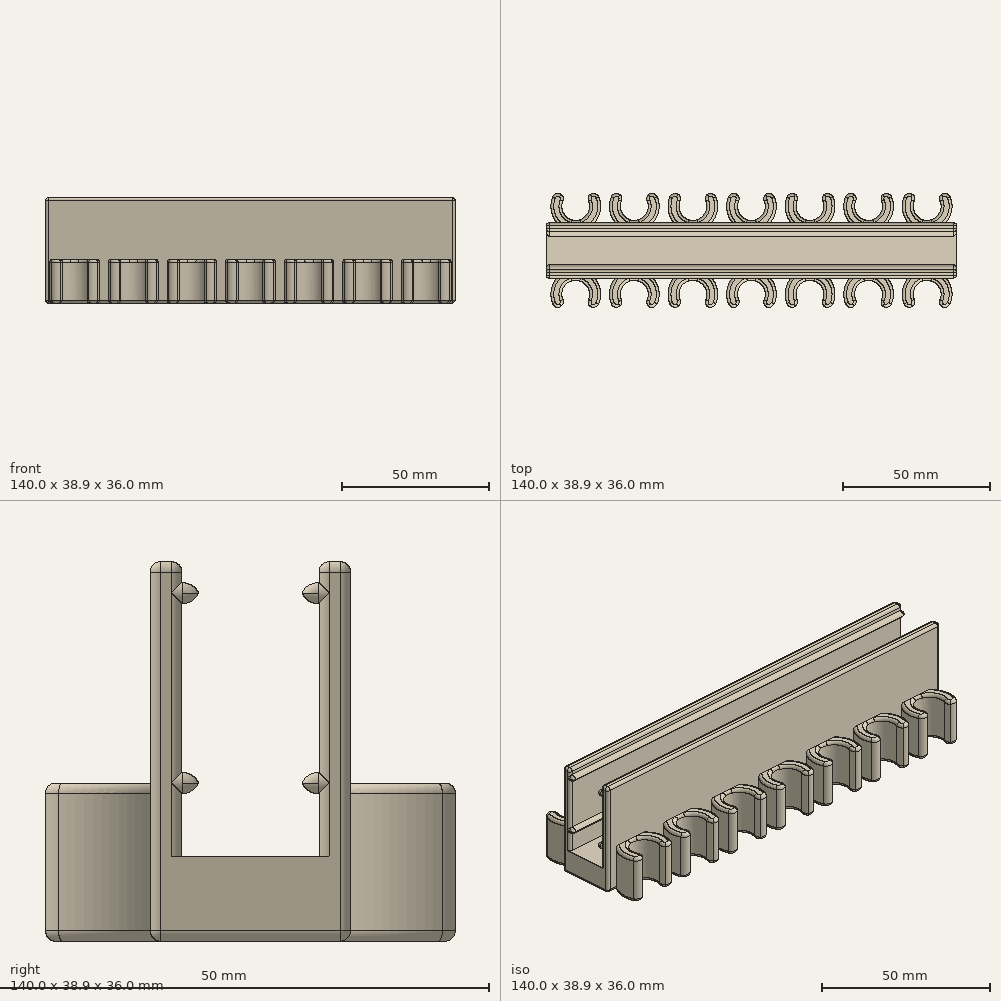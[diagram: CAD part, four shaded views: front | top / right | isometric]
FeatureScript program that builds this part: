
annotation { "Feature Type Name" : "Feature", "Feature Type Description" : "" }
export const myFeature = defineFeature(function(context is Context, id is Id, definition is map)
    precondition{}
    {
        {
            var Q0;
            Q0=qCreatedBy(makeId("Top.planeOp"),FACE);
            var sketch = newSketch(context, id + "F0", { "sketchPlane" : qUnion([Q0])});
            skLineSegment(sketch, "E0.0", {"start": v(-67.34, 9.93) * mm, "end": v(-70.86, 9.93) * mm});
            skLineSegment(sketch, "E1", {"start": v(-54.38, 9.93) * mm, "end": v(-47.34, 9.93) * mm});
            skArc(sketch, "E2", {"start": v(-67.37, 20.9) * mm, "mid": v(-69.36, 15.4) * mm, "end": v(-67.34, 9.93) * mm});
            skArc(sketch, "E3", {"start": v(-64.5, 18.48) * mm, "mid": v(-60.86, 10.68) * mm, "end": v(-57.22, 18.48) * mm});
            skLineSegment(sketch, "E4", {"start": v(-64.5, 18.48) * mm, "end": v(-67.37, 20.9) * mm});
            skLineSegment(sketch, "E5", {"start": v(-57.22, 18.48) * mm, "end": v(-54.35, 20.9) * mm});
            skLineSegment(sketch, "E6.1.0.0", {"start": v(-44.5, 18.48) * mm, "end": v(-47.37, 20.9) * mm});
            skArc(sketch, "E6.1.0.1", {"start": v(-47.37, 20.9) * mm, "mid": v(-49.36, 15.4) * mm, "end": v(-47.34, 9.93) * mm});
            skArc(sketch, "E6.1.0.2", {"start": v(-44.5, 18.48) * mm, "mid": v(-40.86, 10.68) * mm, "end": v(-37.22, 18.48) * mm});
            skLineSegment(sketch, "E6.1.0.3", {"start": v(-37.22, 18.48) * mm, "end": v(-34.35, 20.9) * mm});
            skLineSegment(sketch, "E6.2.0.0", {"start": v(-24.5, 18.48) * mm, "end": v(-27.37, 20.9) * mm});
            skArc(sketch, "E6.2.0.1", {"start": v(-27.37, 20.9) * mm, "mid": v(-29.36, 15.4) * mm, "end": v(-27.34, 9.93) * mm});
            skArc(sketch, "E6.2.0.2", {"start": v(-24.5, 18.48) * mm, "mid": v(-20.86, 10.68) * mm, "end": v(-17.22, 18.48) * mm});
            skLineSegment(sketch, "E6.2.0.3", {"start": v(-17.22, 18.48) * mm, "end": v(-14.35, 20.9) * mm});
            skLineSegment(sketch, "E6.3.0.0", {"start": v(-4.5, 18.48) * mm, "end": v(-7.37, 20.9) * mm});
            skArc(sketch, "E6.3.0.1", {"start": v(-7.37, 20.9) * mm, "mid": v(-9.36, 15.4) * mm, "end": v(-7.34, 9.93) * mm});
            skArc(sketch, "E6.3.0.2", {"start": v(-4.5, 18.48) * mm, "mid": v(-0.86, 10.68) * mm, "end": v(2.78, 18.48) * mm});
            skLineSegment(sketch, "E6.3.0.3", {"start": v(2.78, 18.48) * mm, "end": v(5.65, 20.9) * mm});
            skLineSegment(sketch, "E6.4.0.0", {"start": v(15.5, 18.48) * mm, "end": v(12.63, 20.9) * mm});
            skArc(sketch, "E6.4.0.1", {"start": v(12.63, 20.9) * mm, "mid": v(10.64, 15.4) * mm, "end": v(12.66, 9.93) * mm});
            skArc(sketch, "E6.4.0.2", {"start": v(15.5, 18.48) * mm, "mid": v(19.14, 10.68) * mm, "end": v(22.78, 18.48) * mm});
            skLineSegment(sketch, "E6.4.0.3", {"start": v(22.78, 18.48) * mm, "end": v(25.65, 20.9) * mm});
            skLineSegment(sketch, "E6.5.0.0", {"start": v(35.5, 18.48) * mm, "end": v(32.63, 20.9) * mm});
            skArc(sketch, "E6.5.0.1", {"start": v(32.63, 20.9) * mm, "mid": v(30.64, 15.4) * mm, "end": v(32.66, 9.93) * mm});
            skArc(sketch, "E6.5.0.2", {"start": v(35.5, 18.48) * mm, "mid": v(39.14, 10.68) * mm, "end": v(42.78, 18.48) * mm});
            skLineSegment(sketch, "E6.5.0.3", {"start": v(42.78, 18.48) * mm, "end": v(45.65, 20.9) * mm});
            skLineSegment(sketch, "E6.6.0.0", {"start": v(55.5, 18.48) * mm, "end": v(52.63, 20.9) * mm});
            skArc(sketch, "E6.6.0.1", {"start": v(52.63, 20.9) * mm, "mid": v(50.64, 15.4) * mm, "end": v(52.66, 9.93) * mm});
            skArc(sketch, "E6.6.0.2", {"start": v(55.5, 18.48) * mm, "mid": v(59.14, 10.68) * mm, "end": v(62.78, 18.48) * mm});
            skLineSegment(sketch, "E6.6.0.3", {"start": v(62.78, 18.48) * mm, "end": v(65.65, 20.9) * mm});
            skLineSegment(sketch, "E7.trimOffspring", {"start": v(-34.38, 9.93) * mm, "end": v(-27.34, 9.93) * mm});
            skLineSegment(sketch, "E8.trimOffspring", {"start": v(-14.38, 9.93) * mm, "end": v(-7.34, 9.93) * mm});
            skLineSegment(sketch, "E9.trimOffspring", {"start": v(5.62, 9.93) * mm, "end": v(12.66, 9.93) * mm});
            skLineSegment(sketch, "E10.trimOffspring", {"start": v(25.62, 9.93) * mm, "end": v(32.66, 9.93) * mm});
            skLineSegment(sketch, "E11.trimOffspring", {"start": v(45.62, 9.93) * mm, "end": v(52.66, 9.93) * mm});
            skLineSegment(sketch, "E12.trimOffspring", {"start": v(65.62, 9.93) * mm, "end": v(69.14, 9.93) * mm});
            skLineSegment(sketch, "E13", {"start": v(69.14, 9.93) * mm, "end": v(69.14, 0.43) * mm});
            skLineSegment(sketch, "E14", {"start": v(-70.86, 0.43) * mm, "end": v(-70.86, 9.93) * mm});
            skArc(sketch, "E15.trimOffspring", {"start": v(-54.38, 9.93) * mm, "mid": v(-52.36, 15.4) * mm, "end": v(-54.35, 20.9) * mm});
            skArc(sketch, "E16.trimOffspring", {"start": v(-34.38, 9.93) * mm, "mid": v(-32.36, 15.4) * mm, "end": v(-34.35, 20.9) * mm});
            skArc(sketch, "E17.trimOffspring", {"start": v(-14.38, 9.93) * mm, "mid": v(-12.36, 15.4) * mm, "end": v(-14.35, 20.9) * mm});
            skArc(sketch, "E18.trimOffspring", {"start": v(5.62, 9.93) * mm, "mid": v(7.64, 15.4) * mm, "end": v(5.65, 20.9) * mm});
            skArc(sketch, "E19.trimOffspring", {"start": v(25.62, 9.93) * mm, "mid": v(27.64, 15.4) * mm, "end": v(25.65, 20.9) * mm});
            skArc(sketch, "E20.trimOffspring", {"start": v(45.62, 9.93) * mm, "mid": v(47.64, 15.4) * mm, "end": v(45.65, 20.9) * mm});
            skArc(sketch, "E21.trimOffspring", {"start": v(65.62, 9.93) * mm, "mid": v(67.64, 15.4) * mm, "end": v(65.65, 20.9) * mm});
            skLineSegment(sketch, "E22", {"start": v(-70.86, 0.43) * mm, "end": v(69.14, 0.43) * mm});
            skSolve(sketch);
        }
        {
            var Q0;
            Q0=makeQuery(id+"F0.imprint","IMPRINT",FACE,{"disambiguationData":[TD([[makeQuery(id+"F0.imprint","IMPRINT",EDGE,{"derivedFrom":sQuery(id+"F0.wireOp",EDGE,"E0.0")}),1.0]])]});
            extrude(context, id + "F1", {"entities" : qUnion([Q0]), "depth" : 15 * mm});
        }
        {
            var Q0;
            Q0=makeQuery(id+"F1.opExtrude","CAP_FACE",FACE,{"disambiguationData":[OSD([sQuery(id+"F0.wireOp",EDGE,"E0.0"),sQuery(id+"F0.wireOp",EDGE,"E1"),sQuery(id+"F0.wireOp",EDGE,"E2"),sQuery(id+"F0.wireOp",EDGE,"E3"),sQuery(id+"F0.wireOp",EDGE,"E4"),sQuery(id+"F0.wireOp",EDGE,"E5"),sQuery(id+"F0.wireOp",EDGE,"E6.1.0.0"),sQuery(id+"F0.wireOp",EDGE,"E6.1.0.1"),sQuery(id+"F0.wireOp",EDGE,"E6.1.0.2"),sQuery(id+"F0.wireOp",EDGE,"E6.1.0.3"),sQuery(id+"F0.wireOp",EDGE,"E6.2.0.0"),sQuery(id+"F0.wireOp",EDGE,"E6.2.0.1"),sQuery(id+"F0.wireOp",EDGE,"E6.2.0.2"),sQuery(id+"F0.wireOp",EDGE,"E6.2.0.3"),sQuery(id+"F0.wireOp",EDGE,"E6.3.0.0"),sQuery(id+"F0.wireOp",EDGE,"E6.3.0.1"),sQuery(id+"F0.wireOp",EDGE,"E6.3.0.2"),sQuery(id+"F0.wireOp",EDGE,"E6.3.0.3"),sQuery(id+"F0.wireOp",EDGE,"E6.4.0.0"),sQuery(id+"F0.wireOp",EDGE,"E6.4.0.1"),sQuery(id+"F0.wireOp",EDGE,"E6.4.0.2"),sQuery(id+"F0.wireOp",EDGE,"E6.4.0.3"),sQuery(id+"F0.wireOp",EDGE,"E6.5.0.0"),sQuery(id+"F0.wireOp",EDGE,"E6.5.0.1"),sQuery(id+"F0.wireOp",EDGE,"E6.5.0.2"),sQuery(id+"F0.wireOp",EDGE,"E6.5.0.3"),sQuery(id+"F0.wireOp",EDGE,"E6.6.0.0"),sQuery(id+"F0.wireOp",EDGE,"E6.6.0.1"),sQuery(id+"F0.wireOp",EDGE,"E6.6.0.2"),sQuery(id+"F0.wireOp",EDGE,"E6.6.0.3"),sQuery(id+"F0.wireOp",EDGE,"E7.trimOffspring"),sQuery(id+"F0.wireOp",EDGE,"E8.trimOffspring"),sQuery(id+"F0.wireOp",EDGE,"E9.trimOffspring"),sQuery(id+"F0.wireOp",EDGE,"E10.trimOffspring"),sQuery(id+"F0.wireOp",EDGE,"E11.trimOffspring"),sQuery(id+"F0.wireOp",EDGE,"E12.trimOffspring"),sQuery(id+"F0.wireOp",EDGE,"E13"),sQuery(id+"F0.wireOp",EDGE,"E14"),sQuery(id+"F0.wireOp",EDGE,"532ac394-174c-4b63-97db-7bd679016d38.MirrorCS"),sQuery(id+"F0.wireOp",EDGE,"c05681d9-5c30-460e-90d8-317d1354b1ce.MirrorCS"),sQuery(id+"F0.wireOp",EDGE,"32390daf-9b7e-4632-84e2-2c85bb95c461.MirrorCS"),sQuery(id+"F0.wireOp",EDGE,"01d35694-a45f-4d88-895f-8290f8c5d0fa.MirrorCS"),sQuery(id+"F0.wireOp",EDGE,"542af53a-2461-44a8-a463-2401990404e3.MirrorCS"),sQuery(id+"F0.wireOp",EDGE,"50974922-5e88-405f-beb8-3457a77c02c8.MirrorCS"),sQuery(id+"F0.wireOp",EDGE,"9a1d3fd9-fa9d-4549-b3c9-1b6f4156c3cd.MirrorCS"),sQuery(id+"F0.wireOp",EDGE,"a6e0a99f-08c5-4def-a0f1-34a534e11dcb.MirrorCS"),sQuery(id+"F0.wireOp",EDGE,"85859d06-1dbf-410a-b8d5-c9659a816373.MirrorCS"),sQuery(id+"F0.wireOp",EDGE,"bb1e909d-42a2-430b-9b04-417277d03ddc.MirrorCS"),sQuery(id+"F0.wireOp",EDGE,"dd3b9dcb-f5d1-4367-832f-4155d99a0f53.MirrorCS"),sQuery(id+"F0.wireOp",EDGE,"95d68850-7c9b-44dc-a881-3d0e4710346b.MirrorCS"),sQuery(id+"F0.wireOp",EDGE,"cb06743f-0ef2-4490-bbfb-8208ed74ea54.MirrorCS"),sQuery(id+"F0.wireOp",EDGE,"8bc326fa-f220-4284-8f0f-31372991c1d0.MirrorCS"),sQuery(id+"F0.wireOp",EDGE,"61d51338-7109-43f4-9b26-85c12fe8dddc.MirrorCS"),sQuery(id+"F0.wireOp",EDGE,"ce3784da-6652-4a49-9029-c9d91698aa87.MirrorCS"),sQuery(id+"F0.wireOp",EDGE,"d0945471-aaf3-4442-996e-3f852aa85cf1.MirrorCS"),sQuery(id+"F0.wireOp",EDGE,"8b2dfc5c-2465-4331-950a-6d09cef2b768.MirrorCS"),sQuery(id+"F0.wireOp",EDGE,"7d31813b-8c42-40b0-b29a-5ec110f622fe.MirrorCS"),sQuery(id+"F0.wireOp",EDGE,"895840e0-dc65-487e-9daf-0c2dc7c5ed62.MirrorCS"),sQuery(id+"F0.wireOp",EDGE,"8443182a-963f-49ce-a89f-3df1a04f3471.MirrorCS"),sQuery(id+"F0.wireOp",EDGE,"07ffd3f9-8c22-4c6a-b8bf-5acca4b2ffac.MirrorCS"),sQuery(id+"F0.wireOp",EDGE,"76d25652-5567-47d0-86c3-db02a34db9a5.MirrorCS"),sQuery(id+"F0.wireOp",EDGE,"dc33f74a-ec70-42cc-9042-cb16d190b05e.MirrorCS"),sQuery(id+"F0.wireOp",EDGE,"53c614f0-cb83-4180-b471-f4b910b1941e.MirrorCS"),sQuery(id+"F0.wireOp",EDGE,"8c3fe504-64fb-41a5-82f7-0502142477f2.MirrorCS"),sQuery(id+"F0.wireOp",EDGE,"c5e72435-b01b-49d2-a203-b66ee6d8c885.MirrorCS"),sQuery(id+"F0.wireOp",EDGE,"19d9c78f-6ca9-424a-8982-828d9996df5d.MirrorCS"),sQuery(id+"F0.wireOp",EDGE,"1e641c59-deae-4c4d-ac71-77fc781e1db0.MirrorCS"),sQuery(id+"F0.wireOp",EDGE,"8ad635c3-a3ff-4ec7-b15b-9205133ed604.MirrorCS"),sQuery(id+"F0.wireOp",EDGE,"a49b1a12-b06d-43a0-ab83-94a35d7ba3b6.MirrorCS"),sQuery(id+"F0.wireOp",EDGE,"bcde4f51-7e24-40fe-ab17-a5a08aa31fcd.MirrorCS"),sQuery(id+"F0.wireOp",EDGE,"393ad891-5551-46bd-9f78-a4b207928a0a.MirrorCS"),sQuery(id+"F0.wireOp",EDGE,"b6b4b9c5-b1e0-4867-b064-6f7972b9574b.MirrorCS"),sQuery(id+"F0.wireOp",EDGE,"bb3e8bfc-5aea-4390-acdf-16b4f7f6207e.MirrorCS"),sQuery(id+"F0.wireOp",EDGE,"800d67ee-cbba-4591-aae2-d5247f1543fd.MirrorCS"),sQuery(id+"F0.wireOp",EDGE,"2f3bc7cb-4e2a-4f65-84bb-f5e8203fa07d.MirrorCS"),sQuery(id+"F0.wireOp",EDGE,"118a9efa-6c1d-49a3-b5ec-82cfceddfd38.MirrorCS"),sQuery(id+"F0.wireOp",EDGE,"E15.trimOffspring"),sQuery(id+"F0.wireOp",EDGE,"ff7412fe-da9d-4180-b698-66fe01a22e62.trimOffspring"),sQuery(id+"F0.wireOp",EDGE,"4496308e-0bbc-4981-83e8-c6594c4fa23c.trimOffspring"),sQuery(id+"F0.wireOp",EDGE,"E16.trimOffspring"),sQuery(id+"F0.wireOp",EDGE,"E17.trimOffspring"),sQuery(id+"F0.wireOp",EDGE,"E18.trimOffspring"),sQuery(id+"F0.wireOp",EDGE,"E19.trimOffspring"),sQuery(id+"F0.wireOp",EDGE,"E20.trimOffspring"),sQuery(id+"F0.wireOp",EDGE,"E21.trimOffspring"),sQuery(id+"F0.wireOp",EDGE,"9ee47ddf-eb93-4049-a59d-f92f7ca8a253.trimOffspring"),sQuery(id+"F0.wireOp",EDGE,"7a309b6b-a9af-437c-b1e7-8ac5cff17d63.trimOffspring"),sQuery(id+"F0.wireOp",EDGE,"a429b228-3a7c-4e15-a61f-9e9e64befbed.trimOffspring"),sQuery(id+"F0.wireOp",EDGE,"04ba02ae-33ee-469e-a187-3e9e85af7747.trimOffspring"),sQuery(id+"F0.wireOp",EDGE,"f3fa248c-7e1b-4735-8d48-9965b376265a.trimOffspring")])],"isStart":false});
            var sketch = newSketch(context, id + "F2", { "sketchPlane" : qUnion([Q0])});
            skLineSegment(sketch, "E23", {"start": v(-70.86, 9.93) * mm, "end": v(69.14, 9.93) * mm});
            skLineSegment(sketch, "E24", {"start": v(69.14, 6.93) * mm, "end": v(-70.86, 6.93) * mm});
            skSolve(sketch);
        }
        {
            var Q0;
            {var subQ0=sQuery(id+"F2.wireOp",EDGE,"E24");Q0=makeQuery(id+"F2.imprint","IMPRINT",FACE,{"disambiguationData":[TD([[makeQuery(id+"F2.imprint","IMPRINT",EDGE,{"derivedFrom":subQ0}),1.0]])]});}
            extrude(context, id + "F3", {"entities" : qUnion([Q0]), "operationType" : NewBodyOperationType.REMOVE, "oppositeDirection" : true, "depth" : 7 * mm});
        }
        {
            var Q0;
            {var subQ19=sQuery(id+"F2.wireOp",EDGE,"E24");Q0=makeQuery(id+"F2.imprint","IMPRINT",FACE,{"disambiguationData":[TD([[makeQuery(id+"F2.imprint","IMPRINT",EDGE,{"derivedFrom":subQ19}),-1.0]])]});}
            var Q1;
            {var subQ11=sQuery(id+"F2.wireOp",EDGE,"yWHUweg9-QDUr-fazm-nHLA-YuGdJbdEGouv");Q1=makeQuery(id+"F2.imprint","IMPRINT",FACE,{"disambiguationData":[TD([[makeQuery(id+"F2.imprint","IMPRINT",EDGE,{"derivedFrom":subQ11}),1.0]])]});}
            extrude(context, id + "F4", {"entities" : qUnion([Q0, Q1]), "operationType" : NewBodyOperationType.ADD, "depth" : 21 * mm});
        }
        {
            var Q0;
            Q0=makeQuery(id+"F1.opExtrude","SWEPT_EDGE",EDGE,{"disambiguationData":[OSD([sQuery(id+"F0.wireOp",EDGE,"E3"),sQuery(id+"F0.wireOp",EDGE,"E4")])]});
            var Q1;
            Q1=makeQuery(id+"F1.opExtrude","SWEPT_EDGE",EDGE,{"disambiguationData":[OSD([sQuery(id+"F0.wireOp",EDGE,"E2"),sQuery(id+"F0.wireOp",EDGE,"E4")])]});
            var Q2;
            Q2=makeQuery(id+"F1.opExtrude","SWEPT_EDGE",EDGE,{"disambiguationData":[OSD([sQuery(id+"F0.wireOp",EDGE,"E3"),sQuery(id+"F0.wireOp",EDGE,"E5")])]});
            var Q3;
            Q3=makeQuery(id+"F1.opExtrude","SWEPT_EDGE",EDGE,{"disambiguationData":[OSD([sQuery(id+"F0.wireOp",EDGE,"E5"),sQuery(id+"F0.wireOp",EDGE,"E15.trimOffspring")])]});
            var Q4;
            Q4=makeQuery(id+"F1.opExtrude","SWEPT_EDGE",EDGE,{"disambiguationData":[OSD([sQuery(id+"F0.wireOp",EDGE,"E6.1.0.0"),sQuery(id+"F0.wireOp",EDGE,"E6.1.0.1")])]});
            var Q5;
            Q5=makeQuery(id+"F1.opExtrude","SWEPT_EDGE",EDGE,{"disambiguationData":[OSD([sQuery(id+"F0.wireOp",EDGE,"E6.1.0.0"),sQuery(id+"F0.wireOp",EDGE,"E6.1.0.2")])]});
            var Q6;
            Q6=makeQuery(id+"F1.opExtrude","SWEPT_EDGE",EDGE,{"disambiguationData":[OSD([sQuery(id+"F0.wireOp",EDGE,"E6.1.0.2"),sQuery(id+"F0.wireOp",EDGE,"E6.1.0.3")])]});
            var Q7;
            Q7=makeQuery(id+"F1.opExtrude","SWEPT_EDGE",EDGE,{"disambiguationData":[OSD([sQuery(id+"F0.wireOp",EDGE,"E6.1.0.3"),sQuery(id+"F0.wireOp",EDGE,"E16.trimOffspring")])]});
            var Q8;
            Q8=makeQuery(id+"F1.opExtrude","SWEPT_EDGE",EDGE,{"disambiguationData":[OSD([sQuery(id+"F0.wireOp",EDGE,"E6.2.0.0"),sQuery(id+"F0.wireOp",EDGE,"E6.2.0.1")])]});
            var Q9;
            Q9=makeQuery(id+"F1.opExtrude","SWEPT_EDGE",EDGE,{"disambiguationData":[OSD([sQuery(id+"F0.wireOp",EDGE,"E6.2.0.0"),sQuery(id+"F0.wireOp",EDGE,"E6.2.0.2")])]});
            var Q10;
            Q10=makeQuery(id+"F1.opExtrude","SWEPT_EDGE",EDGE,{"disambiguationData":[OSD([sQuery(id+"F0.wireOp",EDGE,"E6.2.0.2"),sQuery(id+"F0.wireOp",EDGE,"E6.2.0.3")])]});
            var Q11;
            Q11=makeQuery(id+"F1.opExtrude","SWEPT_EDGE",EDGE,{"disambiguationData":[OSD([sQuery(id+"F0.wireOp",EDGE,"E6.2.0.3"),sQuery(id+"F0.wireOp",EDGE,"E17.trimOffspring")])]});
            var Q12;
            Q12=makeQuery(id+"F1.opExtrude","SWEPT_EDGE",EDGE,{"disambiguationData":[OSD([sQuery(id+"F0.wireOp",EDGE,"E6.3.0.0"),sQuery(id+"F0.wireOp",EDGE,"E6.3.0.1")])]});
            var Q13;
            Q13=makeQuery(id+"F1.opExtrude","SWEPT_EDGE",EDGE,{"disambiguationData":[OSD([sQuery(id+"F0.wireOp",EDGE,"E6.3.0.0"),sQuery(id+"F0.wireOp",EDGE,"E6.3.0.2")])]});
            var Q14;
            Q14=makeQuery(id+"F1.opExtrude","SWEPT_EDGE",EDGE,{"disambiguationData":[OSD([sQuery(id+"F0.wireOp",EDGE,"E6.3.0.2"),sQuery(id+"F0.wireOp",EDGE,"E6.3.0.3")])]});
            var Q15;
            Q15=makeQuery(id+"F1.opExtrude","SWEPT_EDGE",EDGE,{"disambiguationData":[OSD([sQuery(id+"F0.wireOp",EDGE,"E6.3.0.3"),sQuery(id+"F0.wireOp",EDGE,"E18.trimOffspring")])]});
            var Q16;
            Q16=makeQuery(id+"F1.opExtrude","SWEPT_EDGE",EDGE,{"disambiguationData":[OSD([sQuery(id+"F0.wireOp",EDGE,"E6.4.0.0"),sQuery(id+"F0.wireOp",EDGE,"E6.4.0.1")])]});
            var Q17;
            Q17=makeQuery(id+"F1.opExtrude","SWEPT_EDGE",EDGE,{"disambiguationData":[OSD([sQuery(id+"F0.wireOp",EDGE,"E6.4.0.0"),sQuery(id+"F0.wireOp",EDGE,"E6.4.0.2")])]});
            var Q18;
            Q18=makeQuery(id+"F1.opExtrude","SWEPT_EDGE",EDGE,{"disambiguationData":[OSD([sQuery(id+"F0.wireOp",EDGE,"E6.4.0.2"),sQuery(id+"F0.wireOp",EDGE,"E6.4.0.3")])]});
            var Q19;
            Q19=makeQuery(id+"F1.opExtrude","SWEPT_EDGE",EDGE,{"disambiguationData":[OSD([sQuery(id+"F0.wireOp",EDGE,"E6.4.0.3"),sQuery(id+"F0.wireOp",EDGE,"E19.trimOffspring")])]});
            var Q20;
            Q20=makeQuery(id+"F1.opExtrude","SWEPT_EDGE",EDGE,{"disambiguationData":[OSD([sQuery(id+"F0.wireOp",EDGE,"E6.5.0.0"),sQuery(id+"F0.wireOp",EDGE,"E6.5.0.1")])]});
            var Q21;
            Q21=makeQuery(id+"F1.opExtrude","SWEPT_EDGE",EDGE,{"disambiguationData":[OSD([sQuery(id+"F0.wireOp",EDGE,"E6.5.0.0"),sQuery(id+"F0.wireOp",EDGE,"E6.5.0.2")])]});
            var Q22;
            Q22=makeQuery(id+"F1.opExtrude","SWEPT_EDGE",EDGE,{"disambiguationData":[OSD([sQuery(id+"F0.wireOp",EDGE,"E6.5.0.3"),sQuery(id+"F0.wireOp",EDGE,"E20.trimOffspring")])]});
            var Q23;
            Q23=makeQuery(id+"F1.opExtrude","SWEPT_EDGE",EDGE,{"disambiguationData":[OSD([sQuery(id+"F0.wireOp",EDGE,"E6.5.0.2"),sQuery(id+"F0.wireOp",EDGE,"E6.5.0.3")])]});
            var Q24;
            Q24=makeQuery(id+"F1.opExtrude","SWEPT_EDGE",EDGE,{"disambiguationData":[OSD([sQuery(id+"F0.wireOp",EDGE,"E6.6.0.0"),sQuery(id+"F0.wireOp",EDGE,"E6.6.0.1")])]});
            var Q25;
            Q25=makeQuery(id+"F1.opExtrude","SWEPT_EDGE",EDGE,{"disambiguationData":[OSD([sQuery(id+"F0.wireOp",EDGE,"E6.6.0.0"),sQuery(id+"F0.wireOp",EDGE,"E6.6.0.2")])]});
            var Q26;
            Q26=makeQuery(id+"F1.opExtrude","SWEPT_EDGE",EDGE,{"disambiguationData":[OSD([sQuery(id+"F0.wireOp",EDGE,"E6.6.0.2"),sQuery(id+"F0.wireOp",EDGE,"E6.6.0.3")])]});
            var Q27;
            Q27=makeQuery(id+"F1.opExtrude","SWEPT_EDGE",EDGE,{"disambiguationData":[OSD([sQuery(id+"F0.wireOp",EDGE,"E6.6.0.3"),sQuery(id+"F0.wireOp",EDGE,"E21.trimOffspring")])]});
            fillet(context, id + "F5", {"entities" : qUnion([Q0, Q1, Q2, Q3, Q4, Q5, Q6, Q7, Q8, Q9, Q10, Q11, Q12, Q13, Q14, Q15, Q16, Q17, Q18, Q19, Q20, Q21, Q22, Q23, Q24, Q25, Q26, Q27]), "radius" : 2 * mm, "tangentPropagation" : true, "allowEdgeOverflow" : false});
        }
        {
            var Q0;
            {var subQ0=sQuery(id+"F0.wireOp",EDGE,"E13");Q0=makeQuery(id+"F4.boolean.opBoolean","MERGE",FACE,{"derivedFrom":[makeQuery(id+"F1.opExtrude","SWEPT_FACE",FACE,{"disambiguationData":[OSD([subQ0])]}),makeQuery(id+"F4.opExtrude","SWEPT_FACE",FACE,{"disambiguationData":[OSD([subQ0])]})]});}
            var sketch = newSketch(context, id + "F6", { "sketchPlane" : qUnion([Q0])});
            skLineSegment(sketch, "E25", {"start": v(6.93, 15) * mm, "end": v(6.93, 33) * mm});
            skLineSegment(sketch, "E26.bottom", {"start": v(5.18, 14) * mm, "end": v(8.68, 14) * mm});
            skLineSegment(sketch, "E26.top", {"start": v(5.18, 16) * mm, "end": v(8.68, 16) * mm});
            skLineSegment(sketch, "E26.left", {"start": v(5.18, 14) * mm, "end": v(5.18, 16) * mm});
            skLineSegment(sketch, "E26.right", {"start": v(8.68, 14) * mm, "end": v(8.68, 16) * mm});
            skPoint(sketch, "E26.middle", {"position": v(6.93, 15) * mm});
            skLineSegment(sketch, "E27.bottom", {"start": v(5.18, 32) * mm, "end": v(8.68, 32) * mm});
            skLineSegment(sketch, "E27.top", {"start": v(5.18, 34) * mm, "end": v(8.68, 34) * mm});
            skLineSegment(sketch, "E27.left", {"start": v(5.18, 32) * mm, "end": v(5.18, 34) * mm});
            skLineSegment(sketch, "E27.right", {"start": v(8.68, 32) * mm, "end": v(8.68, 34) * mm});
            skPoint(sketch, "E27.middle", {"position": v(6.93, 33) * mm});
            skSolve(sketch);
        }
        {
            var Q0;
            {var subQ0=sQuery(id+"F6.wireOp",EDGE,"E26.left");Q0=makeQuery(id+"F6.imprint","IMPRINT",FACE,{"disambiguationData":[TD([[makeQuery(id+"F6.imprint","IMPRINT",EDGE,{"derivedFrom":subQ0}),-1.0]])]});}
            var Q1;
            {var subQ0=sQuery(id+"F6.wireOp",EDGE,"E27.left");Q1=makeQuery(id+"F6.imprint","IMPRINT",FACE,{"disambiguationData":[TD([[makeQuery(id+"F6.imprint","IMPRINT",EDGE,{"derivedFrom":subQ0}),-1.0]])]});}
            var Q2;
            {var subQ0=sQuery(id+"F0.wireOp",EDGE,"E14");Q2=makeQuery(id+"F4.boolean.opBoolean","MERGE",FACE,{"derivedFrom":[makeQuery(id+"F1.opExtrude","SWEPT_FACE",FACE,{"disambiguationData":[OSD([subQ0])]}),makeQuery(id+"F4.opExtrude","SWEPT_FACE",FACE,{"disambiguationData":[OSD([subQ0])]})]});}
            extrude(context, id + "F7", {"entities" : qUnion([Q0, Q1]), "operationType" : NewBodyOperationType.ADD, "endBound" : BoundingType.UP_TO_SURFACE, "oppositeDirection" : true, "endBoundEntityFace" : qUnion([Q2]), "depth" : 25 * mm});
        }
        {
            var Q0;
            Q0=makeQuery(id+"F7.opExtrude","SWEPT_EDGE",EDGE,{"disambiguationData":[OSD([sQuery(id+"F6.wireOp",EDGE,"E27.top"),sQuery(id+"F6.wireOp",EDGE,"E27.left")])]});
            var Q1;
            Q1=makeQuery(id+"F7.opExtrude","SWEPT_EDGE",EDGE,{"disambiguationData":[OSD([sQuery(id+"F6.wireOp",EDGE,"E27.bottom"),sQuery(id+"F6.wireOp",EDGE,"E27.left")])]});
            var Q2;
            Q2=makeQuery(id+"F7.opExtrude","SWEPT_EDGE",EDGE,{"disambiguationData":[OSD([sQuery(id+"F6.wireOp",EDGE,"E26.top"),sQuery(id+"F6.wireOp",EDGE,"E26.left")])]});
            var Q3;
            Q3=makeQuery(id+"F7.opExtrude","SWEPT_EDGE",EDGE,{"disambiguationData":[OSD([sQuery(id+"F6.wireOp",EDGE,"E26.bottom"),sQuery(id+"F6.wireOp",EDGE,"E26.left")])]});
            fillet(context, id + "F8", {"entities" : qUnion([Q0, Q1, Q2, Q3]), "radius" : 1.7 * mm, "tangentPropagation" : true, "allowEdgeOverflow" : false});
        }
        {
            var Q0;
            Q0=makeQuery(id+"F4.opExtrude","CAP_FACE",FACE,{"disambiguationData":[OSD([sQuery(id+"F0.wireOp",EDGE,"E13"),sQuery(id+"F0.wireOp",EDGE,"E14"),sQuery(id+"F2.wireOp",EDGE,"E23"),sQuery(id+"F2.wireOp",EDGE,"E24")])],"isStart":false});
            var Q1;
            {var subQ0=sQuery(id+"F2.wireOp",EDGE,"E24");var subQ1=sQuery(id+"F0.wireOp",EDGE,"E13");var subQ2=sQuery(id+"F6.wireOp",EDGE,"E27.top");Q1=makeQuery(id+"F7.boolean.opBoolean","SPLIT",EDGE,{"disambiguationData":[TD([makeQuery(id+"F7.opExtrude","SWEPT_FACE",FACE,{"disambiguationData":[OSD([subQ2])]})])],"derivedFrom":makeQuery(id+"F4.boolean.opBoolean","MERGE",EDGE,{"derivedFrom":[makeQuery(id+"F3.boolean.opBoolean","COPY",EDGE,{"derivedFrom":makeQuery(id+"F3.opExtrude","SWEPT_EDGE",EDGE,{"disambiguationData":[OSD([subQ1,subQ0])]})}),makeQuery(id+"F4.opExtrude","SWEPT_EDGE",EDGE,{"disambiguationData":[OSD([subQ1,subQ0])]})]})});}
            var Q2;
            {var subQ0=sQuery(id+"F6.wireOp",EDGE,"E27.left");var subQ1=sQuery(id+"F6.wireOp",EDGE,"E27.top");var subQ2=sQuery(id+"F6.wireOp",EDGE,"E25");var subQ3=sQuery(id+"F2.wireOp",EDGE,"E24");var subQ4=sQuery(id+"F0.wireOp",EDGE,"E13");Q2=makeQuery(id+"F8.opFillet","BLEND_EDGE",EDGE,{"blendedFrom":[makeQuery(id+"F7.opExtrude","SWEPT_EDGE",EDGE,{"disambiguationData":[OSD([subQ1,subQ0])]}),makeQuery(id+"F7.boolean.opBoolean","MERGE",FACE,{"derivedFrom":[makeQuery(id+"F4.boolean.opBoolean","MERGE",FACE,{"derivedFrom":[makeQuery(id+"F1.opExtrude","SWEPT_FACE",FACE,{"disambiguationData":[OSD([subQ4])]}),makeQuery(id+"F4.opExtrude","SWEPT_FACE",FACE,{"disambiguationData":[OSD([subQ4])]})]}),makeQuery(id+"F7.opExtrude","CAP_FACE",FACE,{"disambiguationData":[OSD([subQ4,subQ3,subQ2,sQuery(id+"F6.wireOp",EDGE,"E26.bottom"),sQuery(id+"F6.wireOp",EDGE,"E26.top"),sQuery(id+"F6.wireOp",EDGE,"E26.left")])],"isStart":true}),makeQuery(id+"F7.opExtrude","CAP_FACE",FACE,{"disambiguationData":[OSD([subQ4,subQ3,subQ2,sQuery(id+"F6.wireOp",EDGE,"E27.bottom"),subQ1,subQ0])],"isStart":true})]})],"blendedInto":[makeQuery(id+"F7.boolean.opBoolean","MERGE",FACE,{"derivedFrom":[makeQuery(id+"F4.boolean.opBoolean","MERGE",FACE,{"derivedFrom":[makeQuery(id+"F1.opExtrude","SWEPT_FACE",FACE,{"disambiguationData":[OSD([subQ4])]}),makeQuery(id+"F4.opExtrude","SWEPT_FACE",FACE,{"disambiguationData":[OSD([subQ4])]})]}),makeQuery(id+"F7.opExtrude","CAP_FACE",FACE,{"disambiguationData":[OSD([subQ4,subQ3,subQ2,sQuery(id+"F6.wireOp",EDGE,"E26.bottom"),sQuery(id+"F6.wireOp",EDGE,"E26.top"),sQuery(id+"F6.wireOp",EDGE,"E26.left")])],"isStart":true}),makeQuery(id+"F7.opExtrude","CAP_FACE",FACE,{"disambiguationData":[OSD([subQ4,subQ3,subQ2,sQuery(id+"F6.wireOp",EDGE,"E27.bottom"),subQ1,subQ0])],"isStart":true})]})]});}
            var Q3;
            {var subQ0=sQuery(id+"F6.wireOp",EDGE,"E27.left");var subQ1=sQuery(id+"F6.wireOp",EDGE,"E27.bottom");var subQ2=sQuery(id+"F6.wireOp",EDGE,"E25");var subQ3=sQuery(id+"F2.wireOp",EDGE,"E24");var subQ4=sQuery(id+"F0.wireOp",EDGE,"E13");Q3=makeQuery(id+"F8.opFillet","BLEND_EDGE",EDGE,{"blendedFrom":[makeQuery(id+"F7.opExtrude","SWEPT_EDGE",EDGE,{"disambiguationData":[OSD([subQ1,subQ0])]}),makeQuery(id+"F7.boolean.opBoolean","MERGE",FACE,{"derivedFrom":[makeQuery(id+"F4.boolean.opBoolean","MERGE",FACE,{"derivedFrom":[makeQuery(id+"F1.opExtrude","SWEPT_FACE",FACE,{"disambiguationData":[OSD([subQ4])]}),makeQuery(id+"F4.opExtrude","SWEPT_FACE",FACE,{"disambiguationData":[OSD([subQ4])]})]}),makeQuery(id+"F7.opExtrude","CAP_FACE",FACE,{"disambiguationData":[OSD([subQ4,subQ3,subQ2,sQuery(id+"F6.wireOp",EDGE,"E26.bottom"),sQuery(id+"F6.wireOp",EDGE,"E26.top"),sQuery(id+"F6.wireOp",EDGE,"E26.left")])],"isStart":true}),makeQuery(id+"F7.opExtrude","CAP_FACE",FACE,{"disambiguationData":[OSD([subQ4,subQ3,subQ2,subQ1,sQuery(id+"F6.wireOp",EDGE,"E27.top"),subQ0])],"isStart":true})]})],"blendedInto":[makeQuery(id+"F7.boolean.opBoolean","MERGE",FACE,{"derivedFrom":[makeQuery(id+"F4.boolean.opBoolean","MERGE",FACE,{"derivedFrom":[makeQuery(id+"F1.opExtrude","SWEPT_FACE",FACE,{"disambiguationData":[OSD([subQ4])]}),makeQuery(id+"F4.opExtrude","SWEPT_FACE",FACE,{"disambiguationData":[OSD([subQ4])]})]}),makeQuery(id+"F7.opExtrude","CAP_FACE",FACE,{"disambiguationData":[OSD([subQ4,subQ3,subQ2,sQuery(id+"F6.wireOp",EDGE,"E26.bottom"),sQuery(id+"F6.wireOp",EDGE,"E26.top"),sQuery(id+"F6.wireOp",EDGE,"E26.left")])],"isStart":true}),makeQuery(id+"F7.opExtrude","CAP_FACE",FACE,{"disambiguationData":[OSD([subQ4,subQ3,subQ2,subQ1,sQuery(id+"F6.wireOp",EDGE,"E27.top"),subQ0])],"isStart":true})]})]});}
            var Q4;
            {var subQ0=sQuery(id+"F0.wireOp",EDGE,"E13");var subQ1=sQuery(id+"F2.wireOp",EDGE,"E24");var subQ4=sQuery(id+"F6.wireOp",EDGE,"E26.top");Q4=makeQuery(id+"F7.boolean.opBoolean","SPLIT",EDGE,{"disambiguationData":[TD([makeQuery(id+"F7.opExtrude","SWEPT_FACE",FACE,{"disambiguationData":[OSD([subQ4])]})])],"derivedFrom":makeQuery(id+"F4.boolean.opBoolean","MERGE",EDGE,{"derivedFrom":[makeQuery(id+"F3.boolean.opBoolean","COPY",EDGE,{"derivedFrom":makeQuery(id+"F3.opExtrude","SWEPT_EDGE",EDGE,{"disambiguationData":[OSD([subQ0,subQ1])]})}),makeQuery(id+"F4.opExtrude","SWEPT_EDGE",EDGE,{"disambiguationData":[OSD([subQ0,subQ1])]})]})});}
            var Q5;
            {var subQ0=sQuery(id+"F0.wireOp",EDGE,"E13");Q5=makeQuery(id+"F4.boolean.opBoolean","MERGE",EDGE,{"derivedFrom":[makeQuery(id+"F1.opExtrude","SWEPT_EDGE",EDGE,{"disambiguationData":[OSD([sQuery(id+"F0.wireOp",EDGE,"E12.trimOffspring"),subQ0])]}),makeQuery(id+"F4.opExtrude","SWEPT_EDGE",EDGE,{"disambiguationData":[OSD([subQ0,sQuery(id+"F2.wireOp",EDGE,"E23")])]})]});}
            var Q6;
            {var subQ0=sQuery(id+"F6.wireOp",EDGE,"E25");var subQ1=sQuery(id+"F2.wireOp",EDGE,"E24");var subQ2=sQuery(id+"F0.wireOp",EDGE,"E13");var subQ3=sQuery(id+"F6.wireOp",EDGE,"E26.left");var subQ4=sQuery(id+"F6.wireOp",EDGE,"E26.top");Q6=makeQuery(id+"F8.opFillet","BLEND_EDGE",EDGE,{"blendedFrom":[makeQuery(id+"F7.opExtrude","SWEPT_EDGE",EDGE,{"disambiguationData":[OSD([subQ4,subQ3])]}),makeQuery(id+"F7.boolean.opBoolean","MERGE",FACE,{"derivedFrom":[makeQuery(id+"F4.boolean.opBoolean","MERGE",FACE,{"derivedFrom":[makeQuery(id+"F1.opExtrude","SWEPT_FACE",FACE,{"disambiguationData":[OSD([subQ2])]}),makeQuery(id+"F4.opExtrude","SWEPT_FACE",FACE,{"disambiguationData":[OSD([subQ2])]})]}),makeQuery(id+"F7.opExtrude","CAP_FACE",FACE,{"disambiguationData":[OSD([subQ2,subQ1,subQ0,sQuery(id+"F6.wireOp",EDGE,"E26.bottom"),subQ4,subQ3])],"isStart":true}),makeQuery(id+"F7.opExtrude","CAP_FACE",FACE,{"disambiguationData":[OSD([subQ2,subQ1,subQ0,sQuery(id+"F6.wireOp",EDGE,"E27.bottom"),sQuery(id+"F6.wireOp",EDGE,"E27.top"),sQuery(id+"F6.wireOp",EDGE,"E27.left")])],"isStart":true})]})],"blendedInto":[makeQuery(id+"F7.boolean.opBoolean","MERGE",FACE,{"derivedFrom":[makeQuery(id+"F4.boolean.opBoolean","MERGE",FACE,{"derivedFrom":[makeQuery(id+"F1.opExtrude","SWEPT_FACE",FACE,{"disambiguationData":[OSD([subQ2])]}),makeQuery(id+"F4.opExtrude","SWEPT_FACE",FACE,{"disambiguationData":[OSD([subQ2])]})]}),makeQuery(id+"F7.opExtrude","CAP_FACE",FACE,{"disambiguationData":[OSD([subQ2,subQ1,subQ0,sQuery(id+"F6.wireOp",EDGE,"E26.bottom"),subQ4,subQ3])],"isStart":true}),makeQuery(id+"F7.opExtrude","CAP_FACE",FACE,{"disambiguationData":[OSD([subQ2,subQ1,subQ0,sQuery(id+"F6.wireOp",EDGE,"E27.bottom"),sQuery(id+"F6.wireOp",EDGE,"E27.top"),sQuery(id+"F6.wireOp",EDGE,"E27.left")])],"isStart":true})]})]});}
            var Q7;
            {var subQ0=sQuery(id+"F6.wireOp",EDGE,"E25");var subQ1=sQuery(id+"F2.wireOp",EDGE,"E24");var subQ2=sQuery(id+"F0.wireOp",EDGE,"E13");var subQ3=sQuery(id+"F6.wireOp",EDGE,"E26.left");var subQ4=sQuery(id+"F6.wireOp",EDGE,"E26.bottom");Q7=makeQuery(id+"F8.opFillet","BLEND_EDGE",EDGE,{"blendedFrom":[makeQuery(id+"F7.opExtrude","SWEPT_EDGE",EDGE,{"disambiguationData":[OSD([subQ4,subQ3])]}),makeQuery(id+"F7.boolean.opBoolean","MERGE",FACE,{"derivedFrom":[makeQuery(id+"F4.boolean.opBoolean","MERGE",FACE,{"derivedFrom":[makeQuery(id+"F1.opExtrude","SWEPT_FACE",FACE,{"disambiguationData":[OSD([subQ2])]}),makeQuery(id+"F4.opExtrude","SWEPT_FACE",FACE,{"disambiguationData":[OSD([subQ2])]})]}),makeQuery(id+"F7.opExtrude","CAP_FACE",FACE,{"disambiguationData":[OSD([subQ2,subQ1,subQ0,subQ4,sQuery(id+"F6.wireOp",EDGE,"E26.top"),subQ3])],"isStart":true}),makeQuery(id+"F7.opExtrude","CAP_FACE",FACE,{"disambiguationData":[OSD([subQ2,subQ1,subQ0,sQuery(id+"F6.wireOp",EDGE,"E27.bottom"),sQuery(id+"F6.wireOp",EDGE,"E27.top"),sQuery(id+"F6.wireOp",EDGE,"E27.left")])],"isStart":true})]})],"blendedInto":[makeQuery(id+"F7.boolean.opBoolean","MERGE",FACE,{"derivedFrom":[makeQuery(id+"F4.boolean.opBoolean","MERGE",FACE,{"derivedFrom":[makeQuery(id+"F1.opExtrude","SWEPT_FACE",FACE,{"disambiguationData":[OSD([subQ2])]}),makeQuery(id+"F4.opExtrude","SWEPT_FACE",FACE,{"disambiguationData":[OSD([subQ2])]})]}),makeQuery(id+"F7.opExtrude","CAP_FACE",FACE,{"disambiguationData":[OSD([subQ2,subQ1,subQ0,subQ4,sQuery(id+"F6.wireOp",EDGE,"E26.top"),subQ3])],"isStart":true}),makeQuery(id+"F7.opExtrude","CAP_FACE",FACE,{"disambiguationData":[OSD([subQ2,subQ1,subQ0,sQuery(id+"F6.wireOp",EDGE,"E27.bottom"),sQuery(id+"F6.wireOp",EDGE,"E27.top"),sQuery(id+"F6.wireOp",EDGE,"E27.left")])],"isStart":true})]})]});}
            var Q8;
            {var subQ0=sQuery(id+"F2.wireOp",EDGE,"E24");var subQ1=sQuery(id+"F0.wireOp",EDGE,"E13");var subQ3=sQuery(id+"F6.wireOp",EDGE,"E26.bottom");Q8=makeQuery(id+"F7.boolean.opBoolean","SPLIT",EDGE,{"disambiguationData":[TD([makeQuery(id+"F7.opExtrude","SWEPT_FACE",FACE,{"disambiguationData":[OSD([subQ3])]})])],"derivedFrom":makeQuery(id+"F4.boolean.opBoolean","MERGE",EDGE,{"derivedFrom":[makeQuery(id+"F3.boolean.opBoolean","COPY",EDGE,{"derivedFrom":makeQuery(id+"F3.opExtrude","SWEPT_EDGE",EDGE,{"disambiguationData":[OSD([subQ1,subQ0])]})}),makeQuery(id+"F4.opExtrude","SWEPT_EDGE",EDGE,{"disambiguationData":[OSD([subQ1,subQ0])]})]})});}
            var Q9;
            Q9=makeQuery(id+"F3.boolean.opBoolean","COPY",EDGE,{"derivedFrom":makeQuery(id+"F3.opExtrude","CAP_EDGE",EDGE,{"disambiguationData":[OSD([sQuery(id+"F0.wireOp",EDGE,"E13")])],"isStart":false})});
            var Q10;
            {var subQ0=sQuery(id+"F0.wireOp",EDGE,"E14");Q10=makeQuery(id+"F4.boolean.opBoolean","MERGE",EDGE,{"derivedFrom":[makeQuery(id+"F1.opExtrude","SWEPT_EDGE",EDGE,{"disambiguationData":[OSD([sQuery(id+"F0.wireOp",EDGE,"E0.0"),subQ0])]}),makeQuery(id+"F4.opExtrude","SWEPT_EDGE",EDGE,{"disambiguationData":[OSD([subQ0,sQuery(id+"F2.wireOp",EDGE,"E23")])]})]});}
            var Q11;
            {var subQ0=sQuery(id+"F2.wireOp",EDGE,"E24");var subQ1=sQuery(id+"F0.wireOp",EDGE,"E14");var subQ3=sQuery(id+"F6.wireOp",EDGE,"E27.top");Q11=makeQuery(id+"F7.boolean.opBoolean","SPLIT",EDGE,{"disambiguationData":[TD([makeQuery(id+"F7.opExtrude","SWEPT_FACE",FACE,{"disambiguationData":[OSD([subQ3])]})])],"derivedFrom":makeQuery(id+"F4.boolean.opBoolean","MERGE",EDGE,{"derivedFrom":[makeQuery(id+"F3.boolean.opBoolean","COPY",EDGE,{"derivedFrom":makeQuery(id+"F3.opExtrude","SWEPT_EDGE",EDGE,{"disambiguationData":[OSD([subQ1,subQ0])]})}),makeQuery(id+"F4.opExtrude","SWEPT_EDGE",EDGE,{"disambiguationData":[OSD([subQ1,subQ0])]})]})});}
            var Q12;
            {var subQ0=sQuery(id+"F6.wireOp",EDGE,"E27.left");var subQ1=sQuery(id+"F6.wireOp",EDGE,"E27.top");var subQ2=sQuery(id+"F6.wireOp",EDGE,"E25");var subQ3=sQuery(id+"F2.wireOp",EDGE,"E24");var subQ4=sQuery(id+"F0.wireOp",EDGE,"E13");var subQ5=sQuery(id+"F0.wireOp",EDGE,"E14");Q12=makeQuery(id+"F8.opFillet","BLEND_EDGE",EDGE,{"blendedFrom":[makeQuery(id+"F7.opExtrude","SWEPT_EDGE",EDGE,{"disambiguationData":[OSD([subQ1,subQ0])]}),makeQuery(id+"F7.boolean.opBoolean","MERGE",FACE,{"derivedFrom":[makeQuery(id+"F4.boolean.opBoolean","MERGE",FACE,{"derivedFrom":[makeQuery(id+"F1.opExtrude","SWEPT_FACE",FACE,{"disambiguationData":[OSD([subQ5])]}),makeQuery(id+"F4.opExtrude","SWEPT_FACE",FACE,{"disambiguationData":[OSD([subQ5])]})]}),makeQuery(id+"F7.opExtrude","CAP_FACE",FACE,{"disambiguationData":[OSD([subQ5]),ownerDisambiguation([makeQuery(id+"F7.opExtrude","SWEPT_BODY",BODY,{"disambiguationData":[OSD([subQ4,subQ3,subQ2,sQuery(id+"F6.wireOp",EDGE,"E26.bottom"),sQuery(id+"F6.wireOp",EDGE,"E26.top"),sQuery(id+"F6.wireOp",EDGE,"E26.left")])]})])],"isStart":false}),makeQuery(id+"F7.opExtrude","CAP_FACE",FACE,{"disambiguationData":[OSD([subQ5]),ownerDisambiguation([makeQuery(id+"F7.opExtrude","SWEPT_BODY",BODY,{"disambiguationData":[OSD([subQ4,subQ3,subQ2,sQuery(id+"F6.wireOp",EDGE,"E27.bottom"),subQ1,subQ0])]})])],"isStart":false})]})],"blendedInto":[makeQuery(id+"F7.boolean.opBoolean","MERGE",FACE,{"derivedFrom":[makeQuery(id+"F4.boolean.opBoolean","MERGE",FACE,{"derivedFrom":[makeQuery(id+"F1.opExtrude","SWEPT_FACE",FACE,{"disambiguationData":[OSD([subQ5])]}),makeQuery(id+"F4.opExtrude","SWEPT_FACE",FACE,{"disambiguationData":[OSD([subQ5])]})]}),makeQuery(id+"F7.opExtrude","CAP_FACE",FACE,{"disambiguationData":[OSD([subQ5]),ownerDisambiguation([makeQuery(id+"F7.opExtrude","SWEPT_BODY",BODY,{"disambiguationData":[OSD([subQ4,subQ3,subQ2,sQuery(id+"F6.wireOp",EDGE,"E26.bottom"),sQuery(id+"F6.wireOp",EDGE,"E26.top"),sQuery(id+"F6.wireOp",EDGE,"E26.left")])]})])],"isStart":false}),makeQuery(id+"F7.opExtrude","CAP_FACE",FACE,{"disambiguationData":[OSD([subQ5]),ownerDisambiguation([makeQuery(id+"F7.opExtrude","SWEPT_BODY",BODY,{"disambiguationData":[OSD([subQ4,subQ3,subQ2,sQuery(id+"F6.wireOp",EDGE,"E27.bottom"),subQ1,subQ0])]})])],"isStart":false})]})]});}
            var Q13;
            {var subQ0=sQuery(id+"F6.wireOp",EDGE,"E27.left");var subQ1=sQuery(id+"F6.wireOp",EDGE,"E27.bottom");var subQ2=sQuery(id+"F6.wireOp",EDGE,"E25");var subQ3=sQuery(id+"F2.wireOp",EDGE,"E24");var subQ4=sQuery(id+"F0.wireOp",EDGE,"E13");var subQ5=sQuery(id+"F0.wireOp",EDGE,"E14");Q13=makeQuery(id+"F8.opFillet","BLEND_EDGE",EDGE,{"blendedFrom":[makeQuery(id+"F7.opExtrude","SWEPT_EDGE",EDGE,{"disambiguationData":[OSD([subQ1,subQ0])]}),makeQuery(id+"F7.boolean.opBoolean","MERGE",FACE,{"derivedFrom":[makeQuery(id+"F4.boolean.opBoolean","MERGE",FACE,{"derivedFrom":[makeQuery(id+"F1.opExtrude","SWEPT_FACE",FACE,{"disambiguationData":[OSD([subQ5])]}),makeQuery(id+"F4.opExtrude","SWEPT_FACE",FACE,{"disambiguationData":[OSD([subQ5])]})]}),makeQuery(id+"F7.opExtrude","CAP_FACE",FACE,{"disambiguationData":[OSD([subQ5]),ownerDisambiguation([makeQuery(id+"F7.opExtrude","SWEPT_BODY",BODY,{"disambiguationData":[OSD([subQ4,subQ3,subQ2,sQuery(id+"F6.wireOp",EDGE,"E26.bottom"),sQuery(id+"F6.wireOp",EDGE,"E26.top"),sQuery(id+"F6.wireOp",EDGE,"E26.left")])]})])],"isStart":false}),makeQuery(id+"F7.opExtrude","CAP_FACE",FACE,{"disambiguationData":[OSD([subQ5]),ownerDisambiguation([makeQuery(id+"F7.opExtrude","SWEPT_BODY",BODY,{"disambiguationData":[OSD([subQ4,subQ3,subQ2,subQ1,sQuery(id+"F6.wireOp",EDGE,"E27.top"),subQ0])]})])],"isStart":false})]})],"blendedInto":[makeQuery(id+"F7.boolean.opBoolean","MERGE",FACE,{"derivedFrom":[makeQuery(id+"F4.boolean.opBoolean","MERGE",FACE,{"derivedFrom":[makeQuery(id+"F1.opExtrude","SWEPT_FACE",FACE,{"disambiguationData":[OSD([subQ5])]}),makeQuery(id+"F4.opExtrude","SWEPT_FACE",FACE,{"disambiguationData":[OSD([subQ5])]})]}),makeQuery(id+"F7.opExtrude","CAP_FACE",FACE,{"disambiguationData":[OSD([subQ5]),ownerDisambiguation([makeQuery(id+"F7.opExtrude","SWEPT_BODY",BODY,{"disambiguationData":[OSD([subQ4,subQ3,subQ2,sQuery(id+"F6.wireOp",EDGE,"E26.bottom"),sQuery(id+"F6.wireOp",EDGE,"E26.top"),sQuery(id+"F6.wireOp",EDGE,"E26.left")])]})])],"isStart":false}),makeQuery(id+"F7.opExtrude","CAP_FACE",FACE,{"disambiguationData":[OSD([subQ5]),ownerDisambiguation([makeQuery(id+"F7.opExtrude","SWEPT_BODY",BODY,{"disambiguationData":[OSD([subQ4,subQ3,subQ2,subQ1,sQuery(id+"F6.wireOp",EDGE,"E27.top"),subQ0])]})])],"isStart":false})]})]});}
            var Q14;
            {var subQ0=sQuery(id+"F0.wireOp",EDGE,"E14");var subQ3=sQuery(id+"F2.wireOp",EDGE,"E24");var subQ5=sQuery(id+"F6.wireOp",EDGE,"E26.top");Q14=makeQuery(id+"F7.boolean.opBoolean","SPLIT",EDGE,{"disambiguationData":[TD([makeQuery(id+"F7.opExtrude","SWEPT_FACE",FACE,{"disambiguationData":[OSD([subQ5])]})])],"derivedFrom":makeQuery(id+"F4.boolean.opBoolean","MERGE",EDGE,{"derivedFrom":[makeQuery(id+"F3.boolean.opBoolean","COPY",EDGE,{"derivedFrom":makeQuery(id+"F3.opExtrude","SWEPT_EDGE",EDGE,{"disambiguationData":[OSD([subQ0,subQ3])]})}),makeQuery(id+"F4.opExtrude","SWEPT_EDGE",EDGE,{"disambiguationData":[OSD([subQ0,subQ3])]})]})});}
            var Q15;
            {var subQ0=sQuery(id+"F6.wireOp",EDGE,"E25");var subQ1=sQuery(id+"F2.wireOp",EDGE,"E24");var subQ2=sQuery(id+"F0.wireOp",EDGE,"E13");var subQ3=sQuery(id+"F0.wireOp",EDGE,"E14");var subQ4=sQuery(id+"F6.wireOp",EDGE,"E26.left");var subQ5=sQuery(id+"F6.wireOp",EDGE,"E26.top");Q15=makeQuery(id+"F8.opFillet","BLEND_EDGE",EDGE,{"blendedFrom":[makeQuery(id+"F7.opExtrude","SWEPT_EDGE",EDGE,{"disambiguationData":[OSD([subQ5,subQ4])]}),makeQuery(id+"F7.boolean.opBoolean","MERGE",FACE,{"derivedFrom":[makeQuery(id+"F4.boolean.opBoolean","MERGE",FACE,{"derivedFrom":[makeQuery(id+"F1.opExtrude","SWEPT_FACE",FACE,{"disambiguationData":[OSD([subQ3])]}),makeQuery(id+"F4.opExtrude","SWEPT_FACE",FACE,{"disambiguationData":[OSD([subQ3])]})]}),makeQuery(id+"F7.opExtrude","CAP_FACE",FACE,{"disambiguationData":[OSD([subQ3]),ownerDisambiguation([makeQuery(id+"F7.opExtrude","SWEPT_BODY",BODY,{"disambiguationData":[OSD([subQ2,subQ1,subQ0,sQuery(id+"F6.wireOp",EDGE,"E26.bottom"),subQ5,subQ4])]})])],"isStart":false}),makeQuery(id+"F7.opExtrude","CAP_FACE",FACE,{"disambiguationData":[OSD([subQ3]),ownerDisambiguation([makeQuery(id+"F7.opExtrude","SWEPT_BODY",BODY,{"disambiguationData":[OSD([subQ2,subQ1,subQ0,sQuery(id+"F6.wireOp",EDGE,"E27.bottom"),sQuery(id+"F6.wireOp",EDGE,"E27.top"),sQuery(id+"F6.wireOp",EDGE,"E27.left")])]})])],"isStart":false})]})],"blendedInto":[makeQuery(id+"F7.boolean.opBoolean","MERGE",FACE,{"derivedFrom":[makeQuery(id+"F4.boolean.opBoolean","MERGE",FACE,{"derivedFrom":[makeQuery(id+"F1.opExtrude","SWEPT_FACE",FACE,{"disambiguationData":[OSD([subQ3])]}),makeQuery(id+"F4.opExtrude","SWEPT_FACE",FACE,{"disambiguationData":[OSD([subQ3])]})]}),makeQuery(id+"F7.opExtrude","CAP_FACE",FACE,{"disambiguationData":[OSD([subQ3]),ownerDisambiguation([makeQuery(id+"F7.opExtrude","SWEPT_BODY",BODY,{"disambiguationData":[OSD([subQ2,subQ1,subQ0,sQuery(id+"F6.wireOp",EDGE,"E26.bottom"),subQ5,subQ4])]})])],"isStart":false}),makeQuery(id+"F7.opExtrude","CAP_FACE",FACE,{"disambiguationData":[OSD([subQ3]),ownerDisambiguation([makeQuery(id+"F7.opExtrude","SWEPT_BODY",BODY,{"disambiguationData":[OSD([subQ2,subQ1,subQ0,sQuery(id+"F6.wireOp",EDGE,"E27.bottom"),sQuery(id+"F6.wireOp",EDGE,"E27.top"),sQuery(id+"F6.wireOp",EDGE,"E27.left")])]})])],"isStart":false})]})]});}
            var Q16;
            {var subQ0=sQuery(id+"F6.wireOp",EDGE,"E25");var subQ1=sQuery(id+"F2.wireOp",EDGE,"E24");var subQ2=sQuery(id+"F0.wireOp",EDGE,"E13");var subQ3=sQuery(id+"F0.wireOp",EDGE,"E14");var subQ4=sQuery(id+"F6.wireOp",EDGE,"E26.left");var subQ5=sQuery(id+"F6.wireOp",EDGE,"E26.bottom");Q16=makeQuery(id+"F8.opFillet","BLEND_EDGE",EDGE,{"blendedFrom":[makeQuery(id+"F7.opExtrude","SWEPT_EDGE",EDGE,{"disambiguationData":[OSD([subQ5,subQ4])]}),makeQuery(id+"F7.boolean.opBoolean","MERGE",FACE,{"derivedFrom":[makeQuery(id+"F4.boolean.opBoolean","MERGE",FACE,{"derivedFrom":[makeQuery(id+"F1.opExtrude","SWEPT_FACE",FACE,{"disambiguationData":[OSD([subQ3])]}),makeQuery(id+"F4.opExtrude","SWEPT_FACE",FACE,{"disambiguationData":[OSD([subQ3])]})]}),makeQuery(id+"F7.opExtrude","CAP_FACE",FACE,{"disambiguationData":[OSD([subQ3]),ownerDisambiguation([makeQuery(id+"F7.opExtrude","SWEPT_BODY",BODY,{"disambiguationData":[OSD([subQ2,subQ1,subQ0,subQ5,sQuery(id+"F6.wireOp",EDGE,"E26.top"),subQ4])]})])],"isStart":false}),makeQuery(id+"F7.opExtrude","CAP_FACE",FACE,{"disambiguationData":[OSD([subQ3]),ownerDisambiguation([makeQuery(id+"F7.opExtrude","SWEPT_BODY",BODY,{"disambiguationData":[OSD([subQ2,subQ1,subQ0,sQuery(id+"F6.wireOp",EDGE,"E27.bottom"),sQuery(id+"F6.wireOp",EDGE,"E27.top"),sQuery(id+"F6.wireOp",EDGE,"E27.left")])]})])],"isStart":false})]})],"blendedInto":[makeQuery(id+"F7.boolean.opBoolean","MERGE",FACE,{"derivedFrom":[makeQuery(id+"F4.boolean.opBoolean","MERGE",FACE,{"derivedFrom":[makeQuery(id+"F1.opExtrude","SWEPT_FACE",FACE,{"disambiguationData":[OSD([subQ3])]}),makeQuery(id+"F4.opExtrude","SWEPT_FACE",FACE,{"disambiguationData":[OSD([subQ3])]})]}),makeQuery(id+"F7.opExtrude","CAP_FACE",FACE,{"disambiguationData":[OSD([subQ3]),ownerDisambiguation([makeQuery(id+"F7.opExtrude","SWEPT_BODY",BODY,{"disambiguationData":[OSD([subQ2,subQ1,subQ0,subQ5,sQuery(id+"F6.wireOp",EDGE,"E26.top"),subQ4])]})])],"isStart":false}),makeQuery(id+"F7.opExtrude","CAP_FACE",FACE,{"disambiguationData":[OSD([subQ3]),ownerDisambiguation([makeQuery(id+"F7.opExtrude","SWEPT_BODY",BODY,{"disambiguationData":[OSD([subQ2,subQ1,subQ0,sQuery(id+"F6.wireOp",EDGE,"E27.bottom"),sQuery(id+"F6.wireOp",EDGE,"E27.top"),sQuery(id+"F6.wireOp",EDGE,"E27.left")])]})])],"isStart":false})]})]});}
            var Q17;
            {var subQ0=sQuery(id+"F2.wireOp",EDGE,"E24");var subQ1=sQuery(id+"F0.wireOp",EDGE,"E14");var subQ3=sQuery(id+"F6.wireOp",EDGE,"E26.bottom");Q17=makeQuery(id+"F7.boolean.opBoolean","SPLIT",EDGE,{"disambiguationData":[TD([makeQuery(id+"F7.opExtrude","SWEPT_FACE",FACE,{"disambiguationData":[OSD([subQ3])]})])],"derivedFrom":makeQuery(id+"F4.boolean.opBoolean","MERGE",EDGE,{"derivedFrom":[makeQuery(id+"F3.boolean.opBoolean","COPY",EDGE,{"derivedFrom":makeQuery(id+"F3.opExtrude","SWEPT_EDGE",EDGE,{"disambiguationData":[OSD([subQ1,subQ0])]})}),makeQuery(id+"F4.opExtrude","SWEPT_EDGE",EDGE,{"disambiguationData":[OSD([subQ1,subQ0])]})]})});}
            var Q18;
            Q18=makeQuery(id+"F3.boolean.opBoolean","COPY",EDGE,{"derivedFrom":makeQuery(id+"F3.opExtrude","CAP_EDGE",EDGE,{"disambiguationData":[OSD([sQuery(id+"F0.wireOp",EDGE,"E14")])],"isStart":false})});
            fillet(context, id + "F9", {"entities" : qUnion([Q0, Q1, Q2, Q3, Q4, Q5, Q6, Q7, Q8, Q9, Q10, Q11, Q12, Q13, Q14, Q15, Q16, Q17, Q18]), "radius" : 1 * mm, "tangentPropagation" : true, "allowEdgeOverflow" : false});
        }
        {
            var Q0;
            Q0=makeQuery(id+"F1.opExtrude","CAP_EDGE",EDGE,{"disambiguationData":[OSD([sQuery(id+"F0.wireOp",EDGE,"E2")])],"isStart":false});
            var Q1;
            {var subQ0=sQuery(id+"F0.wireOp",EDGE,"E8.trimOffspring");var subQ1=sQuery(id+"F0.wireOp",EDGE,"E0.0");var subQ2=sQuery(id+"F0.wireOp",EDGE,"E10.trimOffspring");var subQ3=sQuery(id+"F0.wireOp",EDGE,"E5");var subQ4=sQuery(id+"F0.wireOp",EDGE,"E9.trimOffspring");var subQ5=sQuery(id+"F0.wireOp",EDGE,"E4");var subQ6=sQuery(id+"F0.wireOp",EDGE,"E1");var subQ7=sQuery(id+"F0.wireOp",EDGE,"E2");var subQ8=sQuery(id+"F0.wireOp",EDGE,"E12.trimOffspring");var subQ9=sQuery(id+"F0.wireOp",EDGE,"E7.trimOffspring");var subQ10=sQuery(id+"F0.wireOp",EDGE,"E3");var subQ11=sQuery(id+"F0.wireOp",EDGE,"E11.trimOffspring");var subQ12=sQuery(id+"F0.wireOp",EDGE,"E15.trimOffspring");Q1=makeQuery(id+"F5.opFillet","BLEND_EDGE",EDGE,{"blendedFrom":[makeQuery(id+"F1.opExtrude","SWEPT_EDGE",EDGE,{"disambiguationData":[OSD([subQ7,subQ5])]}),makeQuery(id+"F4.boolean.opBoolean","SPLIT",FACE,{"disambiguationData":[TD([makeQuery(id+"F1.opExtrude","SWEPT_FACE",FACE,{"disambiguationData":[OSD([subQ7])]})])],"derivedFrom":makeQuery(id+"F1.opExtrude","CAP_FACE",FACE,{"disambiguationData":[OSD([subQ1,subQ6,subQ7,subQ10,subQ5,subQ3,sQuery(id+"F0.wireOp",EDGE,"E6.1.0.0"),sQuery(id+"F0.wireOp",EDGE,"E6.1.0.1"),sQuery(id+"F0.wireOp",EDGE,"E6.1.0.2"),sQuery(id+"F0.wireOp",EDGE,"E6.1.0.3"),sQuery(id+"F0.wireOp",EDGE,"E6.2.0.0"),sQuery(id+"F0.wireOp",EDGE,"E6.2.0.1"),sQuery(id+"F0.wireOp",EDGE,"E6.2.0.2"),sQuery(id+"F0.wireOp",EDGE,"E6.2.0.3"),sQuery(id+"F0.wireOp",EDGE,"E6.3.0.0"),sQuery(id+"F0.wireOp",EDGE,"E6.3.0.1"),sQuery(id+"F0.wireOp",EDGE,"E6.3.0.2"),sQuery(id+"F0.wireOp",EDGE,"E6.3.0.3"),sQuery(id+"F0.wireOp",EDGE,"E6.4.0.0"),sQuery(id+"F0.wireOp",EDGE,"E6.4.0.1"),sQuery(id+"F0.wireOp",EDGE,"E6.4.0.2"),sQuery(id+"F0.wireOp",EDGE,"E6.4.0.3"),sQuery(id+"F0.wireOp",EDGE,"E6.5.0.0"),sQuery(id+"F0.wireOp",EDGE,"E6.5.0.1"),sQuery(id+"F0.wireOp",EDGE,"E6.5.0.2"),sQuery(id+"F0.wireOp",EDGE,"E6.5.0.3"),sQuery(id+"F0.wireOp",EDGE,"E6.6.0.0"),sQuery(id+"F0.wireOp",EDGE,"E6.6.0.1"),sQuery(id+"F0.wireOp",EDGE,"E6.6.0.2"),sQuery(id+"F0.wireOp",EDGE,"E6.6.0.3"),subQ9,subQ0,subQ4,subQ2,subQ11,subQ8,sQuery(id+"F0.wireOp",EDGE,"E13"),sQuery(id+"F0.wireOp",EDGE,"E14"),subQ12,sQuery(id+"F0.wireOp",EDGE,"E16.trimOffspring"),sQuery(id+"F0.wireOp",EDGE,"E17.trimOffspring"),sQuery(id+"F0.wireOp",EDGE,"E18.trimOffspring"),sQuery(id+"F0.wireOp",EDGE,"E19.trimOffspring"),sQuery(id+"F0.wireOp",EDGE,"E20.trimOffspring"),sQuery(id+"F0.wireOp",EDGE,"E21.trimOffspring"),sQuery(id+"F0.wireOp",EDGE,"E22")])],"isStart":false})})],"blendedInto":[makeQuery(id+"F4.boolean.opBoolean","SPLIT",FACE,{"disambiguationData":[TD([makeQuery(id+"F1.opExtrude","SWEPT_FACE",FACE,{"disambiguationData":[OSD([subQ7])]})])],"derivedFrom":makeQuery(id+"F1.opExtrude","CAP_FACE",FACE,{"disambiguationData":[OSD([subQ1,subQ6,subQ7,subQ10,subQ5,subQ3,sQuery(id+"F0.wireOp",EDGE,"E6.1.0.0"),sQuery(id+"F0.wireOp",EDGE,"E6.1.0.1"),sQuery(id+"F0.wireOp",EDGE,"E6.1.0.2"),sQuery(id+"F0.wireOp",EDGE,"E6.1.0.3"),sQuery(id+"F0.wireOp",EDGE,"E6.2.0.0"),sQuery(id+"F0.wireOp",EDGE,"E6.2.0.1"),sQuery(id+"F0.wireOp",EDGE,"E6.2.0.2"),sQuery(id+"F0.wireOp",EDGE,"E6.2.0.3"),sQuery(id+"F0.wireOp",EDGE,"E6.3.0.0"),sQuery(id+"F0.wireOp",EDGE,"E6.3.0.1"),sQuery(id+"F0.wireOp",EDGE,"E6.3.0.2"),sQuery(id+"F0.wireOp",EDGE,"E6.3.0.3"),sQuery(id+"F0.wireOp",EDGE,"E6.4.0.0"),sQuery(id+"F0.wireOp",EDGE,"E6.4.0.1"),sQuery(id+"F0.wireOp",EDGE,"E6.4.0.2"),sQuery(id+"F0.wireOp",EDGE,"E6.4.0.3"),sQuery(id+"F0.wireOp",EDGE,"E6.5.0.0"),sQuery(id+"F0.wireOp",EDGE,"E6.5.0.1"),sQuery(id+"F0.wireOp",EDGE,"E6.5.0.2"),sQuery(id+"F0.wireOp",EDGE,"E6.5.0.3"),sQuery(id+"F0.wireOp",EDGE,"E6.6.0.0"),sQuery(id+"F0.wireOp",EDGE,"E6.6.0.1"),sQuery(id+"F0.wireOp",EDGE,"E6.6.0.2"),sQuery(id+"F0.wireOp",EDGE,"E6.6.0.3"),subQ9,subQ0,subQ4,subQ2,subQ11,subQ8,sQuery(id+"F0.wireOp",EDGE,"E13"),sQuery(id+"F0.wireOp",EDGE,"E14"),subQ12,sQuery(id+"F0.wireOp",EDGE,"E16.trimOffspring"),sQuery(id+"F0.wireOp",EDGE,"E17.trimOffspring"),sQuery(id+"F0.wireOp",EDGE,"E18.trimOffspring"),sQuery(id+"F0.wireOp",EDGE,"E19.trimOffspring"),sQuery(id+"F0.wireOp",EDGE,"E20.trimOffspring"),sQuery(id+"F0.wireOp",EDGE,"E21.trimOffspring"),sQuery(id+"F0.wireOp",EDGE,"E22")])],"isStart":false})})]});}
            var Q2;
            {var subQ0=sQuery(id+"F0.wireOp",EDGE,"E8.trimOffspring");var subQ1=sQuery(id+"F0.wireOp",EDGE,"E0.0");var subQ2=sQuery(id+"F0.wireOp",EDGE,"E10.trimOffspring");var subQ3=sQuery(id+"F0.wireOp",EDGE,"E5");var subQ4=sQuery(id+"F0.wireOp",EDGE,"E9.trimOffspring");var subQ5=sQuery(id+"F0.wireOp",EDGE,"E4");var subQ6=sQuery(id+"F0.wireOp",EDGE,"E1");var subQ7=sQuery(id+"F0.wireOp",EDGE,"E2");var subQ8=sQuery(id+"F0.wireOp",EDGE,"E12.trimOffspring");var subQ9=sQuery(id+"F0.wireOp",EDGE,"E7.trimOffspring");var subQ10=sQuery(id+"F0.wireOp",EDGE,"E3");var subQ11=sQuery(id+"F0.wireOp",EDGE,"E11.trimOffspring");var subQ12=sQuery(id+"F0.wireOp",EDGE,"E15.trimOffspring");Q2=makeQuery(id+"F5.opFillet","BLEND_EDGE",EDGE,{"blendedFrom":[makeQuery(id+"F1.opExtrude","SWEPT_EDGE",EDGE,{"disambiguationData":[OSD([subQ10,subQ5])]}),makeQuery(id+"F4.boolean.opBoolean","SPLIT",FACE,{"disambiguationData":[TD([makeQuery(id+"F1.opExtrude","SWEPT_FACE",FACE,{"disambiguationData":[OSD([subQ7])]})])],"derivedFrom":makeQuery(id+"F1.opExtrude","CAP_FACE",FACE,{"disambiguationData":[OSD([subQ1,subQ6,subQ7,subQ10,subQ5,subQ3,sQuery(id+"F0.wireOp",EDGE,"E6.1.0.0"),sQuery(id+"F0.wireOp",EDGE,"E6.1.0.1"),sQuery(id+"F0.wireOp",EDGE,"E6.1.0.2"),sQuery(id+"F0.wireOp",EDGE,"E6.1.0.3"),sQuery(id+"F0.wireOp",EDGE,"E6.2.0.0"),sQuery(id+"F0.wireOp",EDGE,"E6.2.0.1"),sQuery(id+"F0.wireOp",EDGE,"E6.2.0.2"),sQuery(id+"F0.wireOp",EDGE,"E6.2.0.3"),sQuery(id+"F0.wireOp",EDGE,"E6.3.0.0"),sQuery(id+"F0.wireOp",EDGE,"E6.3.0.1"),sQuery(id+"F0.wireOp",EDGE,"E6.3.0.2"),sQuery(id+"F0.wireOp",EDGE,"E6.3.0.3"),sQuery(id+"F0.wireOp",EDGE,"E6.4.0.0"),sQuery(id+"F0.wireOp",EDGE,"E6.4.0.1"),sQuery(id+"F0.wireOp",EDGE,"E6.4.0.2"),sQuery(id+"F0.wireOp",EDGE,"E6.4.0.3"),sQuery(id+"F0.wireOp",EDGE,"E6.5.0.0"),sQuery(id+"F0.wireOp",EDGE,"E6.5.0.1"),sQuery(id+"F0.wireOp",EDGE,"E6.5.0.2"),sQuery(id+"F0.wireOp",EDGE,"E6.5.0.3"),sQuery(id+"F0.wireOp",EDGE,"E6.6.0.0"),sQuery(id+"F0.wireOp",EDGE,"E6.6.0.1"),sQuery(id+"F0.wireOp",EDGE,"E6.6.0.2"),sQuery(id+"F0.wireOp",EDGE,"E6.6.0.3"),subQ9,subQ0,subQ4,subQ2,subQ11,subQ8,sQuery(id+"F0.wireOp",EDGE,"E13"),sQuery(id+"F0.wireOp",EDGE,"E14"),subQ12,sQuery(id+"F0.wireOp",EDGE,"E16.trimOffspring"),sQuery(id+"F0.wireOp",EDGE,"E17.trimOffspring"),sQuery(id+"F0.wireOp",EDGE,"E18.trimOffspring"),sQuery(id+"F0.wireOp",EDGE,"E19.trimOffspring"),sQuery(id+"F0.wireOp",EDGE,"E20.trimOffspring"),sQuery(id+"F0.wireOp",EDGE,"E21.trimOffspring"),sQuery(id+"F0.wireOp",EDGE,"E22")])],"isStart":false})})],"blendedInto":[makeQuery(id+"F4.boolean.opBoolean","SPLIT",FACE,{"disambiguationData":[TD([makeQuery(id+"F1.opExtrude","SWEPT_FACE",FACE,{"disambiguationData":[OSD([subQ7])]})])],"derivedFrom":makeQuery(id+"F1.opExtrude","CAP_FACE",FACE,{"disambiguationData":[OSD([subQ1,subQ6,subQ7,subQ10,subQ5,subQ3,sQuery(id+"F0.wireOp",EDGE,"E6.1.0.0"),sQuery(id+"F0.wireOp",EDGE,"E6.1.0.1"),sQuery(id+"F0.wireOp",EDGE,"E6.1.0.2"),sQuery(id+"F0.wireOp",EDGE,"E6.1.0.3"),sQuery(id+"F0.wireOp",EDGE,"E6.2.0.0"),sQuery(id+"F0.wireOp",EDGE,"E6.2.0.1"),sQuery(id+"F0.wireOp",EDGE,"E6.2.0.2"),sQuery(id+"F0.wireOp",EDGE,"E6.2.0.3"),sQuery(id+"F0.wireOp",EDGE,"E6.3.0.0"),sQuery(id+"F0.wireOp",EDGE,"E6.3.0.1"),sQuery(id+"F0.wireOp",EDGE,"E6.3.0.2"),sQuery(id+"F0.wireOp",EDGE,"E6.3.0.3"),sQuery(id+"F0.wireOp",EDGE,"E6.4.0.0"),sQuery(id+"F0.wireOp",EDGE,"E6.4.0.1"),sQuery(id+"F0.wireOp",EDGE,"E6.4.0.2"),sQuery(id+"F0.wireOp",EDGE,"E6.4.0.3"),sQuery(id+"F0.wireOp",EDGE,"E6.5.0.0"),sQuery(id+"F0.wireOp",EDGE,"E6.5.0.1"),sQuery(id+"F0.wireOp",EDGE,"E6.5.0.2"),sQuery(id+"F0.wireOp",EDGE,"E6.5.0.3"),sQuery(id+"F0.wireOp",EDGE,"E6.6.0.0"),sQuery(id+"F0.wireOp",EDGE,"E6.6.0.1"),sQuery(id+"F0.wireOp",EDGE,"E6.6.0.2"),sQuery(id+"F0.wireOp",EDGE,"E6.6.0.3"),subQ9,subQ0,subQ4,subQ2,subQ11,subQ8,sQuery(id+"F0.wireOp",EDGE,"E13"),sQuery(id+"F0.wireOp",EDGE,"E14"),subQ12,sQuery(id+"F0.wireOp",EDGE,"E16.trimOffspring"),sQuery(id+"F0.wireOp",EDGE,"E17.trimOffspring"),sQuery(id+"F0.wireOp",EDGE,"E18.trimOffspring"),sQuery(id+"F0.wireOp",EDGE,"E19.trimOffspring"),sQuery(id+"F0.wireOp",EDGE,"E20.trimOffspring"),sQuery(id+"F0.wireOp",EDGE,"E21.trimOffspring"),sQuery(id+"F0.wireOp",EDGE,"E22")])],"isStart":false})})]});}
            var Q3;
            Q3=makeQuery(id+"F1.opExtrude","CAP_EDGE",EDGE,{"disambiguationData":[OSD([sQuery(id+"F0.wireOp",EDGE,"E3")])],"isStart":false});
            var Q4;
            {var subQ0=sQuery(id+"F0.wireOp",EDGE,"E8.trimOffspring");var subQ1=sQuery(id+"F0.wireOp",EDGE,"E0.0");var subQ2=sQuery(id+"F0.wireOp",EDGE,"E10.trimOffspring");var subQ3=sQuery(id+"F0.wireOp",EDGE,"E5");var subQ4=sQuery(id+"F0.wireOp",EDGE,"E9.trimOffspring");var subQ5=sQuery(id+"F0.wireOp",EDGE,"E4");var subQ6=sQuery(id+"F0.wireOp",EDGE,"E1");var subQ7=sQuery(id+"F0.wireOp",EDGE,"E2");var subQ8=sQuery(id+"F0.wireOp",EDGE,"E12.trimOffspring");var subQ9=sQuery(id+"F0.wireOp",EDGE,"E7.trimOffspring");var subQ10=sQuery(id+"F0.wireOp",EDGE,"E3");var subQ11=sQuery(id+"F0.wireOp",EDGE,"E11.trimOffspring");var subQ12=sQuery(id+"F0.wireOp",EDGE,"E15.trimOffspring");Q4=makeQuery(id+"F5.opFillet","BLEND_EDGE",EDGE,{"blendedFrom":[makeQuery(id+"F1.opExtrude","SWEPT_EDGE",EDGE,{"disambiguationData":[OSD([subQ10,subQ3])]}),makeQuery(id+"F4.boolean.opBoolean","SPLIT",FACE,{"disambiguationData":[TD([makeQuery(id+"F1.opExtrude","SWEPT_FACE",FACE,{"disambiguationData":[OSD([subQ7])]})])],"derivedFrom":makeQuery(id+"F1.opExtrude","CAP_FACE",FACE,{"disambiguationData":[OSD([subQ1,subQ6,subQ7,subQ10,subQ5,subQ3,sQuery(id+"F0.wireOp",EDGE,"E6.1.0.0"),sQuery(id+"F0.wireOp",EDGE,"E6.1.0.1"),sQuery(id+"F0.wireOp",EDGE,"E6.1.0.2"),sQuery(id+"F0.wireOp",EDGE,"E6.1.0.3"),sQuery(id+"F0.wireOp",EDGE,"E6.2.0.0"),sQuery(id+"F0.wireOp",EDGE,"E6.2.0.1"),sQuery(id+"F0.wireOp",EDGE,"E6.2.0.2"),sQuery(id+"F0.wireOp",EDGE,"E6.2.0.3"),sQuery(id+"F0.wireOp",EDGE,"E6.3.0.0"),sQuery(id+"F0.wireOp",EDGE,"E6.3.0.1"),sQuery(id+"F0.wireOp",EDGE,"E6.3.0.2"),sQuery(id+"F0.wireOp",EDGE,"E6.3.0.3"),sQuery(id+"F0.wireOp",EDGE,"E6.4.0.0"),sQuery(id+"F0.wireOp",EDGE,"E6.4.0.1"),sQuery(id+"F0.wireOp",EDGE,"E6.4.0.2"),sQuery(id+"F0.wireOp",EDGE,"E6.4.0.3"),sQuery(id+"F0.wireOp",EDGE,"E6.5.0.0"),sQuery(id+"F0.wireOp",EDGE,"E6.5.0.1"),sQuery(id+"F0.wireOp",EDGE,"E6.5.0.2"),sQuery(id+"F0.wireOp",EDGE,"E6.5.0.3"),sQuery(id+"F0.wireOp",EDGE,"E6.6.0.0"),sQuery(id+"F0.wireOp",EDGE,"E6.6.0.1"),sQuery(id+"F0.wireOp",EDGE,"E6.6.0.2"),sQuery(id+"F0.wireOp",EDGE,"E6.6.0.3"),subQ9,subQ0,subQ4,subQ2,subQ11,subQ8,sQuery(id+"F0.wireOp",EDGE,"E13"),sQuery(id+"F0.wireOp",EDGE,"E14"),subQ12,sQuery(id+"F0.wireOp",EDGE,"E16.trimOffspring"),sQuery(id+"F0.wireOp",EDGE,"E17.trimOffspring"),sQuery(id+"F0.wireOp",EDGE,"E18.trimOffspring"),sQuery(id+"F0.wireOp",EDGE,"E19.trimOffspring"),sQuery(id+"F0.wireOp",EDGE,"E20.trimOffspring"),sQuery(id+"F0.wireOp",EDGE,"E21.trimOffspring"),sQuery(id+"F0.wireOp",EDGE,"E22")])],"isStart":false})})],"blendedInto":[makeQuery(id+"F4.boolean.opBoolean","SPLIT",FACE,{"disambiguationData":[TD([makeQuery(id+"F1.opExtrude","SWEPT_FACE",FACE,{"disambiguationData":[OSD([subQ7])]})])],"derivedFrom":makeQuery(id+"F1.opExtrude","CAP_FACE",FACE,{"disambiguationData":[OSD([subQ1,subQ6,subQ7,subQ10,subQ5,subQ3,sQuery(id+"F0.wireOp",EDGE,"E6.1.0.0"),sQuery(id+"F0.wireOp",EDGE,"E6.1.0.1"),sQuery(id+"F0.wireOp",EDGE,"E6.1.0.2"),sQuery(id+"F0.wireOp",EDGE,"E6.1.0.3"),sQuery(id+"F0.wireOp",EDGE,"E6.2.0.0"),sQuery(id+"F0.wireOp",EDGE,"E6.2.0.1"),sQuery(id+"F0.wireOp",EDGE,"E6.2.0.2"),sQuery(id+"F0.wireOp",EDGE,"E6.2.0.3"),sQuery(id+"F0.wireOp",EDGE,"E6.3.0.0"),sQuery(id+"F0.wireOp",EDGE,"E6.3.0.1"),sQuery(id+"F0.wireOp",EDGE,"E6.3.0.2"),sQuery(id+"F0.wireOp",EDGE,"E6.3.0.3"),sQuery(id+"F0.wireOp",EDGE,"E6.4.0.0"),sQuery(id+"F0.wireOp",EDGE,"E6.4.0.1"),sQuery(id+"F0.wireOp",EDGE,"E6.4.0.2"),sQuery(id+"F0.wireOp",EDGE,"E6.4.0.3"),sQuery(id+"F0.wireOp",EDGE,"E6.5.0.0"),sQuery(id+"F0.wireOp",EDGE,"E6.5.0.1"),sQuery(id+"F0.wireOp",EDGE,"E6.5.0.2"),sQuery(id+"F0.wireOp",EDGE,"E6.5.0.3"),sQuery(id+"F0.wireOp",EDGE,"E6.6.0.0"),sQuery(id+"F0.wireOp",EDGE,"E6.6.0.1"),sQuery(id+"F0.wireOp",EDGE,"E6.6.0.2"),sQuery(id+"F0.wireOp",EDGE,"E6.6.0.3"),subQ9,subQ0,subQ4,subQ2,subQ11,subQ8,sQuery(id+"F0.wireOp",EDGE,"E13"),sQuery(id+"F0.wireOp",EDGE,"E14"),subQ12,sQuery(id+"F0.wireOp",EDGE,"E16.trimOffspring"),sQuery(id+"F0.wireOp",EDGE,"E17.trimOffspring"),sQuery(id+"F0.wireOp",EDGE,"E18.trimOffspring"),sQuery(id+"F0.wireOp",EDGE,"E19.trimOffspring"),sQuery(id+"F0.wireOp",EDGE,"E20.trimOffspring"),sQuery(id+"F0.wireOp",EDGE,"E21.trimOffspring"),sQuery(id+"F0.wireOp",EDGE,"E22")])],"isStart":false})})]});}
            var Q5;
            {var subQ0=sQuery(id+"F0.wireOp",EDGE,"E8.trimOffspring");var subQ1=sQuery(id+"F0.wireOp",EDGE,"E0.0");var subQ2=sQuery(id+"F0.wireOp",EDGE,"E10.trimOffspring");var subQ3=sQuery(id+"F0.wireOp",EDGE,"E5");var subQ4=sQuery(id+"F0.wireOp",EDGE,"E9.trimOffspring");var subQ5=sQuery(id+"F0.wireOp",EDGE,"E4");var subQ6=sQuery(id+"F0.wireOp",EDGE,"E1");var subQ7=sQuery(id+"F0.wireOp",EDGE,"E2");var subQ8=sQuery(id+"F0.wireOp",EDGE,"E12.trimOffspring");var subQ9=sQuery(id+"F0.wireOp",EDGE,"E7.trimOffspring");var subQ10=sQuery(id+"F0.wireOp",EDGE,"E3");var subQ11=sQuery(id+"F0.wireOp",EDGE,"E11.trimOffspring");var subQ12=sQuery(id+"F0.wireOp",EDGE,"E15.trimOffspring");Q5=makeQuery(id+"F5.opFillet","BLEND_EDGE",EDGE,{"blendedFrom":[makeQuery(id+"F1.opExtrude","SWEPT_EDGE",EDGE,{"disambiguationData":[OSD([subQ3,subQ12])]}),makeQuery(id+"F4.boolean.opBoolean","SPLIT",FACE,{"disambiguationData":[TD([makeQuery(id+"F1.opExtrude","SWEPT_FACE",FACE,{"disambiguationData":[OSD([subQ7])]})])],"derivedFrom":makeQuery(id+"F1.opExtrude","CAP_FACE",FACE,{"disambiguationData":[OSD([subQ1,subQ6,subQ7,subQ10,subQ5,subQ3,sQuery(id+"F0.wireOp",EDGE,"E6.1.0.0"),sQuery(id+"F0.wireOp",EDGE,"E6.1.0.1"),sQuery(id+"F0.wireOp",EDGE,"E6.1.0.2"),sQuery(id+"F0.wireOp",EDGE,"E6.1.0.3"),sQuery(id+"F0.wireOp",EDGE,"E6.2.0.0"),sQuery(id+"F0.wireOp",EDGE,"E6.2.0.1"),sQuery(id+"F0.wireOp",EDGE,"E6.2.0.2"),sQuery(id+"F0.wireOp",EDGE,"E6.2.0.3"),sQuery(id+"F0.wireOp",EDGE,"E6.3.0.0"),sQuery(id+"F0.wireOp",EDGE,"E6.3.0.1"),sQuery(id+"F0.wireOp",EDGE,"E6.3.0.2"),sQuery(id+"F0.wireOp",EDGE,"E6.3.0.3"),sQuery(id+"F0.wireOp",EDGE,"E6.4.0.0"),sQuery(id+"F0.wireOp",EDGE,"E6.4.0.1"),sQuery(id+"F0.wireOp",EDGE,"E6.4.0.2"),sQuery(id+"F0.wireOp",EDGE,"E6.4.0.3"),sQuery(id+"F0.wireOp",EDGE,"E6.5.0.0"),sQuery(id+"F0.wireOp",EDGE,"E6.5.0.1"),sQuery(id+"F0.wireOp",EDGE,"E6.5.0.2"),sQuery(id+"F0.wireOp",EDGE,"E6.5.0.3"),sQuery(id+"F0.wireOp",EDGE,"E6.6.0.0"),sQuery(id+"F0.wireOp",EDGE,"E6.6.0.1"),sQuery(id+"F0.wireOp",EDGE,"E6.6.0.2"),sQuery(id+"F0.wireOp",EDGE,"E6.6.0.3"),subQ9,subQ0,subQ4,subQ2,subQ11,subQ8,sQuery(id+"F0.wireOp",EDGE,"E13"),sQuery(id+"F0.wireOp",EDGE,"E14"),subQ12,sQuery(id+"F0.wireOp",EDGE,"E16.trimOffspring"),sQuery(id+"F0.wireOp",EDGE,"E17.trimOffspring"),sQuery(id+"F0.wireOp",EDGE,"E18.trimOffspring"),sQuery(id+"F0.wireOp",EDGE,"E19.trimOffspring"),sQuery(id+"F0.wireOp",EDGE,"E20.trimOffspring"),sQuery(id+"F0.wireOp",EDGE,"E21.trimOffspring"),sQuery(id+"F0.wireOp",EDGE,"E22")])],"isStart":false})})],"blendedInto":[makeQuery(id+"F4.boolean.opBoolean","SPLIT",FACE,{"disambiguationData":[TD([makeQuery(id+"F1.opExtrude","SWEPT_FACE",FACE,{"disambiguationData":[OSD([subQ7])]})])],"derivedFrom":makeQuery(id+"F1.opExtrude","CAP_FACE",FACE,{"disambiguationData":[OSD([subQ1,subQ6,subQ7,subQ10,subQ5,subQ3,sQuery(id+"F0.wireOp",EDGE,"E6.1.0.0"),sQuery(id+"F0.wireOp",EDGE,"E6.1.0.1"),sQuery(id+"F0.wireOp",EDGE,"E6.1.0.2"),sQuery(id+"F0.wireOp",EDGE,"E6.1.0.3"),sQuery(id+"F0.wireOp",EDGE,"E6.2.0.0"),sQuery(id+"F0.wireOp",EDGE,"E6.2.0.1"),sQuery(id+"F0.wireOp",EDGE,"E6.2.0.2"),sQuery(id+"F0.wireOp",EDGE,"E6.2.0.3"),sQuery(id+"F0.wireOp",EDGE,"E6.3.0.0"),sQuery(id+"F0.wireOp",EDGE,"E6.3.0.1"),sQuery(id+"F0.wireOp",EDGE,"E6.3.0.2"),sQuery(id+"F0.wireOp",EDGE,"E6.3.0.3"),sQuery(id+"F0.wireOp",EDGE,"E6.4.0.0"),sQuery(id+"F0.wireOp",EDGE,"E6.4.0.1"),sQuery(id+"F0.wireOp",EDGE,"E6.4.0.2"),sQuery(id+"F0.wireOp",EDGE,"E6.4.0.3"),sQuery(id+"F0.wireOp",EDGE,"E6.5.0.0"),sQuery(id+"F0.wireOp",EDGE,"E6.5.0.1"),sQuery(id+"F0.wireOp",EDGE,"E6.5.0.2"),sQuery(id+"F0.wireOp",EDGE,"E6.5.0.3"),sQuery(id+"F0.wireOp",EDGE,"E6.6.0.0"),sQuery(id+"F0.wireOp",EDGE,"E6.6.0.1"),sQuery(id+"F0.wireOp",EDGE,"E6.6.0.2"),sQuery(id+"F0.wireOp",EDGE,"E6.6.0.3"),subQ9,subQ0,subQ4,subQ2,subQ11,subQ8,sQuery(id+"F0.wireOp",EDGE,"E13"),sQuery(id+"F0.wireOp",EDGE,"E14"),subQ12,sQuery(id+"F0.wireOp",EDGE,"E16.trimOffspring"),sQuery(id+"F0.wireOp",EDGE,"E17.trimOffspring"),sQuery(id+"F0.wireOp",EDGE,"E18.trimOffspring"),sQuery(id+"F0.wireOp",EDGE,"E19.trimOffspring"),sQuery(id+"F0.wireOp",EDGE,"E20.trimOffspring"),sQuery(id+"F0.wireOp",EDGE,"E21.trimOffspring"),sQuery(id+"F0.wireOp",EDGE,"E22")])],"isStart":false})})]});}
            var Q6;
            Q6=makeQuery(id+"F1.opExtrude","CAP_EDGE",EDGE,{"disambiguationData":[OSD([sQuery(id+"F0.wireOp",EDGE,"E15.trimOffspring")])],"isStart":false});
            var Q7;
            Q7=makeQuery(id+"F1.opExtrude","CAP_EDGE",EDGE,{"disambiguationData":[OSD([sQuery(id+"F0.wireOp",EDGE,"E6.1.0.1")])],"isStart":false});
            var Q8;
            {var subQ0=sQuery(id+"F0.wireOp",EDGE,"E10.trimOffspring");var subQ1=sQuery(id+"F0.wireOp",EDGE,"E6.1.0.3");var subQ2=sQuery(id+"F0.wireOp",EDGE,"E9.trimOffspring");var subQ3=sQuery(id+"F0.wireOp",EDGE,"E6.1.0.2");var subQ4=sQuery(id+"F0.wireOp",EDGE,"E8.trimOffspring");var subQ5=sQuery(id+"F0.wireOp",EDGE,"E0.0");var subQ6=sQuery(id+"F0.wireOp",EDGE,"E7.trimOffspring");var subQ7=sQuery(id+"F0.wireOp",EDGE,"E1");var subQ8=sQuery(id+"F0.wireOp",EDGE,"E6.1.0.0");var subQ9=sQuery(id+"F0.wireOp",EDGE,"E16.trimOffspring");var subQ10=sQuery(id+"F0.wireOp",EDGE,"E6.1.0.1");var subQ11=sQuery(id+"F0.wireOp",EDGE,"E11.trimOffspring");var subQ12=sQuery(id+"F0.wireOp",EDGE,"E12.trimOffspring");Q8=makeQuery(id+"F5.opFillet","BLEND_EDGE",EDGE,{"blendedFrom":[makeQuery(id+"F1.opExtrude","SWEPT_EDGE",EDGE,{"disambiguationData":[OSD([subQ8,subQ10])]}),makeQuery(id+"F4.boolean.opBoolean","SPLIT",FACE,{"disambiguationData":[TD([makeQuery(id+"F1.opExtrude","SWEPT_FACE",FACE,{"disambiguationData":[OSD([subQ8])]})])],"derivedFrom":makeQuery(id+"F1.opExtrude","CAP_FACE",FACE,{"disambiguationData":[OSD([subQ5,subQ7,sQuery(id+"F0.wireOp",EDGE,"E2"),sQuery(id+"F0.wireOp",EDGE,"E3"),sQuery(id+"F0.wireOp",EDGE,"E4"),sQuery(id+"F0.wireOp",EDGE,"E5"),subQ8,subQ10,subQ3,subQ1,sQuery(id+"F0.wireOp",EDGE,"E6.2.0.0"),sQuery(id+"F0.wireOp",EDGE,"E6.2.0.1"),sQuery(id+"F0.wireOp",EDGE,"E6.2.0.2"),sQuery(id+"F0.wireOp",EDGE,"E6.2.0.3"),sQuery(id+"F0.wireOp",EDGE,"E6.3.0.0"),sQuery(id+"F0.wireOp",EDGE,"E6.3.0.1"),sQuery(id+"F0.wireOp",EDGE,"E6.3.0.2"),sQuery(id+"F0.wireOp",EDGE,"E6.3.0.3"),sQuery(id+"F0.wireOp",EDGE,"E6.4.0.0"),sQuery(id+"F0.wireOp",EDGE,"E6.4.0.1"),sQuery(id+"F0.wireOp",EDGE,"E6.4.0.2"),sQuery(id+"F0.wireOp",EDGE,"E6.4.0.3"),sQuery(id+"F0.wireOp",EDGE,"E6.5.0.0"),sQuery(id+"F0.wireOp",EDGE,"E6.5.0.1"),sQuery(id+"F0.wireOp",EDGE,"E6.5.0.2"),sQuery(id+"F0.wireOp",EDGE,"E6.5.0.3"),sQuery(id+"F0.wireOp",EDGE,"E6.6.0.0"),sQuery(id+"F0.wireOp",EDGE,"E6.6.0.1"),sQuery(id+"F0.wireOp",EDGE,"E6.6.0.2"),sQuery(id+"F0.wireOp",EDGE,"E6.6.0.3"),subQ6,subQ4,subQ2,subQ0,subQ11,subQ12,sQuery(id+"F0.wireOp",EDGE,"E13"),sQuery(id+"F0.wireOp",EDGE,"E14"),sQuery(id+"F0.wireOp",EDGE,"E15.trimOffspring"),subQ9,sQuery(id+"F0.wireOp",EDGE,"E17.trimOffspring"),sQuery(id+"F0.wireOp",EDGE,"E18.trimOffspring"),sQuery(id+"F0.wireOp",EDGE,"E19.trimOffspring"),sQuery(id+"F0.wireOp",EDGE,"E20.trimOffspring"),sQuery(id+"F0.wireOp",EDGE,"E21.trimOffspring"),sQuery(id+"F0.wireOp",EDGE,"E22")])],"isStart":false})})],"blendedInto":[makeQuery(id+"F4.boolean.opBoolean","SPLIT",FACE,{"disambiguationData":[TD([makeQuery(id+"F1.opExtrude","SWEPT_FACE",FACE,{"disambiguationData":[OSD([subQ8])]})])],"derivedFrom":makeQuery(id+"F1.opExtrude","CAP_FACE",FACE,{"disambiguationData":[OSD([subQ5,subQ7,sQuery(id+"F0.wireOp",EDGE,"E2"),sQuery(id+"F0.wireOp",EDGE,"E3"),sQuery(id+"F0.wireOp",EDGE,"E4"),sQuery(id+"F0.wireOp",EDGE,"E5"),subQ8,subQ10,subQ3,subQ1,sQuery(id+"F0.wireOp",EDGE,"E6.2.0.0"),sQuery(id+"F0.wireOp",EDGE,"E6.2.0.1"),sQuery(id+"F0.wireOp",EDGE,"E6.2.0.2"),sQuery(id+"F0.wireOp",EDGE,"E6.2.0.3"),sQuery(id+"F0.wireOp",EDGE,"E6.3.0.0"),sQuery(id+"F0.wireOp",EDGE,"E6.3.0.1"),sQuery(id+"F0.wireOp",EDGE,"E6.3.0.2"),sQuery(id+"F0.wireOp",EDGE,"E6.3.0.3"),sQuery(id+"F0.wireOp",EDGE,"E6.4.0.0"),sQuery(id+"F0.wireOp",EDGE,"E6.4.0.1"),sQuery(id+"F0.wireOp",EDGE,"E6.4.0.2"),sQuery(id+"F0.wireOp",EDGE,"E6.4.0.3"),sQuery(id+"F0.wireOp",EDGE,"E6.5.0.0"),sQuery(id+"F0.wireOp",EDGE,"E6.5.0.1"),sQuery(id+"F0.wireOp",EDGE,"E6.5.0.2"),sQuery(id+"F0.wireOp",EDGE,"E6.5.0.3"),sQuery(id+"F0.wireOp",EDGE,"E6.6.0.0"),sQuery(id+"F0.wireOp",EDGE,"E6.6.0.1"),sQuery(id+"F0.wireOp",EDGE,"E6.6.0.2"),sQuery(id+"F0.wireOp",EDGE,"E6.6.0.3"),subQ6,subQ4,subQ2,subQ0,subQ11,subQ12,sQuery(id+"F0.wireOp",EDGE,"E13"),sQuery(id+"F0.wireOp",EDGE,"E14"),sQuery(id+"F0.wireOp",EDGE,"E15.trimOffspring"),subQ9,sQuery(id+"F0.wireOp",EDGE,"E17.trimOffspring"),sQuery(id+"F0.wireOp",EDGE,"E18.trimOffspring"),sQuery(id+"F0.wireOp",EDGE,"E19.trimOffspring"),sQuery(id+"F0.wireOp",EDGE,"E20.trimOffspring"),sQuery(id+"F0.wireOp",EDGE,"E21.trimOffspring"),sQuery(id+"F0.wireOp",EDGE,"E22")])],"isStart":false})})]});}
            var Q9;
            {var subQ0=sQuery(id+"F0.wireOp",EDGE,"E10.trimOffspring");var subQ1=sQuery(id+"F0.wireOp",EDGE,"E6.1.0.3");var subQ2=sQuery(id+"F0.wireOp",EDGE,"E9.trimOffspring");var subQ3=sQuery(id+"F0.wireOp",EDGE,"E6.1.0.2");var subQ4=sQuery(id+"F0.wireOp",EDGE,"E8.trimOffspring");var subQ5=sQuery(id+"F0.wireOp",EDGE,"E0.0");var subQ6=sQuery(id+"F0.wireOp",EDGE,"E7.trimOffspring");var subQ7=sQuery(id+"F0.wireOp",EDGE,"E1");var subQ8=sQuery(id+"F0.wireOp",EDGE,"E6.1.0.0");var subQ9=sQuery(id+"F0.wireOp",EDGE,"E16.trimOffspring");var subQ10=sQuery(id+"F0.wireOp",EDGE,"E6.1.0.1");var subQ11=sQuery(id+"F0.wireOp",EDGE,"E11.trimOffspring");var subQ12=sQuery(id+"F0.wireOp",EDGE,"E12.trimOffspring");Q9=makeQuery(id+"F5.opFillet","BLEND_EDGE",EDGE,{"blendedFrom":[makeQuery(id+"F1.opExtrude","SWEPT_EDGE",EDGE,{"disambiguationData":[OSD([subQ8,subQ3])]}),makeQuery(id+"F4.boolean.opBoolean","SPLIT",FACE,{"disambiguationData":[TD([makeQuery(id+"F1.opExtrude","SWEPT_FACE",FACE,{"disambiguationData":[OSD([subQ8])]})])],"derivedFrom":makeQuery(id+"F1.opExtrude","CAP_FACE",FACE,{"disambiguationData":[OSD([subQ5,subQ7,sQuery(id+"F0.wireOp",EDGE,"E2"),sQuery(id+"F0.wireOp",EDGE,"E3"),sQuery(id+"F0.wireOp",EDGE,"E4"),sQuery(id+"F0.wireOp",EDGE,"E5"),subQ8,subQ10,subQ3,subQ1,sQuery(id+"F0.wireOp",EDGE,"E6.2.0.0"),sQuery(id+"F0.wireOp",EDGE,"E6.2.0.1"),sQuery(id+"F0.wireOp",EDGE,"E6.2.0.2"),sQuery(id+"F0.wireOp",EDGE,"E6.2.0.3"),sQuery(id+"F0.wireOp",EDGE,"E6.3.0.0"),sQuery(id+"F0.wireOp",EDGE,"E6.3.0.1"),sQuery(id+"F0.wireOp",EDGE,"E6.3.0.2"),sQuery(id+"F0.wireOp",EDGE,"E6.3.0.3"),sQuery(id+"F0.wireOp",EDGE,"E6.4.0.0"),sQuery(id+"F0.wireOp",EDGE,"E6.4.0.1"),sQuery(id+"F0.wireOp",EDGE,"E6.4.0.2"),sQuery(id+"F0.wireOp",EDGE,"E6.4.0.3"),sQuery(id+"F0.wireOp",EDGE,"E6.5.0.0"),sQuery(id+"F0.wireOp",EDGE,"E6.5.0.1"),sQuery(id+"F0.wireOp",EDGE,"E6.5.0.2"),sQuery(id+"F0.wireOp",EDGE,"E6.5.0.3"),sQuery(id+"F0.wireOp",EDGE,"E6.6.0.0"),sQuery(id+"F0.wireOp",EDGE,"E6.6.0.1"),sQuery(id+"F0.wireOp",EDGE,"E6.6.0.2"),sQuery(id+"F0.wireOp",EDGE,"E6.6.0.3"),subQ6,subQ4,subQ2,subQ0,subQ11,subQ12,sQuery(id+"F0.wireOp",EDGE,"E13"),sQuery(id+"F0.wireOp",EDGE,"E14"),sQuery(id+"F0.wireOp",EDGE,"E15.trimOffspring"),subQ9,sQuery(id+"F0.wireOp",EDGE,"E17.trimOffspring"),sQuery(id+"F0.wireOp",EDGE,"E18.trimOffspring"),sQuery(id+"F0.wireOp",EDGE,"E19.trimOffspring"),sQuery(id+"F0.wireOp",EDGE,"E20.trimOffspring"),sQuery(id+"F0.wireOp",EDGE,"E21.trimOffspring"),sQuery(id+"F0.wireOp",EDGE,"E22")])],"isStart":false})})],"blendedInto":[makeQuery(id+"F4.boolean.opBoolean","SPLIT",FACE,{"disambiguationData":[TD([makeQuery(id+"F1.opExtrude","SWEPT_FACE",FACE,{"disambiguationData":[OSD([subQ8])]})])],"derivedFrom":makeQuery(id+"F1.opExtrude","CAP_FACE",FACE,{"disambiguationData":[OSD([subQ5,subQ7,sQuery(id+"F0.wireOp",EDGE,"E2"),sQuery(id+"F0.wireOp",EDGE,"E3"),sQuery(id+"F0.wireOp",EDGE,"E4"),sQuery(id+"F0.wireOp",EDGE,"E5"),subQ8,subQ10,subQ3,subQ1,sQuery(id+"F0.wireOp",EDGE,"E6.2.0.0"),sQuery(id+"F0.wireOp",EDGE,"E6.2.0.1"),sQuery(id+"F0.wireOp",EDGE,"E6.2.0.2"),sQuery(id+"F0.wireOp",EDGE,"E6.2.0.3"),sQuery(id+"F0.wireOp",EDGE,"E6.3.0.0"),sQuery(id+"F0.wireOp",EDGE,"E6.3.0.1"),sQuery(id+"F0.wireOp",EDGE,"E6.3.0.2"),sQuery(id+"F0.wireOp",EDGE,"E6.3.0.3"),sQuery(id+"F0.wireOp",EDGE,"E6.4.0.0"),sQuery(id+"F0.wireOp",EDGE,"E6.4.0.1"),sQuery(id+"F0.wireOp",EDGE,"E6.4.0.2"),sQuery(id+"F0.wireOp",EDGE,"E6.4.0.3"),sQuery(id+"F0.wireOp",EDGE,"E6.5.0.0"),sQuery(id+"F0.wireOp",EDGE,"E6.5.0.1"),sQuery(id+"F0.wireOp",EDGE,"E6.5.0.2"),sQuery(id+"F0.wireOp",EDGE,"E6.5.0.3"),sQuery(id+"F0.wireOp",EDGE,"E6.6.0.0"),sQuery(id+"F0.wireOp",EDGE,"E6.6.0.1"),sQuery(id+"F0.wireOp",EDGE,"E6.6.0.2"),sQuery(id+"F0.wireOp",EDGE,"E6.6.0.3"),subQ6,subQ4,subQ2,subQ0,subQ11,subQ12,sQuery(id+"F0.wireOp",EDGE,"E13"),sQuery(id+"F0.wireOp",EDGE,"E14"),sQuery(id+"F0.wireOp",EDGE,"E15.trimOffspring"),subQ9,sQuery(id+"F0.wireOp",EDGE,"E17.trimOffspring"),sQuery(id+"F0.wireOp",EDGE,"E18.trimOffspring"),sQuery(id+"F0.wireOp",EDGE,"E19.trimOffspring"),sQuery(id+"F0.wireOp",EDGE,"E20.trimOffspring"),sQuery(id+"F0.wireOp",EDGE,"E21.trimOffspring"),sQuery(id+"F0.wireOp",EDGE,"E22")])],"isStart":false})})]});}
            var Q10;
            Q10=makeQuery(id+"F1.opExtrude","CAP_EDGE",EDGE,{"disambiguationData":[OSD([sQuery(id+"F0.wireOp",EDGE,"E6.1.0.2")])],"isStart":false});
            var Q11;
            {var subQ0=sQuery(id+"F0.wireOp",EDGE,"E10.trimOffspring");var subQ1=sQuery(id+"F0.wireOp",EDGE,"E6.1.0.3");var subQ2=sQuery(id+"F0.wireOp",EDGE,"E9.trimOffspring");var subQ3=sQuery(id+"F0.wireOp",EDGE,"E6.1.0.2");var subQ4=sQuery(id+"F0.wireOp",EDGE,"E8.trimOffspring");var subQ5=sQuery(id+"F0.wireOp",EDGE,"E0.0");var subQ6=sQuery(id+"F0.wireOp",EDGE,"E7.trimOffspring");var subQ7=sQuery(id+"F0.wireOp",EDGE,"E1");var subQ8=sQuery(id+"F0.wireOp",EDGE,"E6.1.0.0");var subQ9=sQuery(id+"F0.wireOp",EDGE,"E16.trimOffspring");var subQ10=sQuery(id+"F0.wireOp",EDGE,"E6.1.0.1");var subQ11=sQuery(id+"F0.wireOp",EDGE,"E11.trimOffspring");var subQ12=sQuery(id+"F0.wireOp",EDGE,"E12.trimOffspring");Q11=makeQuery(id+"F5.opFillet","BLEND_EDGE",EDGE,{"blendedFrom":[makeQuery(id+"F1.opExtrude","SWEPT_EDGE",EDGE,{"disambiguationData":[OSD([subQ3,subQ1])]}),makeQuery(id+"F4.boolean.opBoolean","SPLIT",FACE,{"disambiguationData":[TD([makeQuery(id+"F1.opExtrude","SWEPT_FACE",FACE,{"disambiguationData":[OSD([subQ8])]})])],"derivedFrom":makeQuery(id+"F1.opExtrude","CAP_FACE",FACE,{"disambiguationData":[OSD([subQ5,subQ7,sQuery(id+"F0.wireOp",EDGE,"E2"),sQuery(id+"F0.wireOp",EDGE,"E3"),sQuery(id+"F0.wireOp",EDGE,"E4"),sQuery(id+"F0.wireOp",EDGE,"E5"),subQ8,subQ10,subQ3,subQ1,sQuery(id+"F0.wireOp",EDGE,"E6.2.0.0"),sQuery(id+"F0.wireOp",EDGE,"E6.2.0.1"),sQuery(id+"F0.wireOp",EDGE,"E6.2.0.2"),sQuery(id+"F0.wireOp",EDGE,"E6.2.0.3"),sQuery(id+"F0.wireOp",EDGE,"E6.3.0.0"),sQuery(id+"F0.wireOp",EDGE,"E6.3.0.1"),sQuery(id+"F0.wireOp",EDGE,"E6.3.0.2"),sQuery(id+"F0.wireOp",EDGE,"E6.3.0.3"),sQuery(id+"F0.wireOp",EDGE,"E6.4.0.0"),sQuery(id+"F0.wireOp",EDGE,"E6.4.0.1"),sQuery(id+"F0.wireOp",EDGE,"E6.4.0.2"),sQuery(id+"F0.wireOp",EDGE,"E6.4.0.3"),sQuery(id+"F0.wireOp",EDGE,"E6.5.0.0"),sQuery(id+"F0.wireOp",EDGE,"E6.5.0.1"),sQuery(id+"F0.wireOp",EDGE,"E6.5.0.2"),sQuery(id+"F0.wireOp",EDGE,"E6.5.0.3"),sQuery(id+"F0.wireOp",EDGE,"E6.6.0.0"),sQuery(id+"F0.wireOp",EDGE,"E6.6.0.1"),sQuery(id+"F0.wireOp",EDGE,"E6.6.0.2"),sQuery(id+"F0.wireOp",EDGE,"E6.6.0.3"),subQ6,subQ4,subQ2,subQ0,subQ11,subQ12,sQuery(id+"F0.wireOp",EDGE,"E13"),sQuery(id+"F0.wireOp",EDGE,"E14"),sQuery(id+"F0.wireOp",EDGE,"E15.trimOffspring"),subQ9,sQuery(id+"F0.wireOp",EDGE,"E17.trimOffspring"),sQuery(id+"F0.wireOp",EDGE,"E18.trimOffspring"),sQuery(id+"F0.wireOp",EDGE,"E19.trimOffspring"),sQuery(id+"F0.wireOp",EDGE,"E20.trimOffspring"),sQuery(id+"F0.wireOp",EDGE,"E21.trimOffspring"),sQuery(id+"F0.wireOp",EDGE,"E22")])],"isStart":false})})],"blendedInto":[makeQuery(id+"F4.boolean.opBoolean","SPLIT",FACE,{"disambiguationData":[TD([makeQuery(id+"F1.opExtrude","SWEPT_FACE",FACE,{"disambiguationData":[OSD([subQ8])]})])],"derivedFrom":makeQuery(id+"F1.opExtrude","CAP_FACE",FACE,{"disambiguationData":[OSD([subQ5,subQ7,sQuery(id+"F0.wireOp",EDGE,"E2"),sQuery(id+"F0.wireOp",EDGE,"E3"),sQuery(id+"F0.wireOp",EDGE,"E4"),sQuery(id+"F0.wireOp",EDGE,"E5"),subQ8,subQ10,subQ3,subQ1,sQuery(id+"F0.wireOp",EDGE,"E6.2.0.0"),sQuery(id+"F0.wireOp",EDGE,"E6.2.0.1"),sQuery(id+"F0.wireOp",EDGE,"E6.2.0.2"),sQuery(id+"F0.wireOp",EDGE,"E6.2.0.3"),sQuery(id+"F0.wireOp",EDGE,"E6.3.0.0"),sQuery(id+"F0.wireOp",EDGE,"E6.3.0.1"),sQuery(id+"F0.wireOp",EDGE,"E6.3.0.2"),sQuery(id+"F0.wireOp",EDGE,"E6.3.0.3"),sQuery(id+"F0.wireOp",EDGE,"E6.4.0.0"),sQuery(id+"F0.wireOp",EDGE,"E6.4.0.1"),sQuery(id+"F0.wireOp",EDGE,"E6.4.0.2"),sQuery(id+"F0.wireOp",EDGE,"E6.4.0.3"),sQuery(id+"F0.wireOp",EDGE,"E6.5.0.0"),sQuery(id+"F0.wireOp",EDGE,"E6.5.0.1"),sQuery(id+"F0.wireOp",EDGE,"E6.5.0.2"),sQuery(id+"F0.wireOp",EDGE,"E6.5.0.3"),sQuery(id+"F0.wireOp",EDGE,"E6.6.0.0"),sQuery(id+"F0.wireOp",EDGE,"E6.6.0.1"),sQuery(id+"F0.wireOp",EDGE,"E6.6.0.2"),sQuery(id+"F0.wireOp",EDGE,"E6.6.0.3"),subQ6,subQ4,subQ2,subQ0,subQ11,subQ12,sQuery(id+"F0.wireOp",EDGE,"E13"),sQuery(id+"F0.wireOp",EDGE,"E14"),sQuery(id+"F0.wireOp",EDGE,"E15.trimOffspring"),subQ9,sQuery(id+"F0.wireOp",EDGE,"E17.trimOffspring"),sQuery(id+"F0.wireOp",EDGE,"E18.trimOffspring"),sQuery(id+"F0.wireOp",EDGE,"E19.trimOffspring"),sQuery(id+"F0.wireOp",EDGE,"E20.trimOffspring"),sQuery(id+"F0.wireOp",EDGE,"E21.trimOffspring"),sQuery(id+"F0.wireOp",EDGE,"E22")])],"isStart":false})})]});}
            var Q12;
            {var subQ0=sQuery(id+"F0.wireOp",EDGE,"E10.trimOffspring");var subQ1=sQuery(id+"F0.wireOp",EDGE,"E6.1.0.3");var subQ2=sQuery(id+"F0.wireOp",EDGE,"E9.trimOffspring");var subQ3=sQuery(id+"F0.wireOp",EDGE,"E6.1.0.2");var subQ4=sQuery(id+"F0.wireOp",EDGE,"E8.trimOffspring");var subQ5=sQuery(id+"F0.wireOp",EDGE,"E0.0");var subQ6=sQuery(id+"F0.wireOp",EDGE,"E7.trimOffspring");var subQ7=sQuery(id+"F0.wireOp",EDGE,"E1");var subQ8=sQuery(id+"F0.wireOp",EDGE,"E6.1.0.0");var subQ9=sQuery(id+"F0.wireOp",EDGE,"E16.trimOffspring");var subQ10=sQuery(id+"F0.wireOp",EDGE,"E6.1.0.1");var subQ11=sQuery(id+"F0.wireOp",EDGE,"E11.trimOffspring");var subQ12=sQuery(id+"F0.wireOp",EDGE,"E12.trimOffspring");Q12=makeQuery(id+"F5.opFillet","BLEND_EDGE",EDGE,{"blendedFrom":[makeQuery(id+"F1.opExtrude","SWEPT_EDGE",EDGE,{"disambiguationData":[OSD([subQ1,subQ9])]}),makeQuery(id+"F4.boolean.opBoolean","SPLIT",FACE,{"disambiguationData":[TD([makeQuery(id+"F1.opExtrude","SWEPT_FACE",FACE,{"disambiguationData":[OSD([subQ8])]})])],"derivedFrom":makeQuery(id+"F1.opExtrude","CAP_FACE",FACE,{"disambiguationData":[OSD([subQ5,subQ7,sQuery(id+"F0.wireOp",EDGE,"E2"),sQuery(id+"F0.wireOp",EDGE,"E3"),sQuery(id+"F0.wireOp",EDGE,"E4"),sQuery(id+"F0.wireOp",EDGE,"E5"),subQ8,subQ10,subQ3,subQ1,sQuery(id+"F0.wireOp",EDGE,"E6.2.0.0"),sQuery(id+"F0.wireOp",EDGE,"E6.2.0.1"),sQuery(id+"F0.wireOp",EDGE,"E6.2.0.2"),sQuery(id+"F0.wireOp",EDGE,"E6.2.0.3"),sQuery(id+"F0.wireOp",EDGE,"E6.3.0.0"),sQuery(id+"F0.wireOp",EDGE,"E6.3.0.1"),sQuery(id+"F0.wireOp",EDGE,"E6.3.0.2"),sQuery(id+"F0.wireOp",EDGE,"E6.3.0.3"),sQuery(id+"F0.wireOp",EDGE,"E6.4.0.0"),sQuery(id+"F0.wireOp",EDGE,"E6.4.0.1"),sQuery(id+"F0.wireOp",EDGE,"E6.4.0.2"),sQuery(id+"F0.wireOp",EDGE,"E6.4.0.3"),sQuery(id+"F0.wireOp",EDGE,"E6.5.0.0"),sQuery(id+"F0.wireOp",EDGE,"E6.5.0.1"),sQuery(id+"F0.wireOp",EDGE,"E6.5.0.2"),sQuery(id+"F0.wireOp",EDGE,"E6.5.0.3"),sQuery(id+"F0.wireOp",EDGE,"E6.6.0.0"),sQuery(id+"F0.wireOp",EDGE,"E6.6.0.1"),sQuery(id+"F0.wireOp",EDGE,"E6.6.0.2"),sQuery(id+"F0.wireOp",EDGE,"E6.6.0.3"),subQ6,subQ4,subQ2,subQ0,subQ11,subQ12,sQuery(id+"F0.wireOp",EDGE,"E13"),sQuery(id+"F0.wireOp",EDGE,"E14"),sQuery(id+"F0.wireOp",EDGE,"E15.trimOffspring"),subQ9,sQuery(id+"F0.wireOp",EDGE,"E17.trimOffspring"),sQuery(id+"F0.wireOp",EDGE,"E18.trimOffspring"),sQuery(id+"F0.wireOp",EDGE,"E19.trimOffspring"),sQuery(id+"F0.wireOp",EDGE,"E20.trimOffspring"),sQuery(id+"F0.wireOp",EDGE,"E21.trimOffspring"),sQuery(id+"F0.wireOp",EDGE,"E22")])],"isStart":false})})],"blendedInto":[makeQuery(id+"F4.boolean.opBoolean","SPLIT",FACE,{"disambiguationData":[TD([makeQuery(id+"F1.opExtrude","SWEPT_FACE",FACE,{"disambiguationData":[OSD([subQ8])]})])],"derivedFrom":makeQuery(id+"F1.opExtrude","CAP_FACE",FACE,{"disambiguationData":[OSD([subQ5,subQ7,sQuery(id+"F0.wireOp",EDGE,"E2"),sQuery(id+"F0.wireOp",EDGE,"E3"),sQuery(id+"F0.wireOp",EDGE,"E4"),sQuery(id+"F0.wireOp",EDGE,"E5"),subQ8,subQ10,subQ3,subQ1,sQuery(id+"F0.wireOp",EDGE,"E6.2.0.0"),sQuery(id+"F0.wireOp",EDGE,"E6.2.0.1"),sQuery(id+"F0.wireOp",EDGE,"E6.2.0.2"),sQuery(id+"F0.wireOp",EDGE,"E6.2.0.3"),sQuery(id+"F0.wireOp",EDGE,"E6.3.0.0"),sQuery(id+"F0.wireOp",EDGE,"E6.3.0.1"),sQuery(id+"F0.wireOp",EDGE,"E6.3.0.2"),sQuery(id+"F0.wireOp",EDGE,"E6.3.0.3"),sQuery(id+"F0.wireOp",EDGE,"E6.4.0.0"),sQuery(id+"F0.wireOp",EDGE,"E6.4.0.1"),sQuery(id+"F0.wireOp",EDGE,"E6.4.0.2"),sQuery(id+"F0.wireOp",EDGE,"E6.4.0.3"),sQuery(id+"F0.wireOp",EDGE,"E6.5.0.0"),sQuery(id+"F0.wireOp",EDGE,"E6.5.0.1"),sQuery(id+"F0.wireOp",EDGE,"E6.5.0.2"),sQuery(id+"F0.wireOp",EDGE,"E6.5.0.3"),sQuery(id+"F0.wireOp",EDGE,"E6.6.0.0"),sQuery(id+"F0.wireOp",EDGE,"E6.6.0.1"),sQuery(id+"F0.wireOp",EDGE,"E6.6.0.2"),sQuery(id+"F0.wireOp",EDGE,"E6.6.0.3"),subQ6,subQ4,subQ2,subQ0,subQ11,subQ12,sQuery(id+"F0.wireOp",EDGE,"E13"),sQuery(id+"F0.wireOp",EDGE,"E14"),sQuery(id+"F0.wireOp",EDGE,"E15.trimOffspring"),subQ9,sQuery(id+"F0.wireOp",EDGE,"E17.trimOffspring"),sQuery(id+"F0.wireOp",EDGE,"E18.trimOffspring"),sQuery(id+"F0.wireOp",EDGE,"E19.trimOffspring"),sQuery(id+"F0.wireOp",EDGE,"E20.trimOffspring"),sQuery(id+"F0.wireOp",EDGE,"E21.trimOffspring"),sQuery(id+"F0.wireOp",EDGE,"E22")])],"isStart":false})})]});}
            var Q13;
            Q13=makeQuery(id+"F1.opExtrude","CAP_EDGE",EDGE,{"disambiguationData":[OSD([sQuery(id+"F0.wireOp",EDGE,"E16.trimOffspring")])],"isStart":false});
            var Q14;
            Q14=makeQuery(id+"F1.opExtrude","CAP_EDGE",EDGE,{"disambiguationData":[OSD([sQuery(id+"F0.wireOp",EDGE,"E6.2.0.1")])],"isStart":false});
            var Q15;
            {var subQ0=sQuery(id+"F0.wireOp",EDGE,"E9.trimOffspring");var subQ1=sQuery(id+"F0.wireOp",EDGE,"E6.2.0.3");var subQ2=sQuery(id+"F0.wireOp",EDGE,"E10.trimOffspring");var subQ3=sQuery(id+"F0.wireOp",EDGE,"E6.2.0.2");var subQ4=sQuery(id+"F0.wireOp",EDGE,"E0.0");var subQ5=sQuery(id+"F0.wireOp",EDGE,"E8.trimOffspring");var subQ6=sQuery(id+"F0.wireOp",EDGE,"E1");var subQ7=sQuery(id+"F0.wireOp",EDGE,"E7.trimOffspring");var subQ8=sQuery(id+"F0.wireOp",EDGE,"E17.trimOffspring");var subQ9=sQuery(id+"F0.wireOp",EDGE,"E6.2.0.0");var subQ10=sQuery(id+"F0.wireOp",EDGE,"E6.2.0.1");var subQ11=sQuery(id+"F0.wireOp",EDGE,"E11.trimOffspring");var subQ12=sQuery(id+"F0.wireOp",EDGE,"E12.trimOffspring");Q15=makeQuery(id+"F5.opFillet","BLEND_EDGE",EDGE,{"blendedFrom":[makeQuery(id+"F1.opExtrude","SWEPT_EDGE",EDGE,{"disambiguationData":[OSD([subQ9,subQ10])]}),makeQuery(id+"F4.boolean.opBoolean","SPLIT",FACE,{"disambiguationData":[TD([makeQuery(id+"F1.opExtrude","SWEPT_FACE",FACE,{"disambiguationData":[OSD([subQ9])]})])],"derivedFrom":makeQuery(id+"F1.opExtrude","CAP_FACE",FACE,{"disambiguationData":[OSD([subQ4,subQ6,sQuery(id+"F0.wireOp",EDGE,"E2"),sQuery(id+"F0.wireOp",EDGE,"E3"),sQuery(id+"F0.wireOp",EDGE,"E4"),sQuery(id+"F0.wireOp",EDGE,"E5"),sQuery(id+"F0.wireOp",EDGE,"E6.1.0.0"),sQuery(id+"F0.wireOp",EDGE,"E6.1.0.1"),sQuery(id+"F0.wireOp",EDGE,"E6.1.0.2"),sQuery(id+"F0.wireOp",EDGE,"E6.1.0.3"),subQ9,subQ10,subQ3,subQ1,sQuery(id+"F0.wireOp",EDGE,"E6.3.0.0"),sQuery(id+"F0.wireOp",EDGE,"E6.3.0.1"),sQuery(id+"F0.wireOp",EDGE,"E6.3.0.2"),sQuery(id+"F0.wireOp",EDGE,"E6.3.0.3"),sQuery(id+"F0.wireOp",EDGE,"E6.4.0.0"),sQuery(id+"F0.wireOp",EDGE,"E6.4.0.1"),sQuery(id+"F0.wireOp",EDGE,"E6.4.0.2"),sQuery(id+"F0.wireOp",EDGE,"E6.4.0.3"),sQuery(id+"F0.wireOp",EDGE,"E6.5.0.0"),sQuery(id+"F0.wireOp",EDGE,"E6.5.0.1"),sQuery(id+"F0.wireOp",EDGE,"E6.5.0.2"),sQuery(id+"F0.wireOp",EDGE,"E6.5.0.3"),sQuery(id+"F0.wireOp",EDGE,"E6.6.0.0"),sQuery(id+"F0.wireOp",EDGE,"E6.6.0.1"),sQuery(id+"F0.wireOp",EDGE,"E6.6.0.2"),sQuery(id+"F0.wireOp",EDGE,"E6.6.0.3"),subQ7,subQ5,subQ0,subQ2,subQ11,subQ12,sQuery(id+"F0.wireOp",EDGE,"E13"),sQuery(id+"F0.wireOp",EDGE,"E14"),sQuery(id+"F0.wireOp",EDGE,"E15.trimOffspring"),sQuery(id+"F0.wireOp",EDGE,"E16.trimOffspring"),subQ8,sQuery(id+"F0.wireOp",EDGE,"E18.trimOffspring"),sQuery(id+"F0.wireOp",EDGE,"E19.trimOffspring"),sQuery(id+"F0.wireOp",EDGE,"E20.trimOffspring"),sQuery(id+"F0.wireOp",EDGE,"E21.trimOffspring"),sQuery(id+"F0.wireOp",EDGE,"E22")])],"isStart":false})})],"blendedInto":[makeQuery(id+"F4.boolean.opBoolean","SPLIT",FACE,{"disambiguationData":[TD([makeQuery(id+"F1.opExtrude","SWEPT_FACE",FACE,{"disambiguationData":[OSD([subQ9])]})])],"derivedFrom":makeQuery(id+"F1.opExtrude","CAP_FACE",FACE,{"disambiguationData":[OSD([subQ4,subQ6,sQuery(id+"F0.wireOp",EDGE,"E2"),sQuery(id+"F0.wireOp",EDGE,"E3"),sQuery(id+"F0.wireOp",EDGE,"E4"),sQuery(id+"F0.wireOp",EDGE,"E5"),sQuery(id+"F0.wireOp",EDGE,"E6.1.0.0"),sQuery(id+"F0.wireOp",EDGE,"E6.1.0.1"),sQuery(id+"F0.wireOp",EDGE,"E6.1.0.2"),sQuery(id+"F0.wireOp",EDGE,"E6.1.0.3"),subQ9,subQ10,subQ3,subQ1,sQuery(id+"F0.wireOp",EDGE,"E6.3.0.0"),sQuery(id+"F0.wireOp",EDGE,"E6.3.0.1"),sQuery(id+"F0.wireOp",EDGE,"E6.3.0.2"),sQuery(id+"F0.wireOp",EDGE,"E6.3.0.3"),sQuery(id+"F0.wireOp",EDGE,"E6.4.0.0"),sQuery(id+"F0.wireOp",EDGE,"E6.4.0.1"),sQuery(id+"F0.wireOp",EDGE,"E6.4.0.2"),sQuery(id+"F0.wireOp",EDGE,"E6.4.0.3"),sQuery(id+"F0.wireOp",EDGE,"E6.5.0.0"),sQuery(id+"F0.wireOp",EDGE,"E6.5.0.1"),sQuery(id+"F0.wireOp",EDGE,"E6.5.0.2"),sQuery(id+"F0.wireOp",EDGE,"E6.5.0.3"),sQuery(id+"F0.wireOp",EDGE,"E6.6.0.0"),sQuery(id+"F0.wireOp",EDGE,"E6.6.0.1"),sQuery(id+"F0.wireOp",EDGE,"E6.6.0.2"),sQuery(id+"F0.wireOp",EDGE,"E6.6.0.3"),subQ7,subQ5,subQ0,subQ2,subQ11,subQ12,sQuery(id+"F0.wireOp",EDGE,"E13"),sQuery(id+"F0.wireOp",EDGE,"E14"),sQuery(id+"F0.wireOp",EDGE,"E15.trimOffspring"),sQuery(id+"F0.wireOp",EDGE,"E16.trimOffspring"),subQ8,sQuery(id+"F0.wireOp",EDGE,"E18.trimOffspring"),sQuery(id+"F0.wireOp",EDGE,"E19.trimOffspring"),sQuery(id+"F0.wireOp",EDGE,"E20.trimOffspring"),sQuery(id+"F0.wireOp",EDGE,"E21.trimOffspring"),sQuery(id+"F0.wireOp",EDGE,"E22")])],"isStart":false})})]});}
            var Q16;
            Q16=makeQuery(id+"F1.opExtrude","CAP_EDGE",EDGE,{"disambiguationData":[OSD([sQuery(id+"F0.wireOp",EDGE,"E6.2.0.2")])],"isStart":false});
            var Q17;
            {var subQ0=sQuery(id+"F0.wireOp",EDGE,"E9.trimOffspring");var subQ1=sQuery(id+"F0.wireOp",EDGE,"E6.2.0.3");var subQ2=sQuery(id+"F0.wireOp",EDGE,"E10.trimOffspring");var subQ3=sQuery(id+"F0.wireOp",EDGE,"E6.2.0.2");var subQ4=sQuery(id+"F0.wireOp",EDGE,"E0.0");var subQ5=sQuery(id+"F0.wireOp",EDGE,"E8.trimOffspring");var subQ6=sQuery(id+"F0.wireOp",EDGE,"E1");var subQ7=sQuery(id+"F0.wireOp",EDGE,"E7.trimOffspring");var subQ8=sQuery(id+"F0.wireOp",EDGE,"E17.trimOffspring");var subQ9=sQuery(id+"F0.wireOp",EDGE,"E6.2.0.0");var subQ10=sQuery(id+"F0.wireOp",EDGE,"E6.2.0.1");var subQ11=sQuery(id+"F0.wireOp",EDGE,"E11.trimOffspring");var subQ12=sQuery(id+"F0.wireOp",EDGE,"E12.trimOffspring");Q17=makeQuery(id+"F5.opFillet","BLEND_EDGE",EDGE,{"blendedFrom":[makeQuery(id+"F1.opExtrude","SWEPT_EDGE",EDGE,{"disambiguationData":[OSD([subQ9,subQ3])]}),makeQuery(id+"F4.boolean.opBoolean","SPLIT",FACE,{"disambiguationData":[TD([makeQuery(id+"F1.opExtrude","SWEPT_FACE",FACE,{"disambiguationData":[OSD([subQ9])]})])],"derivedFrom":makeQuery(id+"F1.opExtrude","CAP_FACE",FACE,{"disambiguationData":[OSD([subQ4,subQ6,sQuery(id+"F0.wireOp",EDGE,"E2"),sQuery(id+"F0.wireOp",EDGE,"E3"),sQuery(id+"F0.wireOp",EDGE,"E4"),sQuery(id+"F0.wireOp",EDGE,"E5"),sQuery(id+"F0.wireOp",EDGE,"E6.1.0.0"),sQuery(id+"F0.wireOp",EDGE,"E6.1.0.1"),sQuery(id+"F0.wireOp",EDGE,"E6.1.0.2"),sQuery(id+"F0.wireOp",EDGE,"E6.1.0.3"),subQ9,subQ10,subQ3,subQ1,sQuery(id+"F0.wireOp",EDGE,"E6.3.0.0"),sQuery(id+"F0.wireOp",EDGE,"E6.3.0.1"),sQuery(id+"F0.wireOp",EDGE,"E6.3.0.2"),sQuery(id+"F0.wireOp",EDGE,"E6.3.0.3"),sQuery(id+"F0.wireOp",EDGE,"E6.4.0.0"),sQuery(id+"F0.wireOp",EDGE,"E6.4.0.1"),sQuery(id+"F0.wireOp",EDGE,"E6.4.0.2"),sQuery(id+"F0.wireOp",EDGE,"E6.4.0.3"),sQuery(id+"F0.wireOp",EDGE,"E6.5.0.0"),sQuery(id+"F0.wireOp",EDGE,"E6.5.0.1"),sQuery(id+"F0.wireOp",EDGE,"E6.5.0.2"),sQuery(id+"F0.wireOp",EDGE,"E6.5.0.3"),sQuery(id+"F0.wireOp",EDGE,"E6.6.0.0"),sQuery(id+"F0.wireOp",EDGE,"E6.6.0.1"),sQuery(id+"F0.wireOp",EDGE,"E6.6.0.2"),sQuery(id+"F0.wireOp",EDGE,"E6.6.0.3"),subQ7,subQ5,subQ0,subQ2,subQ11,subQ12,sQuery(id+"F0.wireOp",EDGE,"E13"),sQuery(id+"F0.wireOp",EDGE,"E14"),sQuery(id+"F0.wireOp",EDGE,"E15.trimOffspring"),sQuery(id+"F0.wireOp",EDGE,"E16.trimOffspring"),subQ8,sQuery(id+"F0.wireOp",EDGE,"E18.trimOffspring"),sQuery(id+"F0.wireOp",EDGE,"E19.trimOffspring"),sQuery(id+"F0.wireOp",EDGE,"E20.trimOffspring"),sQuery(id+"F0.wireOp",EDGE,"E21.trimOffspring"),sQuery(id+"F0.wireOp",EDGE,"E22")])],"isStart":false})})],"blendedInto":[makeQuery(id+"F4.boolean.opBoolean","SPLIT",FACE,{"disambiguationData":[TD([makeQuery(id+"F1.opExtrude","SWEPT_FACE",FACE,{"disambiguationData":[OSD([subQ9])]})])],"derivedFrom":makeQuery(id+"F1.opExtrude","CAP_FACE",FACE,{"disambiguationData":[OSD([subQ4,subQ6,sQuery(id+"F0.wireOp",EDGE,"E2"),sQuery(id+"F0.wireOp",EDGE,"E3"),sQuery(id+"F0.wireOp",EDGE,"E4"),sQuery(id+"F0.wireOp",EDGE,"E5"),sQuery(id+"F0.wireOp",EDGE,"E6.1.0.0"),sQuery(id+"F0.wireOp",EDGE,"E6.1.0.1"),sQuery(id+"F0.wireOp",EDGE,"E6.1.0.2"),sQuery(id+"F0.wireOp",EDGE,"E6.1.0.3"),subQ9,subQ10,subQ3,subQ1,sQuery(id+"F0.wireOp",EDGE,"E6.3.0.0"),sQuery(id+"F0.wireOp",EDGE,"E6.3.0.1"),sQuery(id+"F0.wireOp",EDGE,"E6.3.0.2"),sQuery(id+"F0.wireOp",EDGE,"E6.3.0.3"),sQuery(id+"F0.wireOp",EDGE,"E6.4.0.0"),sQuery(id+"F0.wireOp",EDGE,"E6.4.0.1"),sQuery(id+"F0.wireOp",EDGE,"E6.4.0.2"),sQuery(id+"F0.wireOp",EDGE,"E6.4.0.3"),sQuery(id+"F0.wireOp",EDGE,"E6.5.0.0"),sQuery(id+"F0.wireOp",EDGE,"E6.5.0.1"),sQuery(id+"F0.wireOp",EDGE,"E6.5.0.2"),sQuery(id+"F0.wireOp",EDGE,"E6.5.0.3"),sQuery(id+"F0.wireOp",EDGE,"E6.6.0.0"),sQuery(id+"F0.wireOp",EDGE,"E6.6.0.1"),sQuery(id+"F0.wireOp",EDGE,"E6.6.0.2"),sQuery(id+"F0.wireOp",EDGE,"E6.6.0.3"),subQ7,subQ5,subQ0,subQ2,subQ11,subQ12,sQuery(id+"F0.wireOp",EDGE,"E13"),sQuery(id+"F0.wireOp",EDGE,"E14"),sQuery(id+"F0.wireOp",EDGE,"E15.trimOffspring"),sQuery(id+"F0.wireOp",EDGE,"E16.trimOffspring"),subQ8,sQuery(id+"F0.wireOp",EDGE,"E18.trimOffspring"),sQuery(id+"F0.wireOp",EDGE,"E19.trimOffspring"),sQuery(id+"F0.wireOp",EDGE,"E20.trimOffspring"),sQuery(id+"F0.wireOp",EDGE,"E21.trimOffspring"),sQuery(id+"F0.wireOp",EDGE,"E22")])],"isStart":false})})]});}
            var Q18;
            {var subQ0=sQuery(id+"F0.wireOp",EDGE,"E9.trimOffspring");var subQ1=sQuery(id+"F0.wireOp",EDGE,"E6.2.0.3");var subQ2=sQuery(id+"F0.wireOp",EDGE,"E10.trimOffspring");var subQ3=sQuery(id+"F0.wireOp",EDGE,"E6.2.0.2");var subQ4=sQuery(id+"F0.wireOp",EDGE,"E0.0");var subQ5=sQuery(id+"F0.wireOp",EDGE,"E8.trimOffspring");var subQ6=sQuery(id+"F0.wireOp",EDGE,"E1");var subQ7=sQuery(id+"F0.wireOp",EDGE,"E7.trimOffspring");var subQ8=sQuery(id+"F0.wireOp",EDGE,"E17.trimOffspring");var subQ9=sQuery(id+"F0.wireOp",EDGE,"E6.2.0.0");var subQ10=sQuery(id+"F0.wireOp",EDGE,"E6.2.0.1");var subQ11=sQuery(id+"F0.wireOp",EDGE,"E11.trimOffspring");var subQ12=sQuery(id+"F0.wireOp",EDGE,"E12.trimOffspring");Q18=makeQuery(id+"F5.opFillet","BLEND_EDGE",EDGE,{"blendedFrom":[makeQuery(id+"F1.opExtrude","SWEPT_EDGE",EDGE,{"disambiguationData":[OSD([subQ3,subQ1])]}),makeQuery(id+"F4.boolean.opBoolean","SPLIT",FACE,{"disambiguationData":[TD([makeQuery(id+"F1.opExtrude","SWEPT_FACE",FACE,{"disambiguationData":[OSD([subQ9])]})])],"derivedFrom":makeQuery(id+"F1.opExtrude","CAP_FACE",FACE,{"disambiguationData":[OSD([subQ4,subQ6,sQuery(id+"F0.wireOp",EDGE,"E2"),sQuery(id+"F0.wireOp",EDGE,"E3"),sQuery(id+"F0.wireOp",EDGE,"E4"),sQuery(id+"F0.wireOp",EDGE,"E5"),sQuery(id+"F0.wireOp",EDGE,"E6.1.0.0"),sQuery(id+"F0.wireOp",EDGE,"E6.1.0.1"),sQuery(id+"F0.wireOp",EDGE,"E6.1.0.2"),sQuery(id+"F0.wireOp",EDGE,"E6.1.0.3"),subQ9,subQ10,subQ3,subQ1,sQuery(id+"F0.wireOp",EDGE,"E6.3.0.0"),sQuery(id+"F0.wireOp",EDGE,"E6.3.0.1"),sQuery(id+"F0.wireOp",EDGE,"E6.3.0.2"),sQuery(id+"F0.wireOp",EDGE,"E6.3.0.3"),sQuery(id+"F0.wireOp",EDGE,"E6.4.0.0"),sQuery(id+"F0.wireOp",EDGE,"E6.4.0.1"),sQuery(id+"F0.wireOp",EDGE,"E6.4.0.2"),sQuery(id+"F0.wireOp",EDGE,"E6.4.0.3"),sQuery(id+"F0.wireOp",EDGE,"E6.5.0.0"),sQuery(id+"F0.wireOp",EDGE,"E6.5.0.1"),sQuery(id+"F0.wireOp",EDGE,"E6.5.0.2"),sQuery(id+"F0.wireOp",EDGE,"E6.5.0.3"),sQuery(id+"F0.wireOp",EDGE,"E6.6.0.0"),sQuery(id+"F0.wireOp",EDGE,"E6.6.0.1"),sQuery(id+"F0.wireOp",EDGE,"E6.6.0.2"),sQuery(id+"F0.wireOp",EDGE,"E6.6.0.3"),subQ7,subQ5,subQ0,subQ2,subQ11,subQ12,sQuery(id+"F0.wireOp",EDGE,"E13"),sQuery(id+"F0.wireOp",EDGE,"E14"),sQuery(id+"F0.wireOp",EDGE,"E15.trimOffspring"),sQuery(id+"F0.wireOp",EDGE,"E16.trimOffspring"),subQ8,sQuery(id+"F0.wireOp",EDGE,"E18.trimOffspring"),sQuery(id+"F0.wireOp",EDGE,"E19.trimOffspring"),sQuery(id+"F0.wireOp",EDGE,"E20.trimOffspring"),sQuery(id+"F0.wireOp",EDGE,"E21.trimOffspring"),sQuery(id+"F0.wireOp",EDGE,"E22")])],"isStart":false})})],"blendedInto":[makeQuery(id+"F4.boolean.opBoolean","SPLIT",FACE,{"disambiguationData":[TD([makeQuery(id+"F1.opExtrude","SWEPT_FACE",FACE,{"disambiguationData":[OSD([subQ9])]})])],"derivedFrom":makeQuery(id+"F1.opExtrude","CAP_FACE",FACE,{"disambiguationData":[OSD([subQ4,subQ6,sQuery(id+"F0.wireOp",EDGE,"E2"),sQuery(id+"F0.wireOp",EDGE,"E3"),sQuery(id+"F0.wireOp",EDGE,"E4"),sQuery(id+"F0.wireOp",EDGE,"E5"),sQuery(id+"F0.wireOp",EDGE,"E6.1.0.0"),sQuery(id+"F0.wireOp",EDGE,"E6.1.0.1"),sQuery(id+"F0.wireOp",EDGE,"E6.1.0.2"),sQuery(id+"F0.wireOp",EDGE,"E6.1.0.3"),subQ9,subQ10,subQ3,subQ1,sQuery(id+"F0.wireOp",EDGE,"E6.3.0.0"),sQuery(id+"F0.wireOp",EDGE,"E6.3.0.1"),sQuery(id+"F0.wireOp",EDGE,"E6.3.0.2"),sQuery(id+"F0.wireOp",EDGE,"E6.3.0.3"),sQuery(id+"F0.wireOp",EDGE,"E6.4.0.0"),sQuery(id+"F0.wireOp",EDGE,"E6.4.0.1"),sQuery(id+"F0.wireOp",EDGE,"E6.4.0.2"),sQuery(id+"F0.wireOp",EDGE,"E6.4.0.3"),sQuery(id+"F0.wireOp",EDGE,"E6.5.0.0"),sQuery(id+"F0.wireOp",EDGE,"E6.5.0.1"),sQuery(id+"F0.wireOp",EDGE,"E6.5.0.2"),sQuery(id+"F0.wireOp",EDGE,"E6.5.0.3"),sQuery(id+"F0.wireOp",EDGE,"E6.6.0.0"),sQuery(id+"F0.wireOp",EDGE,"E6.6.0.1"),sQuery(id+"F0.wireOp",EDGE,"E6.6.0.2"),sQuery(id+"F0.wireOp",EDGE,"E6.6.0.3"),subQ7,subQ5,subQ0,subQ2,subQ11,subQ12,sQuery(id+"F0.wireOp",EDGE,"E13"),sQuery(id+"F0.wireOp",EDGE,"E14"),sQuery(id+"F0.wireOp",EDGE,"E15.trimOffspring"),sQuery(id+"F0.wireOp",EDGE,"E16.trimOffspring"),subQ8,sQuery(id+"F0.wireOp",EDGE,"E18.trimOffspring"),sQuery(id+"F0.wireOp",EDGE,"E19.trimOffspring"),sQuery(id+"F0.wireOp",EDGE,"E20.trimOffspring"),sQuery(id+"F0.wireOp",EDGE,"E21.trimOffspring"),sQuery(id+"F0.wireOp",EDGE,"E22")])],"isStart":false})})]});}
            var Q19;
            {var subQ0=sQuery(id+"F0.wireOp",EDGE,"E9.trimOffspring");var subQ1=sQuery(id+"F0.wireOp",EDGE,"E6.2.0.3");var subQ2=sQuery(id+"F0.wireOp",EDGE,"E10.trimOffspring");var subQ3=sQuery(id+"F0.wireOp",EDGE,"E6.2.0.2");var subQ4=sQuery(id+"F0.wireOp",EDGE,"E0.0");var subQ5=sQuery(id+"F0.wireOp",EDGE,"E8.trimOffspring");var subQ6=sQuery(id+"F0.wireOp",EDGE,"E1");var subQ7=sQuery(id+"F0.wireOp",EDGE,"E7.trimOffspring");var subQ8=sQuery(id+"F0.wireOp",EDGE,"E17.trimOffspring");var subQ9=sQuery(id+"F0.wireOp",EDGE,"E6.2.0.0");var subQ10=sQuery(id+"F0.wireOp",EDGE,"E6.2.0.1");var subQ11=sQuery(id+"F0.wireOp",EDGE,"E11.trimOffspring");var subQ12=sQuery(id+"F0.wireOp",EDGE,"E12.trimOffspring");Q19=makeQuery(id+"F5.opFillet","BLEND_EDGE",EDGE,{"blendedFrom":[makeQuery(id+"F1.opExtrude","SWEPT_EDGE",EDGE,{"disambiguationData":[OSD([subQ1,subQ8])]}),makeQuery(id+"F4.boolean.opBoolean","SPLIT",FACE,{"disambiguationData":[TD([makeQuery(id+"F1.opExtrude","SWEPT_FACE",FACE,{"disambiguationData":[OSD([subQ9])]})])],"derivedFrom":makeQuery(id+"F1.opExtrude","CAP_FACE",FACE,{"disambiguationData":[OSD([subQ4,subQ6,sQuery(id+"F0.wireOp",EDGE,"E2"),sQuery(id+"F0.wireOp",EDGE,"E3"),sQuery(id+"F0.wireOp",EDGE,"E4"),sQuery(id+"F0.wireOp",EDGE,"E5"),sQuery(id+"F0.wireOp",EDGE,"E6.1.0.0"),sQuery(id+"F0.wireOp",EDGE,"E6.1.0.1"),sQuery(id+"F0.wireOp",EDGE,"E6.1.0.2"),sQuery(id+"F0.wireOp",EDGE,"E6.1.0.3"),subQ9,subQ10,subQ3,subQ1,sQuery(id+"F0.wireOp",EDGE,"E6.3.0.0"),sQuery(id+"F0.wireOp",EDGE,"E6.3.0.1"),sQuery(id+"F0.wireOp",EDGE,"E6.3.0.2"),sQuery(id+"F0.wireOp",EDGE,"E6.3.0.3"),sQuery(id+"F0.wireOp",EDGE,"E6.4.0.0"),sQuery(id+"F0.wireOp",EDGE,"E6.4.0.1"),sQuery(id+"F0.wireOp",EDGE,"E6.4.0.2"),sQuery(id+"F0.wireOp",EDGE,"E6.4.0.3"),sQuery(id+"F0.wireOp",EDGE,"E6.5.0.0"),sQuery(id+"F0.wireOp",EDGE,"E6.5.0.1"),sQuery(id+"F0.wireOp",EDGE,"E6.5.0.2"),sQuery(id+"F0.wireOp",EDGE,"E6.5.0.3"),sQuery(id+"F0.wireOp",EDGE,"E6.6.0.0"),sQuery(id+"F0.wireOp",EDGE,"E6.6.0.1"),sQuery(id+"F0.wireOp",EDGE,"E6.6.0.2"),sQuery(id+"F0.wireOp",EDGE,"E6.6.0.3"),subQ7,subQ5,subQ0,subQ2,subQ11,subQ12,sQuery(id+"F0.wireOp",EDGE,"E13"),sQuery(id+"F0.wireOp",EDGE,"E14"),sQuery(id+"F0.wireOp",EDGE,"E15.trimOffspring"),sQuery(id+"F0.wireOp",EDGE,"E16.trimOffspring"),subQ8,sQuery(id+"F0.wireOp",EDGE,"E18.trimOffspring"),sQuery(id+"F0.wireOp",EDGE,"E19.trimOffspring"),sQuery(id+"F0.wireOp",EDGE,"E20.trimOffspring"),sQuery(id+"F0.wireOp",EDGE,"E21.trimOffspring"),sQuery(id+"F0.wireOp",EDGE,"E22")])],"isStart":false})})],"blendedInto":[makeQuery(id+"F4.boolean.opBoolean","SPLIT",FACE,{"disambiguationData":[TD([makeQuery(id+"F1.opExtrude","SWEPT_FACE",FACE,{"disambiguationData":[OSD([subQ9])]})])],"derivedFrom":makeQuery(id+"F1.opExtrude","CAP_FACE",FACE,{"disambiguationData":[OSD([subQ4,subQ6,sQuery(id+"F0.wireOp",EDGE,"E2"),sQuery(id+"F0.wireOp",EDGE,"E3"),sQuery(id+"F0.wireOp",EDGE,"E4"),sQuery(id+"F0.wireOp",EDGE,"E5"),sQuery(id+"F0.wireOp",EDGE,"E6.1.0.0"),sQuery(id+"F0.wireOp",EDGE,"E6.1.0.1"),sQuery(id+"F0.wireOp",EDGE,"E6.1.0.2"),sQuery(id+"F0.wireOp",EDGE,"E6.1.0.3"),subQ9,subQ10,subQ3,subQ1,sQuery(id+"F0.wireOp",EDGE,"E6.3.0.0"),sQuery(id+"F0.wireOp",EDGE,"E6.3.0.1"),sQuery(id+"F0.wireOp",EDGE,"E6.3.0.2"),sQuery(id+"F0.wireOp",EDGE,"E6.3.0.3"),sQuery(id+"F0.wireOp",EDGE,"E6.4.0.0"),sQuery(id+"F0.wireOp",EDGE,"E6.4.0.1"),sQuery(id+"F0.wireOp",EDGE,"E6.4.0.2"),sQuery(id+"F0.wireOp",EDGE,"E6.4.0.3"),sQuery(id+"F0.wireOp",EDGE,"E6.5.0.0"),sQuery(id+"F0.wireOp",EDGE,"E6.5.0.1"),sQuery(id+"F0.wireOp",EDGE,"E6.5.0.2"),sQuery(id+"F0.wireOp",EDGE,"E6.5.0.3"),sQuery(id+"F0.wireOp",EDGE,"E6.6.0.0"),sQuery(id+"F0.wireOp",EDGE,"E6.6.0.1"),sQuery(id+"F0.wireOp",EDGE,"E6.6.0.2"),sQuery(id+"F0.wireOp",EDGE,"E6.6.0.3"),subQ7,subQ5,subQ0,subQ2,subQ11,subQ12,sQuery(id+"F0.wireOp",EDGE,"E13"),sQuery(id+"F0.wireOp",EDGE,"E14"),sQuery(id+"F0.wireOp",EDGE,"E15.trimOffspring"),sQuery(id+"F0.wireOp",EDGE,"E16.trimOffspring"),subQ8,sQuery(id+"F0.wireOp",EDGE,"E18.trimOffspring"),sQuery(id+"F0.wireOp",EDGE,"E19.trimOffspring"),sQuery(id+"F0.wireOp",EDGE,"E20.trimOffspring"),sQuery(id+"F0.wireOp",EDGE,"E21.trimOffspring"),sQuery(id+"F0.wireOp",EDGE,"E22")])],"isStart":false})})]});}
            var Q20;
            Q20=makeQuery(id+"F1.opExtrude","CAP_EDGE",EDGE,{"disambiguationData":[OSD([sQuery(id+"F0.wireOp",EDGE,"E17.trimOffspring")])],"isStart":false});
            var Q21;
            Q21=makeQuery(id+"F1.opExtrude","CAP_EDGE",EDGE,{"disambiguationData":[OSD([sQuery(id+"F0.wireOp",EDGE,"E6.3.0.1")])],"isStart":false});
            var Q22;
            {var subQ0=sQuery(id+"F0.wireOp",EDGE,"E10.trimOffspring");var subQ1=sQuery(id+"F0.wireOp",EDGE,"E6.3.0.2");var subQ2=sQuery(id+"F0.wireOp",EDGE,"E8.trimOffspring");var subQ3=sQuery(id+"F0.wireOp",EDGE,"E0.0");var subQ4=sQuery(id+"F0.wireOp",EDGE,"E18.trimOffspring");var subQ5=sQuery(id+"F0.wireOp",EDGE,"E7.trimOffspring");var subQ6=sQuery(id+"F0.wireOp",EDGE,"E9.trimOffspring");var subQ7=sQuery(id+"F0.wireOp",EDGE,"E6.3.0.1");var subQ8=sQuery(id+"F0.wireOp",EDGE,"E6.3.0.0");var subQ9=sQuery(id+"F0.wireOp",EDGE,"E6.3.0.3");var subQ10=sQuery(id+"F0.wireOp",EDGE,"E1");var subQ11=sQuery(id+"F0.wireOp",EDGE,"E11.trimOffspring");var subQ12=sQuery(id+"F0.wireOp",EDGE,"E12.trimOffspring");Q22=makeQuery(id+"F5.opFillet","BLEND_EDGE",EDGE,{"blendedFrom":[makeQuery(id+"F1.opExtrude","SWEPT_EDGE",EDGE,{"disambiguationData":[OSD([subQ8,subQ7])]}),makeQuery(id+"F4.boolean.opBoolean","SPLIT",FACE,{"disambiguationData":[TD([makeQuery(id+"F1.opExtrude","SWEPT_FACE",FACE,{"disambiguationData":[OSD([subQ8])]})])],"derivedFrom":makeQuery(id+"F1.opExtrude","CAP_FACE",FACE,{"disambiguationData":[OSD([subQ3,subQ10,sQuery(id+"F0.wireOp",EDGE,"E2"),sQuery(id+"F0.wireOp",EDGE,"E3"),sQuery(id+"F0.wireOp",EDGE,"E4"),sQuery(id+"F0.wireOp",EDGE,"E5"),sQuery(id+"F0.wireOp",EDGE,"E6.1.0.0"),sQuery(id+"F0.wireOp",EDGE,"E6.1.0.1"),sQuery(id+"F0.wireOp",EDGE,"E6.1.0.2"),sQuery(id+"F0.wireOp",EDGE,"E6.1.0.3"),sQuery(id+"F0.wireOp",EDGE,"E6.2.0.0"),sQuery(id+"F0.wireOp",EDGE,"E6.2.0.1"),sQuery(id+"F0.wireOp",EDGE,"E6.2.0.2"),sQuery(id+"F0.wireOp",EDGE,"E6.2.0.3"),subQ8,subQ7,subQ1,subQ9,sQuery(id+"F0.wireOp",EDGE,"E6.4.0.0"),sQuery(id+"F0.wireOp",EDGE,"E6.4.0.1"),sQuery(id+"F0.wireOp",EDGE,"E6.4.0.2"),sQuery(id+"F0.wireOp",EDGE,"E6.4.0.3"),sQuery(id+"F0.wireOp",EDGE,"E6.5.0.0"),sQuery(id+"F0.wireOp",EDGE,"E6.5.0.1"),sQuery(id+"F0.wireOp",EDGE,"E6.5.0.2"),sQuery(id+"F0.wireOp",EDGE,"E6.5.0.3"),sQuery(id+"F0.wireOp",EDGE,"E6.6.0.0"),sQuery(id+"F0.wireOp",EDGE,"E6.6.0.1"),sQuery(id+"F0.wireOp",EDGE,"E6.6.0.2"),sQuery(id+"F0.wireOp",EDGE,"E6.6.0.3"),subQ5,subQ2,subQ6,subQ0,subQ11,subQ12,sQuery(id+"F0.wireOp",EDGE,"E13"),sQuery(id+"F0.wireOp",EDGE,"E14"),sQuery(id+"F0.wireOp",EDGE,"E15.trimOffspring"),sQuery(id+"F0.wireOp",EDGE,"E16.trimOffspring"),sQuery(id+"F0.wireOp",EDGE,"E17.trimOffspring"),subQ4,sQuery(id+"F0.wireOp",EDGE,"E19.trimOffspring"),sQuery(id+"F0.wireOp",EDGE,"E20.trimOffspring"),sQuery(id+"F0.wireOp",EDGE,"E21.trimOffspring"),sQuery(id+"F0.wireOp",EDGE,"E22")])],"isStart":false})})],"blendedInto":[makeQuery(id+"F4.boolean.opBoolean","SPLIT",FACE,{"disambiguationData":[TD([makeQuery(id+"F1.opExtrude","SWEPT_FACE",FACE,{"disambiguationData":[OSD([subQ8])]})])],"derivedFrom":makeQuery(id+"F1.opExtrude","CAP_FACE",FACE,{"disambiguationData":[OSD([subQ3,subQ10,sQuery(id+"F0.wireOp",EDGE,"E2"),sQuery(id+"F0.wireOp",EDGE,"E3"),sQuery(id+"F0.wireOp",EDGE,"E4"),sQuery(id+"F0.wireOp",EDGE,"E5"),sQuery(id+"F0.wireOp",EDGE,"E6.1.0.0"),sQuery(id+"F0.wireOp",EDGE,"E6.1.0.1"),sQuery(id+"F0.wireOp",EDGE,"E6.1.0.2"),sQuery(id+"F0.wireOp",EDGE,"E6.1.0.3"),sQuery(id+"F0.wireOp",EDGE,"E6.2.0.0"),sQuery(id+"F0.wireOp",EDGE,"E6.2.0.1"),sQuery(id+"F0.wireOp",EDGE,"E6.2.0.2"),sQuery(id+"F0.wireOp",EDGE,"E6.2.0.3"),subQ8,subQ7,subQ1,subQ9,sQuery(id+"F0.wireOp",EDGE,"E6.4.0.0"),sQuery(id+"F0.wireOp",EDGE,"E6.4.0.1"),sQuery(id+"F0.wireOp",EDGE,"E6.4.0.2"),sQuery(id+"F0.wireOp",EDGE,"E6.4.0.3"),sQuery(id+"F0.wireOp",EDGE,"E6.5.0.0"),sQuery(id+"F0.wireOp",EDGE,"E6.5.0.1"),sQuery(id+"F0.wireOp",EDGE,"E6.5.0.2"),sQuery(id+"F0.wireOp",EDGE,"E6.5.0.3"),sQuery(id+"F0.wireOp",EDGE,"E6.6.0.0"),sQuery(id+"F0.wireOp",EDGE,"E6.6.0.1"),sQuery(id+"F0.wireOp",EDGE,"E6.6.0.2"),sQuery(id+"F0.wireOp",EDGE,"E6.6.0.3"),subQ5,subQ2,subQ6,subQ0,subQ11,subQ12,sQuery(id+"F0.wireOp",EDGE,"E13"),sQuery(id+"F0.wireOp",EDGE,"E14"),sQuery(id+"F0.wireOp",EDGE,"E15.trimOffspring"),sQuery(id+"F0.wireOp",EDGE,"E16.trimOffspring"),sQuery(id+"F0.wireOp",EDGE,"E17.trimOffspring"),subQ4,sQuery(id+"F0.wireOp",EDGE,"E19.trimOffspring"),sQuery(id+"F0.wireOp",EDGE,"E20.trimOffspring"),sQuery(id+"F0.wireOp",EDGE,"E21.trimOffspring"),sQuery(id+"F0.wireOp",EDGE,"E22")])],"isStart":false})})]});}
            var Q23;
            {var subQ0=sQuery(id+"F0.wireOp",EDGE,"E10.trimOffspring");var subQ1=sQuery(id+"F0.wireOp",EDGE,"E6.3.0.2");var subQ2=sQuery(id+"F0.wireOp",EDGE,"E8.trimOffspring");var subQ3=sQuery(id+"F0.wireOp",EDGE,"E0.0");var subQ4=sQuery(id+"F0.wireOp",EDGE,"E18.trimOffspring");var subQ5=sQuery(id+"F0.wireOp",EDGE,"E7.trimOffspring");var subQ6=sQuery(id+"F0.wireOp",EDGE,"E9.trimOffspring");var subQ7=sQuery(id+"F0.wireOp",EDGE,"E6.3.0.1");var subQ8=sQuery(id+"F0.wireOp",EDGE,"E6.3.0.0");var subQ9=sQuery(id+"F0.wireOp",EDGE,"E6.3.0.3");var subQ10=sQuery(id+"F0.wireOp",EDGE,"E1");var subQ11=sQuery(id+"F0.wireOp",EDGE,"E11.trimOffspring");var subQ12=sQuery(id+"F0.wireOp",EDGE,"E12.trimOffspring");Q23=makeQuery(id+"F5.opFillet","BLEND_EDGE",EDGE,{"blendedFrom":[makeQuery(id+"F1.opExtrude","SWEPT_EDGE",EDGE,{"disambiguationData":[OSD([subQ8,subQ1])]}),makeQuery(id+"F4.boolean.opBoolean","SPLIT",FACE,{"disambiguationData":[TD([makeQuery(id+"F1.opExtrude","SWEPT_FACE",FACE,{"disambiguationData":[OSD([subQ8])]})])],"derivedFrom":makeQuery(id+"F1.opExtrude","CAP_FACE",FACE,{"disambiguationData":[OSD([subQ3,subQ10,sQuery(id+"F0.wireOp",EDGE,"E2"),sQuery(id+"F0.wireOp",EDGE,"E3"),sQuery(id+"F0.wireOp",EDGE,"E4"),sQuery(id+"F0.wireOp",EDGE,"E5"),sQuery(id+"F0.wireOp",EDGE,"E6.1.0.0"),sQuery(id+"F0.wireOp",EDGE,"E6.1.0.1"),sQuery(id+"F0.wireOp",EDGE,"E6.1.0.2"),sQuery(id+"F0.wireOp",EDGE,"E6.1.0.3"),sQuery(id+"F0.wireOp",EDGE,"E6.2.0.0"),sQuery(id+"F0.wireOp",EDGE,"E6.2.0.1"),sQuery(id+"F0.wireOp",EDGE,"E6.2.0.2"),sQuery(id+"F0.wireOp",EDGE,"E6.2.0.3"),subQ8,subQ7,subQ1,subQ9,sQuery(id+"F0.wireOp",EDGE,"E6.4.0.0"),sQuery(id+"F0.wireOp",EDGE,"E6.4.0.1"),sQuery(id+"F0.wireOp",EDGE,"E6.4.0.2"),sQuery(id+"F0.wireOp",EDGE,"E6.4.0.3"),sQuery(id+"F0.wireOp",EDGE,"E6.5.0.0"),sQuery(id+"F0.wireOp",EDGE,"E6.5.0.1"),sQuery(id+"F0.wireOp",EDGE,"E6.5.0.2"),sQuery(id+"F0.wireOp",EDGE,"E6.5.0.3"),sQuery(id+"F0.wireOp",EDGE,"E6.6.0.0"),sQuery(id+"F0.wireOp",EDGE,"E6.6.0.1"),sQuery(id+"F0.wireOp",EDGE,"E6.6.0.2"),sQuery(id+"F0.wireOp",EDGE,"E6.6.0.3"),subQ5,subQ2,subQ6,subQ0,subQ11,subQ12,sQuery(id+"F0.wireOp",EDGE,"E13"),sQuery(id+"F0.wireOp",EDGE,"E14"),sQuery(id+"F0.wireOp",EDGE,"E15.trimOffspring"),sQuery(id+"F0.wireOp",EDGE,"E16.trimOffspring"),sQuery(id+"F0.wireOp",EDGE,"E17.trimOffspring"),subQ4,sQuery(id+"F0.wireOp",EDGE,"E19.trimOffspring"),sQuery(id+"F0.wireOp",EDGE,"E20.trimOffspring"),sQuery(id+"F0.wireOp",EDGE,"E21.trimOffspring"),sQuery(id+"F0.wireOp",EDGE,"E22")])],"isStart":false})})],"blendedInto":[makeQuery(id+"F4.boolean.opBoolean","SPLIT",FACE,{"disambiguationData":[TD([makeQuery(id+"F1.opExtrude","SWEPT_FACE",FACE,{"disambiguationData":[OSD([subQ8])]})])],"derivedFrom":makeQuery(id+"F1.opExtrude","CAP_FACE",FACE,{"disambiguationData":[OSD([subQ3,subQ10,sQuery(id+"F0.wireOp",EDGE,"E2"),sQuery(id+"F0.wireOp",EDGE,"E3"),sQuery(id+"F0.wireOp",EDGE,"E4"),sQuery(id+"F0.wireOp",EDGE,"E5"),sQuery(id+"F0.wireOp",EDGE,"E6.1.0.0"),sQuery(id+"F0.wireOp",EDGE,"E6.1.0.1"),sQuery(id+"F0.wireOp",EDGE,"E6.1.0.2"),sQuery(id+"F0.wireOp",EDGE,"E6.1.0.3"),sQuery(id+"F0.wireOp",EDGE,"E6.2.0.0"),sQuery(id+"F0.wireOp",EDGE,"E6.2.0.1"),sQuery(id+"F0.wireOp",EDGE,"E6.2.0.2"),sQuery(id+"F0.wireOp",EDGE,"E6.2.0.3"),subQ8,subQ7,subQ1,subQ9,sQuery(id+"F0.wireOp",EDGE,"E6.4.0.0"),sQuery(id+"F0.wireOp",EDGE,"E6.4.0.1"),sQuery(id+"F0.wireOp",EDGE,"E6.4.0.2"),sQuery(id+"F0.wireOp",EDGE,"E6.4.0.3"),sQuery(id+"F0.wireOp",EDGE,"E6.5.0.0"),sQuery(id+"F0.wireOp",EDGE,"E6.5.0.1"),sQuery(id+"F0.wireOp",EDGE,"E6.5.0.2"),sQuery(id+"F0.wireOp",EDGE,"E6.5.0.3"),sQuery(id+"F0.wireOp",EDGE,"E6.6.0.0"),sQuery(id+"F0.wireOp",EDGE,"E6.6.0.1"),sQuery(id+"F0.wireOp",EDGE,"E6.6.0.2"),sQuery(id+"F0.wireOp",EDGE,"E6.6.0.3"),subQ5,subQ2,subQ6,subQ0,subQ11,subQ12,sQuery(id+"F0.wireOp",EDGE,"E13"),sQuery(id+"F0.wireOp",EDGE,"E14"),sQuery(id+"F0.wireOp",EDGE,"E15.trimOffspring"),sQuery(id+"F0.wireOp",EDGE,"E16.trimOffspring"),sQuery(id+"F0.wireOp",EDGE,"E17.trimOffspring"),subQ4,sQuery(id+"F0.wireOp",EDGE,"E19.trimOffspring"),sQuery(id+"F0.wireOp",EDGE,"E20.trimOffspring"),sQuery(id+"F0.wireOp",EDGE,"E21.trimOffspring"),sQuery(id+"F0.wireOp",EDGE,"E22")])],"isStart":false})})]});}
            var Q24;
            Q24=makeQuery(id+"F1.opExtrude","CAP_EDGE",EDGE,{"disambiguationData":[OSD([sQuery(id+"F0.wireOp",EDGE,"E6.3.0.2")])],"isStart":false});
            var Q25;
            {var subQ0=sQuery(id+"F0.wireOp",EDGE,"E10.trimOffspring");var subQ1=sQuery(id+"F0.wireOp",EDGE,"E6.3.0.2");var subQ2=sQuery(id+"F0.wireOp",EDGE,"E8.trimOffspring");var subQ3=sQuery(id+"F0.wireOp",EDGE,"E0.0");var subQ4=sQuery(id+"F0.wireOp",EDGE,"E18.trimOffspring");var subQ5=sQuery(id+"F0.wireOp",EDGE,"E7.trimOffspring");var subQ6=sQuery(id+"F0.wireOp",EDGE,"E9.trimOffspring");var subQ7=sQuery(id+"F0.wireOp",EDGE,"E6.3.0.1");var subQ8=sQuery(id+"F0.wireOp",EDGE,"E6.3.0.0");var subQ9=sQuery(id+"F0.wireOp",EDGE,"E6.3.0.3");var subQ10=sQuery(id+"F0.wireOp",EDGE,"E1");var subQ11=sQuery(id+"F0.wireOp",EDGE,"E11.trimOffspring");var subQ12=sQuery(id+"F0.wireOp",EDGE,"E12.trimOffspring");Q25=makeQuery(id+"F5.opFillet","BLEND_EDGE",EDGE,{"blendedFrom":[makeQuery(id+"F1.opExtrude","SWEPT_EDGE",EDGE,{"disambiguationData":[OSD([subQ1,subQ9])]}),makeQuery(id+"F4.boolean.opBoolean","SPLIT",FACE,{"disambiguationData":[TD([makeQuery(id+"F1.opExtrude","SWEPT_FACE",FACE,{"disambiguationData":[OSD([subQ8])]})])],"derivedFrom":makeQuery(id+"F1.opExtrude","CAP_FACE",FACE,{"disambiguationData":[OSD([subQ3,subQ10,sQuery(id+"F0.wireOp",EDGE,"E2"),sQuery(id+"F0.wireOp",EDGE,"E3"),sQuery(id+"F0.wireOp",EDGE,"E4"),sQuery(id+"F0.wireOp",EDGE,"E5"),sQuery(id+"F0.wireOp",EDGE,"E6.1.0.0"),sQuery(id+"F0.wireOp",EDGE,"E6.1.0.1"),sQuery(id+"F0.wireOp",EDGE,"E6.1.0.2"),sQuery(id+"F0.wireOp",EDGE,"E6.1.0.3"),sQuery(id+"F0.wireOp",EDGE,"E6.2.0.0"),sQuery(id+"F0.wireOp",EDGE,"E6.2.0.1"),sQuery(id+"F0.wireOp",EDGE,"E6.2.0.2"),sQuery(id+"F0.wireOp",EDGE,"E6.2.0.3"),subQ8,subQ7,subQ1,subQ9,sQuery(id+"F0.wireOp",EDGE,"E6.4.0.0"),sQuery(id+"F0.wireOp",EDGE,"E6.4.0.1"),sQuery(id+"F0.wireOp",EDGE,"E6.4.0.2"),sQuery(id+"F0.wireOp",EDGE,"E6.4.0.3"),sQuery(id+"F0.wireOp",EDGE,"E6.5.0.0"),sQuery(id+"F0.wireOp",EDGE,"E6.5.0.1"),sQuery(id+"F0.wireOp",EDGE,"E6.5.0.2"),sQuery(id+"F0.wireOp",EDGE,"E6.5.0.3"),sQuery(id+"F0.wireOp",EDGE,"E6.6.0.0"),sQuery(id+"F0.wireOp",EDGE,"E6.6.0.1"),sQuery(id+"F0.wireOp",EDGE,"E6.6.0.2"),sQuery(id+"F0.wireOp",EDGE,"E6.6.0.3"),subQ5,subQ2,subQ6,subQ0,subQ11,subQ12,sQuery(id+"F0.wireOp",EDGE,"E13"),sQuery(id+"F0.wireOp",EDGE,"E14"),sQuery(id+"F0.wireOp",EDGE,"E15.trimOffspring"),sQuery(id+"F0.wireOp",EDGE,"E16.trimOffspring"),sQuery(id+"F0.wireOp",EDGE,"E17.trimOffspring"),subQ4,sQuery(id+"F0.wireOp",EDGE,"E19.trimOffspring"),sQuery(id+"F0.wireOp",EDGE,"E20.trimOffspring"),sQuery(id+"F0.wireOp",EDGE,"E21.trimOffspring"),sQuery(id+"F0.wireOp",EDGE,"E22")])],"isStart":false})})],"blendedInto":[makeQuery(id+"F4.boolean.opBoolean","SPLIT",FACE,{"disambiguationData":[TD([makeQuery(id+"F1.opExtrude","SWEPT_FACE",FACE,{"disambiguationData":[OSD([subQ8])]})])],"derivedFrom":makeQuery(id+"F1.opExtrude","CAP_FACE",FACE,{"disambiguationData":[OSD([subQ3,subQ10,sQuery(id+"F0.wireOp",EDGE,"E2"),sQuery(id+"F0.wireOp",EDGE,"E3"),sQuery(id+"F0.wireOp",EDGE,"E4"),sQuery(id+"F0.wireOp",EDGE,"E5"),sQuery(id+"F0.wireOp",EDGE,"E6.1.0.0"),sQuery(id+"F0.wireOp",EDGE,"E6.1.0.1"),sQuery(id+"F0.wireOp",EDGE,"E6.1.0.2"),sQuery(id+"F0.wireOp",EDGE,"E6.1.0.3"),sQuery(id+"F0.wireOp",EDGE,"E6.2.0.0"),sQuery(id+"F0.wireOp",EDGE,"E6.2.0.1"),sQuery(id+"F0.wireOp",EDGE,"E6.2.0.2"),sQuery(id+"F0.wireOp",EDGE,"E6.2.0.3"),subQ8,subQ7,subQ1,subQ9,sQuery(id+"F0.wireOp",EDGE,"E6.4.0.0"),sQuery(id+"F0.wireOp",EDGE,"E6.4.0.1"),sQuery(id+"F0.wireOp",EDGE,"E6.4.0.2"),sQuery(id+"F0.wireOp",EDGE,"E6.4.0.3"),sQuery(id+"F0.wireOp",EDGE,"E6.5.0.0"),sQuery(id+"F0.wireOp",EDGE,"E6.5.0.1"),sQuery(id+"F0.wireOp",EDGE,"E6.5.0.2"),sQuery(id+"F0.wireOp",EDGE,"E6.5.0.3"),sQuery(id+"F0.wireOp",EDGE,"E6.6.0.0"),sQuery(id+"F0.wireOp",EDGE,"E6.6.0.1"),sQuery(id+"F0.wireOp",EDGE,"E6.6.0.2"),sQuery(id+"F0.wireOp",EDGE,"E6.6.0.3"),subQ5,subQ2,subQ6,subQ0,subQ11,subQ12,sQuery(id+"F0.wireOp",EDGE,"E13"),sQuery(id+"F0.wireOp",EDGE,"E14"),sQuery(id+"F0.wireOp",EDGE,"E15.trimOffspring"),sQuery(id+"F0.wireOp",EDGE,"E16.trimOffspring"),sQuery(id+"F0.wireOp",EDGE,"E17.trimOffspring"),subQ4,sQuery(id+"F0.wireOp",EDGE,"E19.trimOffspring"),sQuery(id+"F0.wireOp",EDGE,"E20.trimOffspring"),sQuery(id+"F0.wireOp",EDGE,"E21.trimOffspring"),sQuery(id+"F0.wireOp",EDGE,"E22")])],"isStart":false})})]});}
            var Q26;
            Q26=makeQuery(id+"F1.opExtrude","CAP_EDGE",EDGE,{"disambiguationData":[OSD([sQuery(id+"F0.wireOp",EDGE,"E18.trimOffspring")])],"isStart":false});
            var Q27;
            {var subQ0=sQuery(id+"F0.wireOp",EDGE,"E10.trimOffspring");var subQ1=sQuery(id+"F0.wireOp",EDGE,"E6.3.0.2");var subQ2=sQuery(id+"F0.wireOp",EDGE,"E8.trimOffspring");var subQ3=sQuery(id+"F0.wireOp",EDGE,"E0.0");var subQ4=sQuery(id+"F0.wireOp",EDGE,"E18.trimOffspring");var subQ5=sQuery(id+"F0.wireOp",EDGE,"E7.trimOffspring");var subQ6=sQuery(id+"F0.wireOp",EDGE,"E9.trimOffspring");var subQ7=sQuery(id+"F0.wireOp",EDGE,"E6.3.0.1");var subQ8=sQuery(id+"F0.wireOp",EDGE,"E6.3.0.0");var subQ9=sQuery(id+"F0.wireOp",EDGE,"E6.3.0.3");var subQ10=sQuery(id+"F0.wireOp",EDGE,"E1");var subQ11=sQuery(id+"F0.wireOp",EDGE,"E11.trimOffspring");var subQ12=sQuery(id+"F0.wireOp",EDGE,"E12.trimOffspring");Q27=makeQuery(id+"F5.opFillet","BLEND_EDGE",EDGE,{"blendedFrom":[makeQuery(id+"F1.opExtrude","SWEPT_EDGE",EDGE,{"disambiguationData":[OSD([subQ9,subQ4])]}),makeQuery(id+"F4.boolean.opBoolean","SPLIT",FACE,{"disambiguationData":[TD([makeQuery(id+"F1.opExtrude","SWEPT_FACE",FACE,{"disambiguationData":[OSD([subQ8])]})])],"derivedFrom":makeQuery(id+"F1.opExtrude","CAP_FACE",FACE,{"disambiguationData":[OSD([subQ3,subQ10,sQuery(id+"F0.wireOp",EDGE,"E2"),sQuery(id+"F0.wireOp",EDGE,"E3"),sQuery(id+"F0.wireOp",EDGE,"E4"),sQuery(id+"F0.wireOp",EDGE,"E5"),sQuery(id+"F0.wireOp",EDGE,"E6.1.0.0"),sQuery(id+"F0.wireOp",EDGE,"E6.1.0.1"),sQuery(id+"F0.wireOp",EDGE,"E6.1.0.2"),sQuery(id+"F0.wireOp",EDGE,"E6.1.0.3"),sQuery(id+"F0.wireOp",EDGE,"E6.2.0.0"),sQuery(id+"F0.wireOp",EDGE,"E6.2.0.1"),sQuery(id+"F0.wireOp",EDGE,"E6.2.0.2"),sQuery(id+"F0.wireOp",EDGE,"E6.2.0.3"),subQ8,subQ7,subQ1,subQ9,sQuery(id+"F0.wireOp",EDGE,"E6.4.0.0"),sQuery(id+"F0.wireOp",EDGE,"E6.4.0.1"),sQuery(id+"F0.wireOp",EDGE,"E6.4.0.2"),sQuery(id+"F0.wireOp",EDGE,"E6.4.0.3"),sQuery(id+"F0.wireOp",EDGE,"E6.5.0.0"),sQuery(id+"F0.wireOp",EDGE,"E6.5.0.1"),sQuery(id+"F0.wireOp",EDGE,"E6.5.0.2"),sQuery(id+"F0.wireOp",EDGE,"E6.5.0.3"),sQuery(id+"F0.wireOp",EDGE,"E6.6.0.0"),sQuery(id+"F0.wireOp",EDGE,"E6.6.0.1"),sQuery(id+"F0.wireOp",EDGE,"E6.6.0.2"),sQuery(id+"F0.wireOp",EDGE,"E6.6.0.3"),subQ5,subQ2,subQ6,subQ0,subQ11,subQ12,sQuery(id+"F0.wireOp",EDGE,"E13"),sQuery(id+"F0.wireOp",EDGE,"E14"),sQuery(id+"F0.wireOp",EDGE,"E15.trimOffspring"),sQuery(id+"F0.wireOp",EDGE,"E16.trimOffspring"),sQuery(id+"F0.wireOp",EDGE,"E17.trimOffspring"),subQ4,sQuery(id+"F0.wireOp",EDGE,"E19.trimOffspring"),sQuery(id+"F0.wireOp",EDGE,"E20.trimOffspring"),sQuery(id+"F0.wireOp",EDGE,"E21.trimOffspring"),sQuery(id+"F0.wireOp",EDGE,"E22")])],"isStart":false})})],"blendedInto":[makeQuery(id+"F4.boolean.opBoolean","SPLIT",FACE,{"disambiguationData":[TD([makeQuery(id+"F1.opExtrude","SWEPT_FACE",FACE,{"disambiguationData":[OSD([subQ8])]})])],"derivedFrom":makeQuery(id+"F1.opExtrude","CAP_FACE",FACE,{"disambiguationData":[OSD([subQ3,subQ10,sQuery(id+"F0.wireOp",EDGE,"E2"),sQuery(id+"F0.wireOp",EDGE,"E3"),sQuery(id+"F0.wireOp",EDGE,"E4"),sQuery(id+"F0.wireOp",EDGE,"E5"),sQuery(id+"F0.wireOp",EDGE,"E6.1.0.0"),sQuery(id+"F0.wireOp",EDGE,"E6.1.0.1"),sQuery(id+"F0.wireOp",EDGE,"E6.1.0.2"),sQuery(id+"F0.wireOp",EDGE,"E6.1.0.3"),sQuery(id+"F0.wireOp",EDGE,"E6.2.0.0"),sQuery(id+"F0.wireOp",EDGE,"E6.2.0.1"),sQuery(id+"F0.wireOp",EDGE,"E6.2.0.2"),sQuery(id+"F0.wireOp",EDGE,"E6.2.0.3"),subQ8,subQ7,subQ1,subQ9,sQuery(id+"F0.wireOp",EDGE,"E6.4.0.0"),sQuery(id+"F0.wireOp",EDGE,"E6.4.0.1"),sQuery(id+"F0.wireOp",EDGE,"E6.4.0.2"),sQuery(id+"F0.wireOp",EDGE,"E6.4.0.3"),sQuery(id+"F0.wireOp",EDGE,"E6.5.0.0"),sQuery(id+"F0.wireOp",EDGE,"E6.5.0.1"),sQuery(id+"F0.wireOp",EDGE,"E6.5.0.2"),sQuery(id+"F0.wireOp",EDGE,"E6.5.0.3"),sQuery(id+"F0.wireOp",EDGE,"E6.6.0.0"),sQuery(id+"F0.wireOp",EDGE,"E6.6.0.1"),sQuery(id+"F0.wireOp",EDGE,"E6.6.0.2"),sQuery(id+"F0.wireOp",EDGE,"E6.6.0.3"),subQ5,subQ2,subQ6,subQ0,subQ11,subQ12,sQuery(id+"F0.wireOp",EDGE,"E13"),sQuery(id+"F0.wireOp",EDGE,"E14"),sQuery(id+"F0.wireOp",EDGE,"E15.trimOffspring"),sQuery(id+"F0.wireOp",EDGE,"E16.trimOffspring"),sQuery(id+"F0.wireOp",EDGE,"E17.trimOffspring"),subQ4,sQuery(id+"F0.wireOp",EDGE,"E19.trimOffspring"),sQuery(id+"F0.wireOp",EDGE,"E20.trimOffspring"),sQuery(id+"F0.wireOp",EDGE,"E21.trimOffspring"),sQuery(id+"F0.wireOp",EDGE,"E22")])],"isStart":false})})]});}
            var Q28;
            Q28=makeQuery(id+"F1.opExtrude","CAP_EDGE",EDGE,{"disambiguationData":[OSD([sQuery(id+"F0.wireOp",EDGE,"E6.4.0.1")])],"isStart":false});
            var Q29;
            {var subQ0=sQuery(id+"F0.wireOp",EDGE,"E9.trimOffspring");var subQ1=sQuery(id+"F0.wireOp",EDGE,"E7.trimOffspring");var subQ2=sQuery(id+"F0.wireOp",EDGE,"E10.trimOffspring");var subQ3=sQuery(id+"F0.wireOp",EDGE,"E6.4.0.3");var subQ4=sQuery(id+"F0.wireOp",EDGE,"E0.0");var subQ5=sQuery(id+"F0.wireOp",EDGE,"E8.trimOffspring");var subQ6=sQuery(id+"F0.wireOp",EDGE,"E6.4.0.2");var subQ7=sQuery(id+"F0.wireOp",EDGE,"E1");var subQ8=sQuery(id+"F0.wireOp",EDGE,"E6.4.0.0");var subQ9=sQuery(id+"F0.wireOp",EDGE,"E6.4.0.1");var subQ10=sQuery(id+"F0.wireOp",EDGE,"E11.trimOffspring");var subQ11=sQuery(id+"F0.wireOp",EDGE,"E12.trimOffspring");var subQ12=sQuery(id+"F0.wireOp",EDGE,"E19.trimOffspring");Q29=makeQuery(id+"F5.opFillet","BLEND_EDGE",EDGE,{"blendedFrom":[makeQuery(id+"F1.opExtrude","SWEPT_EDGE",EDGE,{"disambiguationData":[OSD([subQ8,subQ9])]}),makeQuery(id+"F4.boolean.opBoolean","SPLIT",FACE,{"disambiguationData":[TD([makeQuery(id+"F1.opExtrude","SWEPT_FACE",FACE,{"disambiguationData":[OSD([subQ8])]})])],"derivedFrom":makeQuery(id+"F1.opExtrude","CAP_FACE",FACE,{"disambiguationData":[OSD([subQ4,subQ7,sQuery(id+"F0.wireOp",EDGE,"E2"),sQuery(id+"F0.wireOp",EDGE,"E3"),sQuery(id+"F0.wireOp",EDGE,"E4"),sQuery(id+"F0.wireOp",EDGE,"E5"),sQuery(id+"F0.wireOp",EDGE,"E6.1.0.0"),sQuery(id+"F0.wireOp",EDGE,"E6.1.0.1"),sQuery(id+"F0.wireOp",EDGE,"E6.1.0.2"),sQuery(id+"F0.wireOp",EDGE,"E6.1.0.3"),sQuery(id+"F0.wireOp",EDGE,"E6.2.0.0"),sQuery(id+"F0.wireOp",EDGE,"E6.2.0.1"),sQuery(id+"F0.wireOp",EDGE,"E6.2.0.2"),sQuery(id+"F0.wireOp",EDGE,"E6.2.0.3"),sQuery(id+"F0.wireOp",EDGE,"E6.3.0.0"),sQuery(id+"F0.wireOp",EDGE,"E6.3.0.1"),sQuery(id+"F0.wireOp",EDGE,"E6.3.0.2"),sQuery(id+"F0.wireOp",EDGE,"E6.3.0.3"),subQ8,subQ9,subQ6,subQ3,sQuery(id+"F0.wireOp",EDGE,"E6.5.0.0"),sQuery(id+"F0.wireOp",EDGE,"E6.5.0.1"),sQuery(id+"F0.wireOp",EDGE,"E6.5.0.2"),sQuery(id+"F0.wireOp",EDGE,"E6.5.0.3"),sQuery(id+"F0.wireOp",EDGE,"E6.6.0.0"),sQuery(id+"F0.wireOp",EDGE,"E6.6.0.1"),sQuery(id+"F0.wireOp",EDGE,"E6.6.0.2"),sQuery(id+"F0.wireOp",EDGE,"E6.6.0.3"),subQ1,subQ5,subQ0,subQ2,subQ10,subQ11,sQuery(id+"F0.wireOp",EDGE,"E13"),sQuery(id+"F0.wireOp",EDGE,"E14"),sQuery(id+"F0.wireOp",EDGE,"E15.trimOffspring"),sQuery(id+"F0.wireOp",EDGE,"E16.trimOffspring"),sQuery(id+"F0.wireOp",EDGE,"E17.trimOffspring"),sQuery(id+"F0.wireOp",EDGE,"E18.trimOffspring"),subQ12,sQuery(id+"F0.wireOp",EDGE,"E20.trimOffspring"),sQuery(id+"F0.wireOp",EDGE,"E21.trimOffspring"),sQuery(id+"F0.wireOp",EDGE,"E22")])],"isStart":false})})],"blendedInto":[makeQuery(id+"F4.boolean.opBoolean","SPLIT",FACE,{"disambiguationData":[TD([makeQuery(id+"F1.opExtrude","SWEPT_FACE",FACE,{"disambiguationData":[OSD([subQ8])]})])],"derivedFrom":makeQuery(id+"F1.opExtrude","CAP_FACE",FACE,{"disambiguationData":[OSD([subQ4,subQ7,sQuery(id+"F0.wireOp",EDGE,"E2"),sQuery(id+"F0.wireOp",EDGE,"E3"),sQuery(id+"F0.wireOp",EDGE,"E4"),sQuery(id+"F0.wireOp",EDGE,"E5"),sQuery(id+"F0.wireOp",EDGE,"E6.1.0.0"),sQuery(id+"F0.wireOp",EDGE,"E6.1.0.1"),sQuery(id+"F0.wireOp",EDGE,"E6.1.0.2"),sQuery(id+"F0.wireOp",EDGE,"E6.1.0.3"),sQuery(id+"F0.wireOp",EDGE,"E6.2.0.0"),sQuery(id+"F0.wireOp",EDGE,"E6.2.0.1"),sQuery(id+"F0.wireOp",EDGE,"E6.2.0.2"),sQuery(id+"F0.wireOp",EDGE,"E6.2.0.3"),sQuery(id+"F0.wireOp",EDGE,"E6.3.0.0"),sQuery(id+"F0.wireOp",EDGE,"E6.3.0.1"),sQuery(id+"F0.wireOp",EDGE,"E6.3.0.2"),sQuery(id+"F0.wireOp",EDGE,"E6.3.0.3"),subQ8,subQ9,subQ6,subQ3,sQuery(id+"F0.wireOp",EDGE,"E6.5.0.0"),sQuery(id+"F0.wireOp",EDGE,"E6.5.0.1"),sQuery(id+"F0.wireOp",EDGE,"E6.5.0.2"),sQuery(id+"F0.wireOp",EDGE,"E6.5.0.3"),sQuery(id+"F0.wireOp",EDGE,"E6.6.0.0"),sQuery(id+"F0.wireOp",EDGE,"E6.6.0.1"),sQuery(id+"F0.wireOp",EDGE,"E6.6.0.2"),sQuery(id+"F0.wireOp",EDGE,"E6.6.0.3"),subQ1,subQ5,subQ0,subQ2,subQ10,subQ11,sQuery(id+"F0.wireOp",EDGE,"E13"),sQuery(id+"F0.wireOp",EDGE,"E14"),sQuery(id+"F0.wireOp",EDGE,"E15.trimOffspring"),sQuery(id+"F0.wireOp",EDGE,"E16.trimOffspring"),sQuery(id+"F0.wireOp",EDGE,"E17.trimOffspring"),sQuery(id+"F0.wireOp",EDGE,"E18.trimOffspring"),subQ12,sQuery(id+"F0.wireOp",EDGE,"E20.trimOffspring"),sQuery(id+"F0.wireOp",EDGE,"E21.trimOffspring"),sQuery(id+"F0.wireOp",EDGE,"E22")])],"isStart":false})})]});}
            var Q30;
            {var subQ0=sQuery(id+"F0.wireOp",EDGE,"E9.trimOffspring");var subQ1=sQuery(id+"F0.wireOp",EDGE,"E7.trimOffspring");var subQ2=sQuery(id+"F0.wireOp",EDGE,"E10.trimOffspring");var subQ3=sQuery(id+"F0.wireOp",EDGE,"E6.4.0.3");var subQ4=sQuery(id+"F0.wireOp",EDGE,"E0.0");var subQ5=sQuery(id+"F0.wireOp",EDGE,"E8.trimOffspring");var subQ6=sQuery(id+"F0.wireOp",EDGE,"E6.4.0.2");var subQ7=sQuery(id+"F0.wireOp",EDGE,"E1");var subQ8=sQuery(id+"F0.wireOp",EDGE,"E6.4.0.0");var subQ9=sQuery(id+"F0.wireOp",EDGE,"E6.4.0.1");var subQ10=sQuery(id+"F0.wireOp",EDGE,"E11.trimOffspring");var subQ11=sQuery(id+"F0.wireOp",EDGE,"E12.trimOffspring");var subQ12=sQuery(id+"F0.wireOp",EDGE,"E19.trimOffspring");Q30=makeQuery(id+"F5.opFillet","BLEND_EDGE",EDGE,{"blendedFrom":[makeQuery(id+"F1.opExtrude","SWEPT_EDGE",EDGE,{"disambiguationData":[OSD([subQ8,subQ6])]}),makeQuery(id+"F4.boolean.opBoolean","SPLIT",FACE,{"disambiguationData":[TD([makeQuery(id+"F1.opExtrude","SWEPT_FACE",FACE,{"disambiguationData":[OSD([subQ8])]})])],"derivedFrom":makeQuery(id+"F1.opExtrude","CAP_FACE",FACE,{"disambiguationData":[OSD([subQ4,subQ7,sQuery(id+"F0.wireOp",EDGE,"E2"),sQuery(id+"F0.wireOp",EDGE,"E3"),sQuery(id+"F0.wireOp",EDGE,"E4"),sQuery(id+"F0.wireOp",EDGE,"E5"),sQuery(id+"F0.wireOp",EDGE,"E6.1.0.0"),sQuery(id+"F0.wireOp",EDGE,"E6.1.0.1"),sQuery(id+"F0.wireOp",EDGE,"E6.1.0.2"),sQuery(id+"F0.wireOp",EDGE,"E6.1.0.3"),sQuery(id+"F0.wireOp",EDGE,"E6.2.0.0"),sQuery(id+"F0.wireOp",EDGE,"E6.2.0.1"),sQuery(id+"F0.wireOp",EDGE,"E6.2.0.2"),sQuery(id+"F0.wireOp",EDGE,"E6.2.0.3"),sQuery(id+"F0.wireOp",EDGE,"E6.3.0.0"),sQuery(id+"F0.wireOp",EDGE,"E6.3.0.1"),sQuery(id+"F0.wireOp",EDGE,"E6.3.0.2"),sQuery(id+"F0.wireOp",EDGE,"E6.3.0.3"),subQ8,subQ9,subQ6,subQ3,sQuery(id+"F0.wireOp",EDGE,"E6.5.0.0"),sQuery(id+"F0.wireOp",EDGE,"E6.5.0.1"),sQuery(id+"F0.wireOp",EDGE,"E6.5.0.2"),sQuery(id+"F0.wireOp",EDGE,"E6.5.0.3"),sQuery(id+"F0.wireOp",EDGE,"E6.6.0.0"),sQuery(id+"F0.wireOp",EDGE,"E6.6.0.1"),sQuery(id+"F0.wireOp",EDGE,"E6.6.0.2"),sQuery(id+"F0.wireOp",EDGE,"E6.6.0.3"),subQ1,subQ5,subQ0,subQ2,subQ10,subQ11,sQuery(id+"F0.wireOp",EDGE,"E13"),sQuery(id+"F0.wireOp",EDGE,"E14"),sQuery(id+"F0.wireOp",EDGE,"E15.trimOffspring"),sQuery(id+"F0.wireOp",EDGE,"E16.trimOffspring"),sQuery(id+"F0.wireOp",EDGE,"E17.trimOffspring"),sQuery(id+"F0.wireOp",EDGE,"E18.trimOffspring"),subQ12,sQuery(id+"F0.wireOp",EDGE,"E20.trimOffspring"),sQuery(id+"F0.wireOp",EDGE,"E21.trimOffspring"),sQuery(id+"F0.wireOp",EDGE,"E22")])],"isStart":false})})],"blendedInto":[makeQuery(id+"F4.boolean.opBoolean","SPLIT",FACE,{"disambiguationData":[TD([makeQuery(id+"F1.opExtrude","SWEPT_FACE",FACE,{"disambiguationData":[OSD([subQ8])]})])],"derivedFrom":makeQuery(id+"F1.opExtrude","CAP_FACE",FACE,{"disambiguationData":[OSD([subQ4,subQ7,sQuery(id+"F0.wireOp",EDGE,"E2"),sQuery(id+"F0.wireOp",EDGE,"E3"),sQuery(id+"F0.wireOp",EDGE,"E4"),sQuery(id+"F0.wireOp",EDGE,"E5"),sQuery(id+"F0.wireOp",EDGE,"E6.1.0.0"),sQuery(id+"F0.wireOp",EDGE,"E6.1.0.1"),sQuery(id+"F0.wireOp",EDGE,"E6.1.0.2"),sQuery(id+"F0.wireOp",EDGE,"E6.1.0.3"),sQuery(id+"F0.wireOp",EDGE,"E6.2.0.0"),sQuery(id+"F0.wireOp",EDGE,"E6.2.0.1"),sQuery(id+"F0.wireOp",EDGE,"E6.2.0.2"),sQuery(id+"F0.wireOp",EDGE,"E6.2.0.3"),sQuery(id+"F0.wireOp",EDGE,"E6.3.0.0"),sQuery(id+"F0.wireOp",EDGE,"E6.3.0.1"),sQuery(id+"F0.wireOp",EDGE,"E6.3.0.2"),sQuery(id+"F0.wireOp",EDGE,"E6.3.0.3"),subQ8,subQ9,subQ6,subQ3,sQuery(id+"F0.wireOp",EDGE,"E6.5.0.0"),sQuery(id+"F0.wireOp",EDGE,"E6.5.0.1"),sQuery(id+"F0.wireOp",EDGE,"E6.5.0.2"),sQuery(id+"F0.wireOp",EDGE,"E6.5.0.3"),sQuery(id+"F0.wireOp",EDGE,"E6.6.0.0"),sQuery(id+"F0.wireOp",EDGE,"E6.6.0.1"),sQuery(id+"F0.wireOp",EDGE,"E6.6.0.2"),sQuery(id+"F0.wireOp",EDGE,"E6.6.0.3"),subQ1,subQ5,subQ0,subQ2,subQ10,subQ11,sQuery(id+"F0.wireOp",EDGE,"E13"),sQuery(id+"F0.wireOp",EDGE,"E14"),sQuery(id+"F0.wireOp",EDGE,"E15.trimOffspring"),sQuery(id+"F0.wireOp",EDGE,"E16.trimOffspring"),sQuery(id+"F0.wireOp",EDGE,"E17.trimOffspring"),sQuery(id+"F0.wireOp",EDGE,"E18.trimOffspring"),subQ12,sQuery(id+"F0.wireOp",EDGE,"E20.trimOffspring"),sQuery(id+"F0.wireOp",EDGE,"E21.trimOffspring"),sQuery(id+"F0.wireOp",EDGE,"E22")])],"isStart":false})})]});}
            var Q31;
            Q31=makeQuery(id+"F1.opExtrude","CAP_EDGE",EDGE,{"disambiguationData":[OSD([sQuery(id+"F0.wireOp",EDGE,"E6.4.0.2")])],"isStart":false});
            var Q32;
            {var subQ0=sQuery(id+"F0.wireOp",EDGE,"E9.trimOffspring");var subQ1=sQuery(id+"F0.wireOp",EDGE,"E7.trimOffspring");var subQ2=sQuery(id+"F0.wireOp",EDGE,"E10.trimOffspring");var subQ3=sQuery(id+"F0.wireOp",EDGE,"E6.4.0.3");var subQ4=sQuery(id+"F0.wireOp",EDGE,"E0.0");var subQ5=sQuery(id+"F0.wireOp",EDGE,"E8.trimOffspring");var subQ6=sQuery(id+"F0.wireOp",EDGE,"E6.4.0.2");var subQ7=sQuery(id+"F0.wireOp",EDGE,"E1");var subQ8=sQuery(id+"F0.wireOp",EDGE,"E6.4.0.0");var subQ9=sQuery(id+"F0.wireOp",EDGE,"E6.4.0.1");var subQ10=sQuery(id+"F0.wireOp",EDGE,"E11.trimOffspring");var subQ11=sQuery(id+"F0.wireOp",EDGE,"E12.trimOffspring");var subQ12=sQuery(id+"F0.wireOp",EDGE,"E19.trimOffspring");Q32=makeQuery(id+"F5.opFillet","BLEND_EDGE",EDGE,{"blendedFrom":[makeQuery(id+"F1.opExtrude","SWEPT_EDGE",EDGE,{"disambiguationData":[OSD([subQ6,subQ3])]}),makeQuery(id+"F4.boolean.opBoolean","SPLIT",FACE,{"disambiguationData":[TD([makeQuery(id+"F1.opExtrude","SWEPT_FACE",FACE,{"disambiguationData":[OSD([subQ8])]})])],"derivedFrom":makeQuery(id+"F1.opExtrude","CAP_FACE",FACE,{"disambiguationData":[OSD([subQ4,subQ7,sQuery(id+"F0.wireOp",EDGE,"E2"),sQuery(id+"F0.wireOp",EDGE,"E3"),sQuery(id+"F0.wireOp",EDGE,"E4"),sQuery(id+"F0.wireOp",EDGE,"E5"),sQuery(id+"F0.wireOp",EDGE,"E6.1.0.0"),sQuery(id+"F0.wireOp",EDGE,"E6.1.0.1"),sQuery(id+"F0.wireOp",EDGE,"E6.1.0.2"),sQuery(id+"F0.wireOp",EDGE,"E6.1.0.3"),sQuery(id+"F0.wireOp",EDGE,"E6.2.0.0"),sQuery(id+"F0.wireOp",EDGE,"E6.2.0.1"),sQuery(id+"F0.wireOp",EDGE,"E6.2.0.2"),sQuery(id+"F0.wireOp",EDGE,"E6.2.0.3"),sQuery(id+"F0.wireOp",EDGE,"E6.3.0.0"),sQuery(id+"F0.wireOp",EDGE,"E6.3.0.1"),sQuery(id+"F0.wireOp",EDGE,"E6.3.0.2"),sQuery(id+"F0.wireOp",EDGE,"E6.3.0.3"),subQ8,subQ9,subQ6,subQ3,sQuery(id+"F0.wireOp",EDGE,"E6.5.0.0"),sQuery(id+"F0.wireOp",EDGE,"E6.5.0.1"),sQuery(id+"F0.wireOp",EDGE,"E6.5.0.2"),sQuery(id+"F0.wireOp",EDGE,"E6.5.0.3"),sQuery(id+"F0.wireOp",EDGE,"E6.6.0.0"),sQuery(id+"F0.wireOp",EDGE,"E6.6.0.1"),sQuery(id+"F0.wireOp",EDGE,"E6.6.0.2"),sQuery(id+"F0.wireOp",EDGE,"E6.6.0.3"),subQ1,subQ5,subQ0,subQ2,subQ10,subQ11,sQuery(id+"F0.wireOp",EDGE,"E13"),sQuery(id+"F0.wireOp",EDGE,"E14"),sQuery(id+"F0.wireOp",EDGE,"E15.trimOffspring"),sQuery(id+"F0.wireOp",EDGE,"E16.trimOffspring"),sQuery(id+"F0.wireOp",EDGE,"E17.trimOffspring"),sQuery(id+"F0.wireOp",EDGE,"E18.trimOffspring"),subQ12,sQuery(id+"F0.wireOp",EDGE,"E20.trimOffspring"),sQuery(id+"F0.wireOp",EDGE,"E21.trimOffspring"),sQuery(id+"F0.wireOp",EDGE,"E22")])],"isStart":false})})],"blendedInto":[makeQuery(id+"F4.boolean.opBoolean","SPLIT",FACE,{"disambiguationData":[TD([makeQuery(id+"F1.opExtrude","SWEPT_FACE",FACE,{"disambiguationData":[OSD([subQ8])]})])],"derivedFrom":makeQuery(id+"F1.opExtrude","CAP_FACE",FACE,{"disambiguationData":[OSD([subQ4,subQ7,sQuery(id+"F0.wireOp",EDGE,"E2"),sQuery(id+"F0.wireOp",EDGE,"E3"),sQuery(id+"F0.wireOp",EDGE,"E4"),sQuery(id+"F0.wireOp",EDGE,"E5"),sQuery(id+"F0.wireOp",EDGE,"E6.1.0.0"),sQuery(id+"F0.wireOp",EDGE,"E6.1.0.1"),sQuery(id+"F0.wireOp",EDGE,"E6.1.0.2"),sQuery(id+"F0.wireOp",EDGE,"E6.1.0.3"),sQuery(id+"F0.wireOp",EDGE,"E6.2.0.0"),sQuery(id+"F0.wireOp",EDGE,"E6.2.0.1"),sQuery(id+"F0.wireOp",EDGE,"E6.2.0.2"),sQuery(id+"F0.wireOp",EDGE,"E6.2.0.3"),sQuery(id+"F0.wireOp",EDGE,"E6.3.0.0"),sQuery(id+"F0.wireOp",EDGE,"E6.3.0.1"),sQuery(id+"F0.wireOp",EDGE,"E6.3.0.2"),sQuery(id+"F0.wireOp",EDGE,"E6.3.0.3"),subQ8,subQ9,subQ6,subQ3,sQuery(id+"F0.wireOp",EDGE,"E6.5.0.0"),sQuery(id+"F0.wireOp",EDGE,"E6.5.0.1"),sQuery(id+"F0.wireOp",EDGE,"E6.5.0.2"),sQuery(id+"F0.wireOp",EDGE,"E6.5.0.3"),sQuery(id+"F0.wireOp",EDGE,"E6.6.0.0"),sQuery(id+"F0.wireOp",EDGE,"E6.6.0.1"),sQuery(id+"F0.wireOp",EDGE,"E6.6.0.2"),sQuery(id+"F0.wireOp",EDGE,"E6.6.0.3"),subQ1,subQ5,subQ0,subQ2,subQ10,subQ11,sQuery(id+"F0.wireOp",EDGE,"E13"),sQuery(id+"F0.wireOp",EDGE,"E14"),sQuery(id+"F0.wireOp",EDGE,"E15.trimOffspring"),sQuery(id+"F0.wireOp",EDGE,"E16.trimOffspring"),sQuery(id+"F0.wireOp",EDGE,"E17.trimOffspring"),sQuery(id+"F0.wireOp",EDGE,"E18.trimOffspring"),subQ12,sQuery(id+"F0.wireOp",EDGE,"E20.trimOffspring"),sQuery(id+"F0.wireOp",EDGE,"E21.trimOffspring"),sQuery(id+"F0.wireOp",EDGE,"E22")])],"isStart":false})})]});}
            var Q33;
            {var subQ0=sQuery(id+"F0.wireOp",EDGE,"E9.trimOffspring");var subQ1=sQuery(id+"F0.wireOp",EDGE,"E7.trimOffspring");var subQ2=sQuery(id+"F0.wireOp",EDGE,"E10.trimOffspring");var subQ3=sQuery(id+"F0.wireOp",EDGE,"E6.4.0.3");var subQ4=sQuery(id+"F0.wireOp",EDGE,"E0.0");var subQ5=sQuery(id+"F0.wireOp",EDGE,"E8.trimOffspring");var subQ6=sQuery(id+"F0.wireOp",EDGE,"E6.4.0.2");var subQ7=sQuery(id+"F0.wireOp",EDGE,"E1");var subQ8=sQuery(id+"F0.wireOp",EDGE,"E6.4.0.0");var subQ9=sQuery(id+"F0.wireOp",EDGE,"E6.4.0.1");var subQ10=sQuery(id+"F0.wireOp",EDGE,"E11.trimOffspring");var subQ11=sQuery(id+"F0.wireOp",EDGE,"E12.trimOffspring");var subQ12=sQuery(id+"F0.wireOp",EDGE,"E19.trimOffspring");Q33=makeQuery(id+"F5.opFillet","BLEND_EDGE",EDGE,{"blendedFrom":[makeQuery(id+"F1.opExtrude","SWEPT_EDGE",EDGE,{"disambiguationData":[OSD([subQ3,subQ12])]}),makeQuery(id+"F4.boolean.opBoolean","SPLIT",FACE,{"disambiguationData":[TD([makeQuery(id+"F1.opExtrude","SWEPT_FACE",FACE,{"disambiguationData":[OSD([subQ8])]})])],"derivedFrom":makeQuery(id+"F1.opExtrude","CAP_FACE",FACE,{"disambiguationData":[OSD([subQ4,subQ7,sQuery(id+"F0.wireOp",EDGE,"E2"),sQuery(id+"F0.wireOp",EDGE,"E3"),sQuery(id+"F0.wireOp",EDGE,"E4"),sQuery(id+"F0.wireOp",EDGE,"E5"),sQuery(id+"F0.wireOp",EDGE,"E6.1.0.0"),sQuery(id+"F0.wireOp",EDGE,"E6.1.0.1"),sQuery(id+"F0.wireOp",EDGE,"E6.1.0.2"),sQuery(id+"F0.wireOp",EDGE,"E6.1.0.3"),sQuery(id+"F0.wireOp",EDGE,"E6.2.0.0"),sQuery(id+"F0.wireOp",EDGE,"E6.2.0.1"),sQuery(id+"F0.wireOp",EDGE,"E6.2.0.2"),sQuery(id+"F0.wireOp",EDGE,"E6.2.0.3"),sQuery(id+"F0.wireOp",EDGE,"E6.3.0.0"),sQuery(id+"F0.wireOp",EDGE,"E6.3.0.1"),sQuery(id+"F0.wireOp",EDGE,"E6.3.0.2"),sQuery(id+"F0.wireOp",EDGE,"E6.3.0.3"),subQ8,subQ9,subQ6,subQ3,sQuery(id+"F0.wireOp",EDGE,"E6.5.0.0"),sQuery(id+"F0.wireOp",EDGE,"E6.5.0.1"),sQuery(id+"F0.wireOp",EDGE,"E6.5.0.2"),sQuery(id+"F0.wireOp",EDGE,"E6.5.0.3"),sQuery(id+"F0.wireOp",EDGE,"E6.6.0.0"),sQuery(id+"F0.wireOp",EDGE,"E6.6.0.1"),sQuery(id+"F0.wireOp",EDGE,"E6.6.0.2"),sQuery(id+"F0.wireOp",EDGE,"E6.6.0.3"),subQ1,subQ5,subQ0,subQ2,subQ10,subQ11,sQuery(id+"F0.wireOp",EDGE,"E13"),sQuery(id+"F0.wireOp",EDGE,"E14"),sQuery(id+"F0.wireOp",EDGE,"E15.trimOffspring"),sQuery(id+"F0.wireOp",EDGE,"E16.trimOffspring"),sQuery(id+"F0.wireOp",EDGE,"E17.trimOffspring"),sQuery(id+"F0.wireOp",EDGE,"E18.trimOffspring"),subQ12,sQuery(id+"F0.wireOp",EDGE,"E20.trimOffspring"),sQuery(id+"F0.wireOp",EDGE,"E21.trimOffspring"),sQuery(id+"F0.wireOp",EDGE,"E22")])],"isStart":false})})],"blendedInto":[makeQuery(id+"F4.boolean.opBoolean","SPLIT",FACE,{"disambiguationData":[TD([makeQuery(id+"F1.opExtrude","SWEPT_FACE",FACE,{"disambiguationData":[OSD([subQ8])]})])],"derivedFrom":makeQuery(id+"F1.opExtrude","CAP_FACE",FACE,{"disambiguationData":[OSD([subQ4,subQ7,sQuery(id+"F0.wireOp",EDGE,"E2"),sQuery(id+"F0.wireOp",EDGE,"E3"),sQuery(id+"F0.wireOp",EDGE,"E4"),sQuery(id+"F0.wireOp",EDGE,"E5"),sQuery(id+"F0.wireOp",EDGE,"E6.1.0.0"),sQuery(id+"F0.wireOp",EDGE,"E6.1.0.1"),sQuery(id+"F0.wireOp",EDGE,"E6.1.0.2"),sQuery(id+"F0.wireOp",EDGE,"E6.1.0.3"),sQuery(id+"F0.wireOp",EDGE,"E6.2.0.0"),sQuery(id+"F0.wireOp",EDGE,"E6.2.0.1"),sQuery(id+"F0.wireOp",EDGE,"E6.2.0.2"),sQuery(id+"F0.wireOp",EDGE,"E6.2.0.3"),sQuery(id+"F0.wireOp",EDGE,"E6.3.0.0"),sQuery(id+"F0.wireOp",EDGE,"E6.3.0.1"),sQuery(id+"F0.wireOp",EDGE,"E6.3.0.2"),sQuery(id+"F0.wireOp",EDGE,"E6.3.0.3"),subQ8,subQ9,subQ6,subQ3,sQuery(id+"F0.wireOp",EDGE,"E6.5.0.0"),sQuery(id+"F0.wireOp",EDGE,"E6.5.0.1"),sQuery(id+"F0.wireOp",EDGE,"E6.5.0.2"),sQuery(id+"F0.wireOp",EDGE,"E6.5.0.3"),sQuery(id+"F0.wireOp",EDGE,"E6.6.0.0"),sQuery(id+"F0.wireOp",EDGE,"E6.6.0.1"),sQuery(id+"F0.wireOp",EDGE,"E6.6.0.2"),sQuery(id+"F0.wireOp",EDGE,"E6.6.0.3"),subQ1,subQ5,subQ0,subQ2,subQ10,subQ11,sQuery(id+"F0.wireOp",EDGE,"E13"),sQuery(id+"F0.wireOp",EDGE,"E14"),sQuery(id+"F0.wireOp",EDGE,"E15.trimOffspring"),sQuery(id+"F0.wireOp",EDGE,"E16.trimOffspring"),sQuery(id+"F0.wireOp",EDGE,"E17.trimOffspring"),sQuery(id+"F0.wireOp",EDGE,"E18.trimOffspring"),subQ12,sQuery(id+"F0.wireOp",EDGE,"E20.trimOffspring"),sQuery(id+"F0.wireOp",EDGE,"E21.trimOffspring"),sQuery(id+"F0.wireOp",EDGE,"E22")])],"isStart":false})})]});}
            var Q34;
            Q34=makeQuery(id+"F1.opExtrude","CAP_EDGE",EDGE,{"disambiguationData":[OSD([sQuery(id+"F0.wireOp",EDGE,"E19.trimOffspring")])],"isStart":false});
            var Q35;
            Q35=makeQuery(id+"F1.opExtrude","CAP_EDGE",EDGE,{"disambiguationData":[OSD([sQuery(id+"F0.wireOp",EDGE,"E6.5.0.1")])],"isStart":false});
            var Q36;
            {var subQ0=sQuery(id+"F0.wireOp",EDGE,"E8.trimOffspring");var subQ1=sQuery(id+"F0.wireOp",EDGE,"E6.5.0.2");var subQ2=sQuery(id+"F0.wireOp",EDGE,"E0.0");var subQ3=sQuery(id+"F0.wireOp",EDGE,"E6.5.0.3");var subQ4=sQuery(id+"F0.wireOp",EDGE,"E9.trimOffspring");var subQ5=sQuery(id+"F0.wireOp",EDGE,"E10.trimOffspring");var subQ6=sQuery(id+"F0.wireOp",EDGE,"E1");var subQ7=sQuery(id+"F0.wireOp",EDGE,"E7.trimOffspring");var subQ8=sQuery(id+"F0.wireOp",EDGE,"E6.5.0.1");var subQ9=sQuery(id+"F0.wireOp",EDGE,"E6.5.0.0");var subQ10=sQuery(id+"F0.wireOp",EDGE,"E11.trimOffspring");var subQ11=sQuery(id+"F0.wireOp",EDGE,"E12.trimOffspring");var subQ12=sQuery(id+"F0.wireOp",EDGE,"E20.trimOffspring");Q36=makeQuery(id+"F5.opFillet","BLEND_EDGE",EDGE,{"blendedFrom":[makeQuery(id+"F1.opExtrude","SWEPT_EDGE",EDGE,{"disambiguationData":[OSD([subQ9,subQ8])]}),makeQuery(id+"F4.boolean.opBoolean","SPLIT",FACE,{"disambiguationData":[TD([makeQuery(id+"F1.opExtrude","SWEPT_FACE",FACE,{"disambiguationData":[OSD([subQ9])]})])],"derivedFrom":makeQuery(id+"F1.opExtrude","CAP_FACE",FACE,{"disambiguationData":[OSD([subQ2,subQ6,sQuery(id+"F0.wireOp",EDGE,"E2"),sQuery(id+"F0.wireOp",EDGE,"E3"),sQuery(id+"F0.wireOp",EDGE,"E4"),sQuery(id+"F0.wireOp",EDGE,"E5"),sQuery(id+"F0.wireOp",EDGE,"E6.1.0.0"),sQuery(id+"F0.wireOp",EDGE,"E6.1.0.1"),sQuery(id+"F0.wireOp",EDGE,"E6.1.0.2"),sQuery(id+"F0.wireOp",EDGE,"E6.1.0.3"),sQuery(id+"F0.wireOp",EDGE,"E6.2.0.0"),sQuery(id+"F0.wireOp",EDGE,"E6.2.0.1"),sQuery(id+"F0.wireOp",EDGE,"E6.2.0.2"),sQuery(id+"F0.wireOp",EDGE,"E6.2.0.3"),sQuery(id+"F0.wireOp",EDGE,"E6.3.0.0"),sQuery(id+"F0.wireOp",EDGE,"E6.3.0.1"),sQuery(id+"F0.wireOp",EDGE,"E6.3.0.2"),sQuery(id+"F0.wireOp",EDGE,"E6.3.0.3"),sQuery(id+"F0.wireOp",EDGE,"E6.4.0.0"),sQuery(id+"F0.wireOp",EDGE,"E6.4.0.1"),sQuery(id+"F0.wireOp",EDGE,"E6.4.0.2"),sQuery(id+"F0.wireOp",EDGE,"E6.4.0.3"),subQ9,subQ8,subQ1,subQ3,sQuery(id+"F0.wireOp",EDGE,"E6.6.0.0"),sQuery(id+"F0.wireOp",EDGE,"E6.6.0.1"),sQuery(id+"F0.wireOp",EDGE,"E6.6.0.2"),sQuery(id+"F0.wireOp",EDGE,"E6.6.0.3"),subQ7,subQ0,subQ4,subQ5,subQ10,subQ11,sQuery(id+"F0.wireOp",EDGE,"E13"),sQuery(id+"F0.wireOp",EDGE,"E14"),sQuery(id+"F0.wireOp",EDGE,"E15.trimOffspring"),sQuery(id+"F0.wireOp",EDGE,"E16.trimOffspring"),sQuery(id+"F0.wireOp",EDGE,"E17.trimOffspring"),sQuery(id+"F0.wireOp",EDGE,"E18.trimOffspring"),sQuery(id+"F0.wireOp",EDGE,"E19.trimOffspring"),subQ12,sQuery(id+"F0.wireOp",EDGE,"E21.trimOffspring"),sQuery(id+"F0.wireOp",EDGE,"E22")])],"isStart":false})})],"blendedInto":[makeQuery(id+"F4.boolean.opBoolean","SPLIT",FACE,{"disambiguationData":[TD([makeQuery(id+"F1.opExtrude","SWEPT_FACE",FACE,{"disambiguationData":[OSD([subQ9])]})])],"derivedFrom":makeQuery(id+"F1.opExtrude","CAP_FACE",FACE,{"disambiguationData":[OSD([subQ2,subQ6,sQuery(id+"F0.wireOp",EDGE,"E2"),sQuery(id+"F0.wireOp",EDGE,"E3"),sQuery(id+"F0.wireOp",EDGE,"E4"),sQuery(id+"F0.wireOp",EDGE,"E5"),sQuery(id+"F0.wireOp",EDGE,"E6.1.0.0"),sQuery(id+"F0.wireOp",EDGE,"E6.1.0.1"),sQuery(id+"F0.wireOp",EDGE,"E6.1.0.2"),sQuery(id+"F0.wireOp",EDGE,"E6.1.0.3"),sQuery(id+"F0.wireOp",EDGE,"E6.2.0.0"),sQuery(id+"F0.wireOp",EDGE,"E6.2.0.1"),sQuery(id+"F0.wireOp",EDGE,"E6.2.0.2"),sQuery(id+"F0.wireOp",EDGE,"E6.2.0.3"),sQuery(id+"F0.wireOp",EDGE,"E6.3.0.0"),sQuery(id+"F0.wireOp",EDGE,"E6.3.0.1"),sQuery(id+"F0.wireOp",EDGE,"E6.3.0.2"),sQuery(id+"F0.wireOp",EDGE,"E6.3.0.3"),sQuery(id+"F0.wireOp",EDGE,"E6.4.0.0"),sQuery(id+"F0.wireOp",EDGE,"E6.4.0.1"),sQuery(id+"F0.wireOp",EDGE,"E6.4.0.2"),sQuery(id+"F0.wireOp",EDGE,"E6.4.0.3"),subQ9,subQ8,subQ1,subQ3,sQuery(id+"F0.wireOp",EDGE,"E6.6.0.0"),sQuery(id+"F0.wireOp",EDGE,"E6.6.0.1"),sQuery(id+"F0.wireOp",EDGE,"E6.6.0.2"),sQuery(id+"F0.wireOp",EDGE,"E6.6.0.3"),subQ7,subQ0,subQ4,subQ5,subQ10,subQ11,sQuery(id+"F0.wireOp",EDGE,"E13"),sQuery(id+"F0.wireOp",EDGE,"E14"),sQuery(id+"F0.wireOp",EDGE,"E15.trimOffspring"),sQuery(id+"F0.wireOp",EDGE,"E16.trimOffspring"),sQuery(id+"F0.wireOp",EDGE,"E17.trimOffspring"),sQuery(id+"F0.wireOp",EDGE,"E18.trimOffspring"),sQuery(id+"F0.wireOp",EDGE,"E19.trimOffspring"),subQ12,sQuery(id+"F0.wireOp",EDGE,"E21.trimOffspring"),sQuery(id+"F0.wireOp",EDGE,"E22")])],"isStart":false})})]});}
            var Q37;
            {var subQ0=sQuery(id+"F0.wireOp",EDGE,"E8.trimOffspring");var subQ1=sQuery(id+"F0.wireOp",EDGE,"E6.5.0.2");var subQ2=sQuery(id+"F0.wireOp",EDGE,"E0.0");var subQ3=sQuery(id+"F0.wireOp",EDGE,"E6.5.0.3");var subQ4=sQuery(id+"F0.wireOp",EDGE,"E9.trimOffspring");var subQ5=sQuery(id+"F0.wireOp",EDGE,"E10.trimOffspring");var subQ6=sQuery(id+"F0.wireOp",EDGE,"E1");var subQ7=sQuery(id+"F0.wireOp",EDGE,"E7.trimOffspring");var subQ8=sQuery(id+"F0.wireOp",EDGE,"E6.5.0.1");var subQ9=sQuery(id+"F0.wireOp",EDGE,"E6.5.0.0");var subQ10=sQuery(id+"F0.wireOp",EDGE,"E11.trimOffspring");var subQ11=sQuery(id+"F0.wireOp",EDGE,"E12.trimOffspring");var subQ12=sQuery(id+"F0.wireOp",EDGE,"E20.trimOffspring");Q37=makeQuery(id+"F5.opFillet","BLEND_EDGE",EDGE,{"blendedFrom":[makeQuery(id+"F1.opExtrude","SWEPT_EDGE",EDGE,{"disambiguationData":[OSD([subQ9,subQ1])]}),makeQuery(id+"F4.boolean.opBoolean","SPLIT",FACE,{"disambiguationData":[TD([makeQuery(id+"F1.opExtrude","SWEPT_FACE",FACE,{"disambiguationData":[OSD([subQ9])]})])],"derivedFrom":makeQuery(id+"F1.opExtrude","CAP_FACE",FACE,{"disambiguationData":[OSD([subQ2,subQ6,sQuery(id+"F0.wireOp",EDGE,"E2"),sQuery(id+"F0.wireOp",EDGE,"E3"),sQuery(id+"F0.wireOp",EDGE,"E4"),sQuery(id+"F0.wireOp",EDGE,"E5"),sQuery(id+"F0.wireOp",EDGE,"E6.1.0.0"),sQuery(id+"F0.wireOp",EDGE,"E6.1.0.1"),sQuery(id+"F0.wireOp",EDGE,"E6.1.0.2"),sQuery(id+"F0.wireOp",EDGE,"E6.1.0.3"),sQuery(id+"F0.wireOp",EDGE,"E6.2.0.0"),sQuery(id+"F0.wireOp",EDGE,"E6.2.0.1"),sQuery(id+"F0.wireOp",EDGE,"E6.2.0.2"),sQuery(id+"F0.wireOp",EDGE,"E6.2.0.3"),sQuery(id+"F0.wireOp",EDGE,"E6.3.0.0"),sQuery(id+"F0.wireOp",EDGE,"E6.3.0.1"),sQuery(id+"F0.wireOp",EDGE,"E6.3.0.2"),sQuery(id+"F0.wireOp",EDGE,"E6.3.0.3"),sQuery(id+"F0.wireOp",EDGE,"E6.4.0.0"),sQuery(id+"F0.wireOp",EDGE,"E6.4.0.1"),sQuery(id+"F0.wireOp",EDGE,"E6.4.0.2"),sQuery(id+"F0.wireOp",EDGE,"E6.4.0.3"),subQ9,subQ8,subQ1,subQ3,sQuery(id+"F0.wireOp",EDGE,"E6.6.0.0"),sQuery(id+"F0.wireOp",EDGE,"E6.6.0.1"),sQuery(id+"F0.wireOp",EDGE,"E6.6.0.2"),sQuery(id+"F0.wireOp",EDGE,"E6.6.0.3"),subQ7,subQ0,subQ4,subQ5,subQ10,subQ11,sQuery(id+"F0.wireOp",EDGE,"E13"),sQuery(id+"F0.wireOp",EDGE,"E14"),sQuery(id+"F0.wireOp",EDGE,"E15.trimOffspring"),sQuery(id+"F0.wireOp",EDGE,"E16.trimOffspring"),sQuery(id+"F0.wireOp",EDGE,"E17.trimOffspring"),sQuery(id+"F0.wireOp",EDGE,"E18.trimOffspring"),sQuery(id+"F0.wireOp",EDGE,"E19.trimOffspring"),subQ12,sQuery(id+"F0.wireOp",EDGE,"E21.trimOffspring"),sQuery(id+"F0.wireOp",EDGE,"E22")])],"isStart":false})})],"blendedInto":[makeQuery(id+"F4.boolean.opBoolean","SPLIT",FACE,{"disambiguationData":[TD([makeQuery(id+"F1.opExtrude","SWEPT_FACE",FACE,{"disambiguationData":[OSD([subQ9])]})])],"derivedFrom":makeQuery(id+"F1.opExtrude","CAP_FACE",FACE,{"disambiguationData":[OSD([subQ2,subQ6,sQuery(id+"F0.wireOp",EDGE,"E2"),sQuery(id+"F0.wireOp",EDGE,"E3"),sQuery(id+"F0.wireOp",EDGE,"E4"),sQuery(id+"F0.wireOp",EDGE,"E5"),sQuery(id+"F0.wireOp",EDGE,"E6.1.0.0"),sQuery(id+"F0.wireOp",EDGE,"E6.1.0.1"),sQuery(id+"F0.wireOp",EDGE,"E6.1.0.2"),sQuery(id+"F0.wireOp",EDGE,"E6.1.0.3"),sQuery(id+"F0.wireOp",EDGE,"E6.2.0.0"),sQuery(id+"F0.wireOp",EDGE,"E6.2.0.1"),sQuery(id+"F0.wireOp",EDGE,"E6.2.0.2"),sQuery(id+"F0.wireOp",EDGE,"E6.2.0.3"),sQuery(id+"F0.wireOp",EDGE,"E6.3.0.0"),sQuery(id+"F0.wireOp",EDGE,"E6.3.0.1"),sQuery(id+"F0.wireOp",EDGE,"E6.3.0.2"),sQuery(id+"F0.wireOp",EDGE,"E6.3.0.3"),sQuery(id+"F0.wireOp",EDGE,"E6.4.0.0"),sQuery(id+"F0.wireOp",EDGE,"E6.4.0.1"),sQuery(id+"F0.wireOp",EDGE,"E6.4.0.2"),sQuery(id+"F0.wireOp",EDGE,"E6.4.0.3"),subQ9,subQ8,subQ1,subQ3,sQuery(id+"F0.wireOp",EDGE,"E6.6.0.0"),sQuery(id+"F0.wireOp",EDGE,"E6.6.0.1"),sQuery(id+"F0.wireOp",EDGE,"E6.6.0.2"),sQuery(id+"F0.wireOp",EDGE,"E6.6.0.3"),subQ7,subQ0,subQ4,subQ5,subQ10,subQ11,sQuery(id+"F0.wireOp",EDGE,"E13"),sQuery(id+"F0.wireOp",EDGE,"E14"),sQuery(id+"F0.wireOp",EDGE,"E15.trimOffspring"),sQuery(id+"F0.wireOp",EDGE,"E16.trimOffspring"),sQuery(id+"F0.wireOp",EDGE,"E17.trimOffspring"),sQuery(id+"F0.wireOp",EDGE,"E18.trimOffspring"),sQuery(id+"F0.wireOp",EDGE,"E19.trimOffspring"),subQ12,sQuery(id+"F0.wireOp",EDGE,"E21.trimOffspring"),sQuery(id+"F0.wireOp",EDGE,"E22")])],"isStart":false})})]});}
            var Q38;
            Q38=makeQuery(id+"F1.opExtrude","CAP_EDGE",EDGE,{"disambiguationData":[OSD([sQuery(id+"F0.wireOp",EDGE,"E6.5.0.2")])],"isStart":false});
            var Q39;
            {var subQ0=sQuery(id+"F0.wireOp",EDGE,"E8.trimOffspring");var subQ1=sQuery(id+"F0.wireOp",EDGE,"E6.5.0.2");var subQ2=sQuery(id+"F0.wireOp",EDGE,"E0.0");var subQ3=sQuery(id+"F0.wireOp",EDGE,"E6.5.0.3");var subQ4=sQuery(id+"F0.wireOp",EDGE,"E9.trimOffspring");var subQ5=sQuery(id+"F0.wireOp",EDGE,"E10.trimOffspring");var subQ6=sQuery(id+"F0.wireOp",EDGE,"E1");var subQ7=sQuery(id+"F0.wireOp",EDGE,"E7.trimOffspring");var subQ8=sQuery(id+"F0.wireOp",EDGE,"E6.5.0.1");var subQ9=sQuery(id+"F0.wireOp",EDGE,"E6.5.0.0");var subQ10=sQuery(id+"F0.wireOp",EDGE,"E11.trimOffspring");var subQ11=sQuery(id+"F0.wireOp",EDGE,"E12.trimOffspring");var subQ12=sQuery(id+"F0.wireOp",EDGE,"E20.trimOffspring");Q39=makeQuery(id+"F5.opFillet","BLEND_EDGE",EDGE,{"blendedFrom":[makeQuery(id+"F1.opExtrude","SWEPT_EDGE",EDGE,{"disambiguationData":[OSD([subQ1,subQ3])]}),makeQuery(id+"F4.boolean.opBoolean","SPLIT",FACE,{"disambiguationData":[TD([makeQuery(id+"F1.opExtrude","SWEPT_FACE",FACE,{"disambiguationData":[OSD([subQ9])]})])],"derivedFrom":makeQuery(id+"F1.opExtrude","CAP_FACE",FACE,{"disambiguationData":[OSD([subQ2,subQ6,sQuery(id+"F0.wireOp",EDGE,"E2"),sQuery(id+"F0.wireOp",EDGE,"E3"),sQuery(id+"F0.wireOp",EDGE,"E4"),sQuery(id+"F0.wireOp",EDGE,"E5"),sQuery(id+"F0.wireOp",EDGE,"E6.1.0.0"),sQuery(id+"F0.wireOp",EDGE,"E6.1.0.1"),sQuery(id+"F0.wireOp",EDGE,"E6.1.0.2"),sQuery(id+"F0.wireOp",EDGE,"E6.1.0.3"),sQuery(id+"F0.wireOp",EDGE,"E6.2.0.0"),sQuery(id+"F0.wireOp",EDGE,"E6.2.0.1"),sQuery(id+"F0.wireOp",EDGE,"E6.2.0.2"),sQuery(id+"F0.wireOp",EDGE,"E6.2.0.3"),sQuery(id+"F0.wireOp",EDGE,"E6.3.0.0"),sQuery(id+"F0.wireOp",EDGE,"E6.3.0.1"),sQuery(id+"F0.wireOp",EDGE,"E6.3.0.2"),sQuery(id+"F0.wireOp",EDGE,"E6.3.0.3"),sQuery(id+"F0.wireOp",EDGE,"E6.4.0.0"),sQuery(id+"F0.wireOp",EDGE,"E6.4.0.1"),sQuery(id+"F0.wireOp",EDGE,"E6.4.0.2"),sQuery(id+"F0.wireOp",EDGE,"E6.4.0.3"),subQ9,subQ8,subQ1,subQ3,sQuery(id+"F0.wireOp",EDGE,"E6.6.0.0"),sQuery(id+"F0.wireOp",EDGE,"E6.6.0.1"),sQuery(id+"F0.wireOp",EDGE,"E6.6.0.2"),sQuery(id+"F0.wireOp",EDGE,"E6.6.0.3"),subQ7,subQ0,subQ4,subQ5,subQ10,subQ11,sQuery(id+"F0.wireOp",EDGE,"E13"),sQuery(id+"F0.wireOp",EDGE,"E14"),sQuery(id+"F0.wireOp",EDGE,"E15.trimOffspring"),sQuery(id+"F0.wireOp",EDGE,"E16.trimOffspring"),sQuery(id+"F0.wireOp",EDGE,"E17.trimOffspring"),sQuery(id+"F0.wireOp",EDGE,"E18.trimOffspring"),sQuery(id+"F0.wireOp",EDGE,"E19.trimOffspring"),subQ12,sQuery(id+"F0.wireOp",EDGE,"E21.trimOffspring"),sQuery(id+"F0.wireOp",EDGE,"E22")])],"isStart":false})})],"blendedInto":[makeQuery(id+"F4.boolean.opBoolean","SPLIT",FACE,{"disambiguationData":[TD([makeQuery(id+"F1.opExtrude","SWEPT_FACE",FACE,{"disambiguationData":[OSD([subQ9])]})])],"derivedFrom":makeQuery(id+"F1.opExtrude","CAP_FACE",FACE,{"disambiguationData":[OSD([subQ2,subQ6,sQuery(id+"F0.wireOp",EDGE,"E2"),sQuery(id+"F0.wireOp",EDGE,"E3"),sQuery(id+"F0.wireOp",EDGE,"E4"),sQuery(id+"F0.wireOp",EDGE,"E5"),sQuery(id+"F0.wireOp",EDGE,"E6.1.0.0"),sQuery(id+"F0.wireOp",EDGE,"E6.1.0.1"),sQuery(id+"F0.wireOp",EDGE,"E6.1.0.2"),sQuery(id+"F0.wireOp",EDGE,"E6.1.0.3"),sQuery(id+"F0.wireOp",EDGE,"E6.2.0.0"),sQuery(id+"F0.wireOp",EDGE,"E6.2.0.1"),sQuery(id+"F0.wireOp",EDGE,"E6.2.0.2"),sQuery(id+"F0.wireOp",EDGE,"E6.2.0.3"),sQuery(id+"F0.wireOp",EDGE,"E6.3.0.0"),sQuery(id+"F0.wireOp",EDGE,"E6.3.0.1"),sQuery(id+"F0.wireOp",EDGE,"E6.3.0.2"),sQuery(id+"F0.wireOp",EDGE,"E6.3.0.3"),sQuery(id+"F0.wireOp",EDGE,"E6.4.0.0"),sQuery(id+"F0.wireOp",EDGE,"E6.4.0.1"),sQuery(id+"F0.wireOp",EDGE,"E6.4.0.2"),sQuery(id+"F0.wireOp",EDGE,"E6.4.0.3"),subQ9,subQ8,subQ1,subQ3,sQuery(id+"F0.wireOp",EDGE,"E6.6.0.0"),sQuery(id+"F0.wireOp",EDGE,"E6.6.0.1"),sQuery(id+"F0.wireOp",EDGE,"E6.6.0.2"),sQuery(id+"F0.wireOp",EDGE,"E6.6.0.3"),subQ7,subQ0,subQ4,subQ5,subQ10,subQ11,sQuery(id+"F0.wireOp",EDGE,"E13"),sQuery(id+"F0.wireOp",EDGE,"E14"),sQuery(id+"F0.wireOp",EDGE,"E15.trimOffspring"),sQuery(id+"F0.wireOp",EDGE,"E16.trimOffspring"),sQuery(id+"F0.wireOp",EDGE,"E17.trimOffspring"),sQuery(id+"F0.wireOp",EDGE,"E18.trimOffspring"),sQuery(id+"F0.wireOp",EDGE,"E19.trimOffspring"),subQ12,sQuery(id+"F0.wireOp",EDGE,"E21.trimOffspring"),sQuery(id+"F0.wireOp",EDGE,"E22")])],"isStart":false})})]});}
            var Q40;
            {var subQ0=sQuery(id+"F0.wireOp",EDGE,"E8.trimOffspring");var subQ1=sQuery(id+"F0.wireOp",EDGE,"E6.5.0.2");var subQ2=sQuery(id+"F0.wireOp",EDGE,"E0.0");var subQ3=sQuery(id+"F0.wireOp",EDGE,"E6.5.0.3");var subQ4=sQuery(id+"F0.wireOp",EDGE,"E9.trimOffspring");var subQ5=sQuery(id+"F0.wireOp",EDGE,"E10.trimOffspring");var subQ6=sQuery(id+"F0.wireOp",EDGE,"E1");var subQ7=sQuery(id+"F0.wireOp",EDGE,"E7.trimOffspring");var subQ8=sQuery(id+"F0.wireOp",EDGE,"E6.5.0.1");var subQ9=sQuery(id+"F0.wireOp",EDGE,"E6.5.0.0");var subQ10=sQuery(id+"F0.wireOp",EDGE,"E11.trimOffspring");var subQ11=sQuery(id+"F0.wireOp",EDGE,"E12.trimOffspring");var subQ12=sQuery(id+"F0.wireOp",EDGE,"E20.trimOffspring");Q40=makeQuery(id+"F5.opFillet","BLEND_EDGE",EDGE,{"blendedFrom":[makeQuery(id+"F1.opExtrude","SWEPT_EDGE",EDGE,{"disambiguationData":[OSD([subQ3,subQ12])]}),makeQuery(id+"F4.boolean.opBoolean","SPLIT",FACE,{"disambiguationData":[TD([makeQuery(id+"F1.opExtrude","SWEPT_FACE",FACE,{"disambiguationData":[OSD([subQ9])]})])],"derivedFrom":makeQuery(id+"F1.opExtrude","CAP_FACE",FACE,{"disambiguationData":[OSD([subQ2,subQ6,sQuery(id+"F0.wireOp",EDGE,"E2"),sQuery(id+"F0.wireOp",EDGE,"E3"),sQuery(id+"F0.wireOp",EDGE,"E4"),sQuery(id+"F0.wireOp",EDGE,"E5"),sQuery(id+"F0.wireOp",EDGE,"E6.1.0.0"),sQuery(id+"F0.wireOp",EDGE,"E6.1.0.1"),sQuery(id+"F0.wireOp",EDGE,"E6.1.0.2"),sQuery(id+"F0.wireOp",EDGE,"E6.1.0.3"),sQuery(id+"F0.wireOp",EDGE,"E6.2.0.0"),sQuery(id+"F0.wireOp",EDGE,"E6.2.0.1"),sQuery(id+"F0.wireOp",EDGE,"E6.2.0.2"),sQuery(id+"F0.wireOp",EDGE,"E6.2.0.3"),sQuery(id+"F0.wireOp",EDGE,"E6.3.0.0"),sQuery(id+"F0.wireOp",EDGE,"E6.3.0.1"),sQuery(id+"F0.wireOp",EDGE,"E6.3.0.2"),sQuery(id+"F0.wireOp",EDGE,"E6.3.0.3"),sQuery(id+"F0.wireOp",EDGE,"E6.4.0.0"),sQuery(id+"F0.wireOp",EDGE,"E6.4.0.1"),sQuery(id+"F0.wireOp",EDGE,"E6.4.0.2"),sQuery(id+"F0.wireOp",EDGE,"E6.4.0.3"),subQ9,subQ8,subQ1,subQ3,sQuery(id+"F0.wireOp",EDGE,"E6.6.0.0"),sQuery(id+"F0.wireOp",EDGE,"E6.6.0.1"),sQuery(id+"F0.wireOp",EDGE,"E6.6.0.2"),sQuery(id+"F0.wireOp",EDGE,"E6.6.0.3"),subQ7,subQ0,subQ4,subQ5,subQ10,subQ11,sQuery(id+"F0.wireOp",EDGE,"E13"),sQuery(id+"F0.wireOp",EDGE,"E14"),sQuery(id+"F0.wireOp",EDGE,"E15.trimOffspring"),sQuery(id+"F0.wireOp",EDGE,"E16.trimOffspring"),sQuery(id+"F0.wireOp",EDGE,"E17.trimOffspring"),sQuery(id+"F0.wireOp",EDGE,"E18.trimOffspring"),sQuery(id+"F0.wireOp",EDGE,"E19.trimOffspring"),subQ12,sQuery(id+"F0.wireOp",EDGE,"E21.trimOffspring"),sQuery(id+"F0.wireOp",EDGE,"E22")])],"isStart":false})})],"blendedInto":[makeQuery(id+"F4.boolean.opBoolean","SPLIT",FACE,{"disambiguationData":[TD([makeQuery(id+"F1.opExtrude","SWEPT_FACE",FACE,{"disambiguationData":[OSD([subQ9])]})])],"derivedFrom":makeQuery(id+"F1.opExtrude","CAP_FACE",FACE,{"disambiguationData":[OSD([subQ2,subQ6,sQuery(id+"F0.wireOp",EDGE,"E2"),sQuery(id+"F0.wireOp",EDGE,"E3"),sQuery(id+"F0.wireOp",EDGE,"E4"),sQuery(id+"F0.wireOp",EDGE,"E5"),sQuery(id+"F0.wireOp",EDGE,"E6.1.0.0"),sQuery(id+"F0.wireOp",EDGE,"E6.1.0.1"),sQuery(id+"F0.wireOp",EDGE,"E6.1.0.2"),sQuery(id+"F0.wireOp",EDGE,"E6.1.0.3"),sQuery(id+"F0.wireOp",EDGE,"E6.2.0.0"),sQuery(id+"F0.wireOp",EDGE,"E6.2.0.1"),sQuery(id+"F0.wireOp",EDGE,"E6.2.0.2"),sQuery(id+"F0.wireOp",EDGE,"E6.2.0.3"),sQuery(id+"F0.wireOp",EDGE,"E6.3.0.0"),sQuery(id+"F0.wireOp",EDGE,"E6.3.0.1"),sQuery(id+"F0.wireOp",EDGE,"E6.3.0.2"),sQuery(id+"F0.wireOp",EDGE,"E6.3.0.3"),sQuery(id+"F0.wireOp",EDGE,"E6.4.0.0"),sQuery(id+"F0.wireOp",EDGE,"E6.4.0.1"),sQuery(id+"F0.wireOp",EDGE,"E6.4.0.2"),sQuery(id+"F0.wireOp",EDGE,"E6.4.0.3"),subQ9,subQ8,subQ1,subQ3,sQuery(id+"F0.wireOp",EDGE,"E6.6.0.0"),sQuery(id+"F0.wireOp",EDGE,"E6.6.0.1"),sQuery(id+"F0.wireOp",EDGE,"E6.6.0.2"),sQuery(id+"F0.wireOp",EDGE,"E6.6.0.3"),subQ7,subQ0,subQ4,subQ5,subQ10,subQ11,sQuery(id+"F0.wireOp",EDGE,"E13"),sQuery(id+"F0.wireOp",EDGE,"E14"),sQuery(id+"F0.wireOp",EDGE,"E15.trimOffspring"),sQuery(id+"F0.wireOp",EDGE,"E16.trimOffspring"),sQuery(id+"F0.wireOp",EDGE,"E17.trimOffspring"),sQuery(id+"F0.wireOp",EDGE,"E18.trimOffspring"),sQuery(id+"F0.wireOp",EDGE,"E19.trimOffspring"),subQ12,sQuery(id+"F0.wireOp",EDGE,"E21.trimOffspring"),sQuery(id+"F0.wireOp",EDGE,"E22")])],"isStart":false})})]});}
            var Q41;
            Q41=makeQuery(id+"F1.opExtrude","CAP_EDGE",EDGE,{"disambiguationData":[OSD([sQuery(id+"F0.wireOp",EDGE,"E20.trimOffspring")])],"isStart":false});
            var Q42;
            Q42=makeQuery(id+"F1.opExtrude","CAP_EDGE",EDGE,{"disambiguationData":[OSD([sQuery(id+"F0.wireOp",EDGE,"E6.6.0.1")])],"isStart":false});
            var Q43;
            {var subQ0=sQuery(id+"F0.wireOp",EDGE,"E10.trimOffspring");var subQ1=sQuery(id+"F0.wireOp",EDGE,"E9.trimOffspring");var subQ2=sQuery(id+"F0.wireOp",EDGE,"E6.6.0.0");var subQ3=sQuery(id+"F0.wireOp",EDGE,"E8.trimOffspring");var subQ4=sQuery(id+"F0.wireOp",EDGE,"E0.0");var subQ5=sQuery(id+"F0.wireOp",EDGE,"E7.trimOffspring");var subQ6=sQuery(id+"F0.wireOp",EDGE,"E6.6.0.2");var subQ7=sQuery(id+"F0.wireOp",EDGE,"E12.trimOffspring");var subQ8=sQuery(id+"F0.wireOp",EDGE,"E6.6.0.3");var subQ9=sQuery(id+"F0.wireOp",EDGE,"E6.6.0.1");var subQ10=sQuery(id+"F0.wireOp",EDGE,"E11.trimOffspring");var subQ11=sQuery(id+"F0.wireOp",EDGE,"E1");var subQ12=sQuery(id+"F0.wireOp",EDGE,"E21.trimOffspring");Q43=makeQuery(id+"F5.opFillet","BLEND_EDGE",EDGE,{"blendedFrom":[makeQuery(id+"F1.opExtrude","SWEPT_EDGE",EDGE,{"disambiguationData":[OSD([subQ2,subQ9])]}),makeQuery(id+"F4.boolean.opBoolean","SPLIT",FACE,{"disambiguationData":[TD([makeQuery(id+"F1.opExtrude","SWEPT_FACE",FACE,{"disambiguationData":[OSD([subQ2])]})])],"derivedFrom":makeQuery(id+"F1.opExtrude","CAP_FACE",FACE,{"disambiguationData":[OSD([subQ4,subQ11,sQuery(id+"F0.wireOp",EDGE,"E2"),sQuery(id+"F0.wireOp",EDGE,"E3"),sQuery(id+"F0.wireOp",EDGE,"E4"),sQuery(id+"F0.wireOp",EDGE,"E5"),sQuery(id+"F0.wireOp",EDGE,"E6.1.0.0"),sQuery(id+"F0.wireOp",EDGE,"E6.1.0.1"),sQuery(id+"F0.wireOp",EDGE,"E6.1.0.2"),sQuery(id+"F0.wireOp",EDGE,"E6.1.0.3"),sQuery(id+"F0.wireOp",EDGE,"E6.2.0.0"),sQuery(id+"F0.wireOp",EDGE,"E6.2.0.1"),sQuery(id+"F0.wireOp",EDGE,"E6.2.0.2"),sQuery(id+"F0.wireOp",EDGE,"E6.2.0.3"),sQuery(id+"F0.wireOp",EDGE,"E6.3.0.0"),sQuery(id+"F0.wireOp",EDGE,"E6.3.0.1"),sQuery(id+"F0.wireOp",EDGE,"E6.3.0.2"),sQuery(id+"F0.wireOp",EDGE,"E6.3.0.3"),sQuery(id+"F0.wireOp",EDGE,"E6.4.0.0"),sQuery(id+"F0.wireOp",EDGE,"E6.4.0.1"),sQuery(id+"F0.wireOp",EDGE,"E6.4.0.2"),sQuery(id+"F0.wireOp",EDGE,"E6.4.0.3"),sQuery(id+"F0.wireOp",EDGE,"E6.5.0.0"),sQuery(id+"F0.wireOp",EDGE,"E6.5.0.1"),sQuery(id+"F0.wireOp",EDGE,"E6.5.0.2"),sQuery(id+"F0.wireOp",EDGE,"E6.5.0.3"),subQ2,subQ9,subQ6,subQ8,subQ5,subQ3,subQ1,subQ0,subQ10,subQ7,sQuery(id+"F0.wireOp",EDGE,"E13"),sQuery(id+"F0.wireOp",EDGE,"E14"),sQuery(id+"F0.wireOp",EDGE,"E15.trimOffspring"),sQuery(id+"F0.wireOp",EDGE,"E16.trimOffspring"),sQuery(id+"F0.wireOp",EDGE,"E17.trimOffspring"),sQuery(id+"F0.wireOp",EDGE,"E18.trimOffspring"),sQuery(id+"F0.wireOp",EDGE,"E19.trimOffspring"),sQuery(id+"F0.wireOp",EDGE,"E20.trimOffspring"),subQ12,sQuery(id+"F0.wireOp",EDGE,"E22")])],"isStart":false})})],"blendedInto":[makeQuery(id+"F4.boolean.opBoolean","SPLIT",FACE,{"disambiguationData":[TD([makeQuery(id+"F1.opExtrude","SWEPT_FACE",FACE,{"disambiguationData":[OSD([subQ2])]})])],"derivedFrom":makeQuery(id+"F1.opExtrude","CAP_FACE",FACE,{"disambiguationData":[OSD([subQ4,subQ11,sQuery(id+"F0.wireOp",EDGE,"E2"),sQuery(id+"F0.wireOp",EDGE,"E3"),sQuery(id+"F0.wireOp",EDGE,"E4"),sQuery(id+"F0.wireOp",EDGE,"E5"),sQuery(id+"F0.wireOp",EDGE,"E6.1.0.0"),sQuery(id+"F0.wireOp",EDGE,"E6.1.0.1"),sQuery(id+"F0.wireOp",EDGE,"E6.1.0.2"),sQuery(id+"F0.wireOp",EDGE,"E6.1.0.3"),sQuery(id+"F0.wireOp",EDGE,"E6.2.0.0"),sQuery(id+"F0.wireOp",EDGE,"E6.2.0.1"),sQuery(id+"F0.wireOp",EDGE,"E6.2.0.2"),sQuery(id+"F0.wireOp",EDGE,"E6.2.0.3"),sQuery(id+"F0.wireOp",EDGE,"E6.3.0.0"),sQuery(id+"F0.wireOp",EDGE,"E6.3.0.1"),sQuery(id+"F0.wireOp",EDGE,"E6.3.0.2"),sQuery(id+"F0.wireOp",EDGE,"E6.3.0.3"),sQuery(id+"F0.wireOp",EDGE,"E6.4.0.0"),sQuery(id+"F0.wireOp",EDGE,"E6.4.0.1"),sQuery(id+"F0.wireOp",EDGE,"E6.4.0.2"),sQuery(id+"F0.wireOp",EDGE,"E6.4.0.3"),sQuery(id+"F0.wireOp",EDGE,"E6.5.0.0"),sQuery(id+"F0.wireOp",EDGE,"E6.5.0.1"),sQuery(id+"F0.wireOp",EDGE,"E6.5.0.2"),sQuery(id+"F0.wireOp",EDGE,"E6.5.0.3"),subQ2,subQ9,subQ6,subQ8,subQ5,subQ3,subQ1,subQ0,subQ10,subQ7,sQuery(id+"F0.wireOp",EDGE,"E13"),sQuery(id+"F0.wireOp",EDGE,"E14"),sQuery(id+"F0.wireOp",EDGE,"E15.trimOffspring"),sQuery(id+"F0.wireOp",EDGE,"E16.trimOffspring"),sQuery(id+"F0.wireOp",EDGE,"E17.trimOffspring"),sQuery(id+"F0.wireOp",EDGE,"E18.trimOffspring"),sQuery(id+"F0.wireOp",EDGE,"E19.trimOffspring"),sQuery(id+"F0.wireOp",EDGE,"E20.trimOffspring"),subQ12,sQuery(id+"F0.wireOp",EDGE,"E22")])],"isStart":false})})]});}
            var Q44;
            {var subQ0=sQuery(id+"F0.wireOp",EDGE,"E10.trimOffspring");var subQ1=sQuery(id+"F0.wireOp",EDGE,"E9.trimOffspring");var subQ2=sQuery(id+"F0.wireOp",EDGE,"E6.6.0.0");var subQ3=sQuery(id+"F0.wireOp",EDGE,"E8.trimOffspring");var subQ4=sQuery(id+"F0.wireOp",EDGE,"E0.0");var subQ5=sQuery(id+"F0.wireOp",EDGE,"E7.trimOffspring");var subQ6=sQuery(id+"F0.wireOp",EDGE,"E6.6.0.2");var subQ7=sQuery(id+"F0.wireOp",EDGE,"E12.trimOffspring");var subQ8=sQuery(id+"F0.wireOp",EDGE,"E6.6.0.3");var subQ9=sQuery(id+"F0.wireOp",EDGE,"E6.6.0.1");var subQ10=sQuery(id+"F0.wireOp",EDGE,"E11.trimOffspring");var subQ11=sQuery(id+"F0.wireOp",EDGE,"E1");var subQ12=sQuery(id+"F0.wireOp",EDGE,"E21.trimOffspring");Q44=makeQuery(id+"F5.opFillet","BLEND_EDGE",EDGE,{"blendedFrom":[makeQuery(id+"F1.opExtrude","SWEPT_EDGE",EDGE,{"disambiguationData":[OSD([subQ2,subQ6])]}),makeQuery(id+"F4.boolean.opBoolean","SPLIT",FACE,{"disambiguationData":[TD([makeQuery(id+"F1.opExtrude","SWEPT_FACE",FACE,{"disambiguationData":[OSD([subQ2])]})])],"derivedFrom":makeQuery(id+"F1.opExtrude","CAP_FACE",FACE,{"disambiguationData":[OSD([subQ4,subQ11,sQuery(id+"F0.wireOp",EDGE,"E2"),sQuery(id+"F0.wireOp",EDGE,"E3"),sQuery(id+"F0.wireOp",EDGE,"E4"),sQuery(id+"F0.wireOp",EDGE,"E5"),sQuery(id+"F0.wireOp",EDGE,"E6.1.0.0"),sQuery(id+"F0.wireOp",EDGE,"E6.1.0.1"),sQuery(id+"F0.wireOp",EDGE,"E6.1.0.2"),sQuery(id+"F0.wireOp",EDGE,"E6.1.0.3"),sQuery(id+"F0.wireOp",EDGE,"E6.2.0.0"),sQuery(id+"F0.wireOp",EDGE,"E6.2.0.1"),sQuery(id+"F0.wireOp",EDGE,"E6.2.0.2"),sQuery(id+"F0.wireOp",EDGE,"E6.2.0.3"),sQuery(id+"F0.wireOp",EDGE,"E6.3.0.0"),sQuery(id+"F0.wireOp",EDGE,"E6.3.0.1"),sQuery(id+"F0.wireOp",EDGE,"E6.3.0.2"),sQuery(id+"F0.wireOp",EDGE,"E6.3.0.3"),sQuery(id+"F0.wireOp",EDGE,"E6.4.0.0"),sQuery(id+"F0.wireOp",EDGE,"E6.4.0.1"),sQuery(id+"F0.wireOp",EDGE,"E6.4.0.2"),sQuery(id+"F0.wireOp",EDGE,"E6.4.0.3"),sQuery(id+"F0.wireOp",EDGE,"E6.5.0.0"),sQuery(id+"F0.wireOp",EDGE,"E6.5.0.1"),sQuery(id+"F0.wireOp",EDGE,"E6.5.0.2"),sQuery(id+"F0.wireOp",EDGE,"E6.5.0.3"),subQ2,subQ9,subQ6,subQ8,subQ5,subQ3,subQ1,subQ0,subQ10,subQ7,sQuery(id+"F0.wireOp",EDGE,"E13"),sQuery(id+"F0.wireOp",EDGE,"E14"),sQuery(id+"F0.wireOp",EDGE,"E15.trimOffspring"),sQuery(id+"F0.wireOp",EDGE,"E16.trimOffspring"),sQuery(id+"F0.wireOp",EDGE,"E17.trimOffspring"),sQuery(id+"F0.wireOp",EDGE,"E18.trimOffspring"),sQuery(id+"F0.wireOp",EDGE,"E19.trimOffspring"),sQuery(id+"F0.wireOp",EDGE,"E20.trimOffspring"),subQ12,sQuery(id+"F0.wireOp",EDGE,"E22")])],"isStart":false})})],"blendedInto":[makeQuery(id+"F4.boolean.opBoolean","SPLIT",FACE,{"disambiguationData":[TD([makeQuery(id+"F1.opExtrude","SWEPT_FACE",FACE,{"disambiguationData":[OSD([subQ2])]})])],"derivedFrom":makeQuery(id+"F1.opExtrude","CAP_FACE",FACE,{"disambiguationData":[OSD([subQ4,subQ11,sQuery(id+"F0.wireOp",EDGE,"E2"),sQuery(id+"F0.wireOp",EDGE,"E3"),sQuery(id+"F0.wireOp",EDGE,"E4"),sQuery(id+"F0.wireOp",EDGE,"E5"),sQuery(id+"F0.wireOp",EDGE,"E6.1.0.0"),sQuery(id+"F0.wireOp",EDGE,"E6.1.0.1"),sQuery(id+"F0.wireOp",EDGE,"E6.1.0.2"),sQuery(id+"F0.wireOp",EDGE,"E6.1.0.3"),sQuery(id+"F0.wireOp",EDGE,"E6.2.0.0"),sQuery(id+"F0.wireOp",EDGE,"E6.2.0.1"),sQuery(id+"F0.wireOp",EDGE,"E6.2.0.2"),sQuery(id+"F0.wireOp",EDGE,"E6.2.0.3"),sQuery(id+"F0.wireOp",EDGE,"E6.3.0.0"),sQuery(id+"F0.wireOp",EDGE,"E6.3.0.1"),sQuery(id+"F0.wireOp",EDGE,"E6.3.0.2"),sQuery(id+"F0.wireOp",EDGE,"E6.3.0.3"),sQuery(id+"F0.wireOp",EDGE,"E6.4.0.0"),sQuery(id+"F0.wireOp",EDGE,"E6.4.0.1"),sQuery(id+"F0.wireOp",EDGE,"E6.4.0.2"),sQuery(id+"F0.wireOp",EDGE,"E6.4.0.3"),sQuery(id+"F0.wireOp",EDGE,"E6.5.0.0"),sQuery(id+"F0.wireOp",EDGE,"E6.5.0.1"),sQuery(id+"F0.wireOp",EDGE,"E6.5.0.2"),sQuery(id+"F0.wireOp",EDGE,"E6.5.0.3"),subQ2,subQ9,subQ6,subQ8,subQ5,subQ3,subQ1,subQ0,subQ10,subQ7,sQuery(id+"F0.wireOp",EDGE,"E13"),sQuery(id+"F0.wireOp",EDGE,"E14"),sQuery(id+"F0.wireOp",EDGE,"E15.trimOffspring"),sQuery(id+"F0.wireOp",EDGE,"E16.trimOffspring"),sQuery(id+"F0.wireOp",EDGE,"E17.trimOffspring"),sQuery(id+"F0.wireOp",EDGE,"E18.trimOffspring"),sQuery(id+"F0.wireOp",EDGE,"E19.trimOffspring"),sQuery(id+"F0.wireOp",EDGE,"E20.trimOffspring"),subQ12,sQuery(id+"F0.wireOp",EDGE,"E22")])],"isStart":false})})]});}
            var Q45;
            Q45=makeQuery(id+"F1.opExtrude","CAP_EDGE",EDGE,{"disambiguationData":[OSD([sQuery(id+"F0.wireOp",EDGE,"E6.6.0.2")])],"isStart":false});
            var Q46;
            {var subQ0=sQuery(id+"F0.wireOp",EDGE,"E10.trimOffspring");var subQ1=sQuery(id+"F0.wireOp",EDGE,"E9.trimOffspring");var subQ2=sQuery(id+"F0.wireOp",EDGE,"E6.6.0.0");var subQ3=sQuery(id+"F0.wireOp",EDGE,"E8.trimOffspring");var subQ4=sQuery(id+"F0.wireOp",EDGE,"E0.0");var subQ5=sQuery(id+"F0.wireOp",EDGE,"E7.trimOffspring");var subQ6=sQuery(id+"F0.wireOp",EDGE,"E6.6.0.2");var subQ7=sQuery(id+"F0.wireOp",EDGE,"E12.trimOffspring");var subQ8=sQuery(id+"F0.wireOp",EDGE,"E6.6.0.3");var subQ9=sQuery(id+"F0.wireOp",EDGE,"E6.6.0.1");var subQ10=sQuery(id+"F0.wireOp",EDGE,"E11.trimOffspring");var subQ11=sQuery(id+"F0.wireOp",EDGE,"E1");var subQ12=sQuery(id+"F0.wireOp",EDGE,"E21.trimOffspring");Q46=makeQuery(id+"F5.opFillet","BLEND_EDGE",EDGE,{"blendedFrom":[makeQuery(id+"F1.opExtrude","SWEPT_EDGE",EDGE,{"disambiguationData":[OSD([subQ6,subQ8])]}),makeQuery(id+"F4.boolean.opBoolean","SPLIT",FACE,{"disambiguationData":[TD([makeQuery(id+"F1.opExtrude","SWEPT_FACE",FACE,{"disambiguationData":[OSD([subQ2])]})])],"derivedFrom":makeQuery(id+"F1.opExtrude","CAP_FACE",FACE,{"disambiguationData":[OSD([subQ4,subQ11,sQuery(id+"F0.wireOp",EDGE,"E2"),sQuery(id+"F0.wireOp",EDGE,"E3"),sQuery(id+"F0.wireOp",EDGE,"E4"),sQuery(id+"F0.wireOp",EDGE,"E5"),sQuery(id+"F0.wireOp",EDGE,"E6.1.0.0"),sQuery(id+"F0.wireOp",EDGE,"E6.1.0.1"),sQuery(id+"F0.wireOp",EDGE,"E6.1.0.2"),sQuery(id+"F0.wireOp",EDGE,"E6.1.0.3"),sQuery(id+"F0.wireOp",EDGE,"E6.2.0.0"),sQuery(id+"F0.wireOp",EDGE,"E6.2.0.1"),sQuery(id+"F0.wireOp",EDGE,"E6.2.0.2"),sQuery(id+"F0.wireOp",EDGE,"E6.2.0.3"),sQuery(id+"F0.wireOp",EDGE,"E6.3.0.0"),sQuery(id+"F0.wireOp",EDGE,"E6.3.0.1"),sQuery(id+"F0.wireOp",EDGE,"E6.3.0.2"),sQuery(id+"F0.wireOp",EDGE,"E6.3.0.3"),sQuery(id+"F0.wireOp",EDGE,"E6.4.0.0"),sQuery(id+"F0.wireOp",EDGE,"E6.4.0.1"),sQuery(id+"F0.wireOp",EDGE,"E6.4.0.2"),sQuery(id+"F0.wireOp",EDGE,"E6.4.0.3"),sQuery(id+"F0.wireOp",EDGE,"E6.5.0.0"),sQuery(id+"F0.wireOp",EDGE,"E6.5.0.1"),sQuery(id+"F0.wireOp",EDGE,"E6.5.0.2"),sQuery(id+"F0.wireOp",EDGE,"E6.5.0.3"),subQ2,subQ9,subQ6,subQ8,subQ5,subQ3,subQ1,subQ0,subQ10,subQ7,sQuery(id+"F0.wireOp",EDGE,"E13"),sQuery(id+"F0.wireOp",EDGE,"E14"),sQuery(id+"F0.wireOp",EDGE,"E15.trimOffspring"),sQuery(id+"F0.wireOp",EDGE,"E16.trimOffspring"),sQuery(id+"F0.wireOp",EDGE,"E17.trimOffspring"),sQuery(id+"F0.wireOp",EDGE,"E18.trimOffspring"),sQuery(id+"F0.wireOp",EDGE,"E19.trimOffspring"),sQuery(id+"F0.wireOp",EDGE,"E20.trimOffspring"),subQ12,sQuery(id+"F0.wireOp",EDGE,"E22")])],"isStart":false})})],"blendedInto":[makeQuery(id+"F4.boolean.opBoolean","SPLIT",FACE,{"disambiguationData":[TD([makeQuery(id+"F1.opExtrude","SWEPT_FACE",FACE,{"disambiguationData":[OSD([subQ2])]})])],"derivedFrom":makeQuery(id+"F1.opExtrude","CAP_FACE",FACE,{"disambiguationData":[OSD([subQ4,subQ11,sQuery(id+"F0.wireOp",EDGE,"E2"),sQuery(id+"F0.wireOp",EDGE,"E3"),sQuery(id+"F0.wireOp",EDGE,"E4"),sQuery(id+"F0.wireOp",EDGE,"E5"),sQuery(id+"F0.wireOp",EDGE,"E6.1.0.0"),sQuery(id+"F0.wireOp",EDGE,"E6.1.0.1"),sQuery(id+"F0.wireOp",EDGE,"E6.1.0.2"),sQuery(id+"F0.wireOp",EDGE,"E6.1.0.3"),sQuery(id+"F0.wireOp",EDGE,"E6.2.0.0"),sQuery(id+"F0.wireOp",EDGE,"E6.2.0.1"),sQuery(id+"F0.wireOp",EDGE,"E6.2.0.2"),sQuery(id+"F0.wireOp",EDGE,"E6.2.0.3"),sQuery(id+"F0.wireOp",EDGE,"E6.3.0.0"),sQuery(id+"F0.wireOp",EDGE,"E6.3.0.1"),sQuery(id+"F0.wireOp",EDGE,"E6.3.0.2"),sQuery(id+"F0.wireOp",EDGE,"E6.3.0.3"),sQuery(id+"F0.wireOp",EDGE,"E6.4.0.0"),sQuery(id+"F0.wireOp",EDGE,"E6.4.0.1"),sQuery(id+"F0.wireOp",EDGE,"E6.4.0.2"),sQuery(id+"F0.wireOp",EDGE,"E6.4.0.3"),sQuery(id+"F0.wireOp",EDGE,"E6.5.0.0"),sQuery(id+"F0.wireOp",EDGE,"E6.5.0.1"),sQuery(id+"F0.wireOp",EDGE,"E6.5.0.2"),sQuery(id+"F0.wireOp",EDGE,"E6.5.0.3"),subQ2,subQ9,subQ6,subQ8,subQ5,subQ3,subQ1,subQ0,subQ10,subQ7,sQuery(id+"F0.wireOp",EDGE,"E13"),sQuery(id+"F0.wireOp",EDGE,"E14"),sQuery(id+"F0.wireOp",EDGE,"E15.trimOffspring"),sQuery(id+"F0.wireOp",EDGE,"E16.trimOffspring"),sQuery(id+"F0.wireOp",EDGE,"E17.trimOffspring"),sQuery(id+"F0.wireOp",EDGE,"E18.trimOffspring"),sQuery(id+"F0.wireOp",EDGE,"E19.trimOffspring"),sQuery(id+"F0.wireOp",EDGE,"E20.trimOffspring"),subQ12,sQuery(id+"F0.wireOp",EDGE,"E22")])],"isStart":false})})]});}
            var Q47;
            {var subQ0=sQuery(id+"F0.wireOp",EDGE,"E10.trimOffspring");var subQ1=sQuery(id+"F0.wireOp",EDGE,"E9.trimOffspring");var subQ2=sQuery(id+"F0.wireOp",EDGE,"E6.6.0.0");var subQ3=sQuery(id+"F0.wireOp",EDGE,"E8.trimOffspring");var subQ4=sQuery(id+"F0.wireOp",EDGE,"E0.0");var subQ5=sQuery(id+"F0.wireOp",EDGE,"E7.trimOffspring");var subQ6=sQuery(id+"F0.wireOp",EDGE,"E6.6.0.2");var subQ7=sQuery(id+"F0.wireOp",EDGE,"E12.trimOffspring");var subQ8=sQuery(id+"F0.wireOp",EDGE,"E6.6.0.3");var subQ9=sQuery(id+"F0.wireOp",EDGE,"E6.6.0.1");var subQ10=sQuery(id+"F0.wireOp",EDGE,"E11.trimOffspring");var subQ11=sQuery(id+"F0.wireOp",EDGE,"E1");var subQ12=sQuery(id+"F0.wireOp",EDGE,"E21.trimOffspring");Q47=makeQuery(id+"F5.opFillet","BLEND_EDGE",EDGE,{"blendedFrom":[makeQuery(id+"F1.opExtrude","SWEPT_EDGE",EDGE,{"disambiguationData":[OSD([subQ8,subQ12])]}),makeQuery(id+"F4.boolean.opBoolean","SPLIT",FACE,{"disambiguationData":[TD([makeQuery(id+"F1.opExtrude","SWEPT_FACE",FACE,{"disambiguationData":[OSD([subQ2])]})])],"derivedFrom":makeQuery(id+"F1.opExtrude","CAP_FACE",FACE,{"disambiguationData":[OSD([subQ4,subQ11,sQuery(id+"F0.wireOp",EDGE,"E2"),sQuery(id+"F0.wireOp",EDGE,"E3"),sQuery(id+"F0.wireOp",EDGE,"E4"),sQuery(id+"F0.wireOp",EDGE,"E5"),sQuery(id+"F0.wireOp",EDGE,"E6.1.0.0"),sQuery(id+"F0.wireOp",EDGE,"E6.1.0.1"),sQuery(id+"F0.wireOp",EDGE,"E6.1.0.2"),sQuery(id+"F0.wireOp",EDGE,"E6.1.0.3"),sQuery(id+"F0.wireOp",EDGE,"E6.2.0.0"),sQuery(id+"F0.wireOp",EDGE,"E6.2.0.1"),sQuery(id+"F0.wireOp",EDGE,"E6.2.0.2"),sQuery(id+"F0.wireOp",EDGE,"E6.2.0.3"),sQuery(id+"F0.wireOp",EDGE,"E6.3.0.0"),sQuery(id+"F0.wireOp",EDGE,"E6.3.0.1"),sQuery(id+"F0.wireOp",EDGE,"E6.3.0.2"),sQuery(id+"F0.wireOp",EDGE,"E6.3.0.3"),sQuery(id+"F0.wireOp",EDGE,"E6.4.0.0"),sQuery(id+"F0.wireOp",EDGE,"E6.4.0.1"),sQuery(id+"F0.wireOp",EDGE,"E6.4.0.2"),sQuery(id+"F0.wireOp",EDGE,"E6.4.0.3"),sQuery(id+"F0.wireOp",EDGE,"E6.5.0.0"),sQuery(id+"F0.wireOp",EDGE,"E6.5.0.1"),sQuery(id+"F0.wireOp",EDGE,"E6.5.0.2"),sQuery(id+"F0.wireOp",EDGE,"E6.5.0.3"),subQ2,subQ9,subQ6,subQ8,subQ5,subQ3,subQ1,subQ0,subQ10,subQ7,sQuery(id+"F0.wireOp",EDGE,"E13"),sQuery(id+"F0.wireOp",EDGE,"E14"),sQuery(id+"F0.wireOp",EDGE,"E15.trimOffspring"),sQuery(id+"F0.wireOp",EDGE,"E16.trimOffspring"),sQuery(id+"F0.wireOp",EDGE,"E17.trimOffspring"),sQuery(id+"F0.wireOp",EDGE,"E18.trimOffspring"),sQuery(id+"F0.wireOp",EDGE,"E19.trimOffspring"),sQuery(id+"F0.wireOp",EDGE,"E20.trimOffspring"),subQ12,sQuery(id+"F0.wireOp",EDGE,"E22")])],"isStart":false})})],"blendedInto":[makeQuery(id+"F4.boolean.opBoolean","SPLIT",FACE,{"disambiguationData":[TD([makeQuery(id+"F1.opExtrude","SWEPT_FACE",FACE,{"disambiguationData":[OSD([subQ2])]})])],"derivedFrom":makeQuery(id+"F1.opExtrude","CAP_FACE",FACE,{"disambiguationData":[OSD([subQ4,subQ11,sQuery(id+"F0.wireOp",EDGE,"E2"),sQuery(id+"F0.wireOp",EDGE,"E3"),sQuery(id+"F0.wireOp",EDGE,"E4"),sQuery(id+"F0.wireOp",EDGE,"E5"),sQuery(id+"F0.wireOp",EDGE,"E6.1.0.0"),sQuery(id+"F0.wireOp",EDGE,"E6.1.0.1"),sQuery(id+"F0.wireOp",EDGE,"E6.1.0.2"),sQuery(id+"F0.wireOp",EDGE,"E6.1.0.3"),sQuery(id+"F0.wireOp",EDGE,"E6.2.0.0"),sQuery(id+"F0.wireOp",EDGE,"E6.2.0.1"),sQuery(id+"F0.wireOp",EDGE,"E6.2.0.2"),sQuery(id+"F0.wireOp",EDGE,"E6.2.0.3"),sQuery(id+"F0.wireOp",EDGE,"E6.3.0.0"),sQuery(id+"F0.wireOp",EDGE,"E6.3.0.1"),sQuery(id+"F0.wireOp",EDGE,"E6.3.0.2"),sQuery(id+"F0.wireOp",EDGE,"E6.3.0.3"),sQuery(id+"F0.wireOp",EDGE,"E6.4.0.0"),sQuery(id+"F0.wireOp",EDGE,"E6.4.0.1"),sQuery(id+"F0.wireOp",EDGE,"E6.4.0.2"),sQuery(id+"F0.wireOp",EDGE,"E6.4.0.3"),sQuery(id+"F0.wireOp",EDGE,"E6.5.0.0"),sQuery(id+"F0.wireOp",EDGE,"E6.5.0.1"),sQuery(id+"F0.wireOp",EDGE,"E6.5.0.2"),sQuery(id+"F0.wireOp",EDGE,"E6.5.0.3"),subQ2,subQ9,subQ6,subQ8,subQ5,subQ3,subQ1,subQ0,subQ10,subQ7,sQuery(id+"F0.wireOp",EDGE,"E13"),sQuery(id+"F0.wireOp",EDGE,"E14"),sQuery(id+"F0.wireOp",EDGE,"E15.trimOffspring"),sQuery(id+"F0.wireOp",EDGE,"E16.trimOffspring"),sQuery(id+"F0.wireOp",EDGE,"E17.trimOffspring"),sQuery(id+"F0.wireOp",EDGE,"E18.trimOffspring"),sQuery(id+"F0.wireOp",EDGE,"E19.trimOffspring"),sQuery(id+"F0.wireOp",EDGE,"E20.trimOffspring"),subQ12,sQuery(id+"F0.wireOp",EDGE,"E22")])],"isStart":false})})]});}
            var Q48;
            Q48=makeQuery(id+"F1.opExtrude","CAP_EDGE",EDGE,{"disambiguationData":[OSD([sQuery(id+"F0.wireOp",EDGE,"E21.trimOffspring")])],"isStart":false});
            fillet(context, id + "F10", {"entities" : qUnion([Q0, Q1, Q2, Q3, Q4, Q5, Q6, Q7, Q8, Q9, Q10, Q11, Q12, Q13, Q14, Q15, Q16, Q17, Q18, Q19, Q20, Q21, Q22, Q23, Q24, Q25, Q26, Q27, Q28, Q29, Q30, Q31, Q32, Q33, Q34, Q35, Q36, Q37, Q38, Q39, Q40, Q41, Q42, Q43, Q44, Q45, Q46, Q47, Q48]), "radius" : 1 * mm, "tangentPropagation" : true, "allowEdgeOverflow" : false});
        }
        {
            var Q0;
            Q0=makeQuery(id+"F1.opExtrude","SWEPT_BODY",BODY,{"disambiguationData":[OSD([sQuery(id+"F0.wireOp",EDGE,"E0.0"),sQuery(id+"F0.wireOp",EDGE,"E1"),sQuery(id+"F0.wireOp",EDGE,"E2"),sQuery(id+"F0.wireOp",EDGE,"E3"),sQuery(id+"F0.wireOp",EDGE,"E4"),sQuery(id+"F0.wireOp",EDGE,"E5"),sQuery(id+"F0.wireOp",EDGE,"E6.1.0.0"),sQuery(id+"F0.wireOp",EDGE,"E6.1.0.1"),sQuery(id+"F0.wireOp",EDGE,"E6.1.0.2"),sQuery(id+"F0.wireOp",EDGE,"E6.1.0.3"),sQuery(id+"F0.wireOp",EDGE,"E6.2.0.0"),sQuery(id+"F0.wireOp",EDGE,"E6.2.0.1"),sQuery(id+"F0.wireOp",EDGE,"E6.2.0.2"),sQuery(id+"F0.wireOp",EDGE,"E6.2.0.3"),sQuery(id+"F0.wireOp",EDGE,"E6.3.0.0"),sQuery(id+"F0.wireOp",EDGE,"E6.3.0.1"),sQuery(id+"F0.wireOp",EDGE,"E6.3.0.2"),sQuery(id+"F0.wireOp",EDGE,"E6.3.0.3"),sQuery(id+"F0.wireOp",EDGE,"E6.4.0.0"),sQuery(id+"F0.wireOp",EDGE,"E6.4.0.1"),sQuery(id+"F0.wireOp",EDGE,"E6.4.0.2"),sQuery(id+"F0.wireOp",EDGE,"E6.4.0.3"),sQuery(id+"F0.wireOp",EDGE,"E6.5.0.0"),sQuery(id+"F0.wireOp",EDGE,"E6.5.0.1"),sQuery(id+"F0.wireOp",EDGE,"E6.5.0.2"),sQuery(id+"F0.wireOp",EDGE,"E6.5.0.3"),sQuery(id+"F0.wireOp",EDGE,"E6.6.0.0"),sQuery(id+"F0.wireOp",EDGE,"E6.6.0.1"),sQuery(id+"F0.wireOp",EDGE,"E6.6.0.2"),sQuery(id+"F0.wireOp",EDGE,"E6.6.0.3"),sQuery(id+"F0.wireOp",EDGE,"E7.trimOffspring"),sQuery(id+"F0.wireOp",EDGE,"E8.trimOffspring"),sQuery(id+"F0.wireOp",EDGE,"E9.trimOffspring"),sQuery(id+"F0.wireOp",EDGE,"E10.trimOffspring"),sQuery(id+"F0.wireOp",EDGE,"E11.trimOffspring"),sQuery(id+"F0.wireOp",EDGE,"E12.trimOffspring"),sQuery(id+"F0.wireOp",EDGE,"E13"),sQuery(id+"F0.wireOp",EDGE,"E14"),sQuery(id+"F0.wireOp",EDGE,"E15.trimOffspring"),sQuery(id+"F0.wireOp",EDGE,"E16.trimOffspring"),sQuery(id+"F0.wireOp",EDGE,"E17.trimOffspring"),sQuery(id+"F0.wireOp",EDGE,"E18.trimOffspring"),sQuery(id+"F0.wireOp",EDGE,"E19.trimOffspring"),sQuery(id+"F0.wireOp",EDGE,"E20.trimOffspring"),sQuery(id+"F0.wireOp",EDGE,"E21.trimOffspring"),sQuery(id+"F0.wireOp",EDGE,"E22")])]});
            var Q1;
            Q1=makeQuery(id+"F1.opExtrude","SWEPT_FACE",FACE,{"disambiguationData":[OSD([sQuery(id+"F0.wireOp",EDGE,"E22")])]});
            mirror(context, id + "F11", {"operationType" : NewBodyOperationType.ADD, "entities" : qUnion([Q0]), "mirrorPlane" : qUnion([Q1])});
        }
        {
            var Q0;
            {var subQ0=makeQuery(id+"F1.opExtrude","CAP_FACE",FACE,{"disambiguationData":[OSD([sQuery(id+"F0.wireOp",EDGE,"E0.0"),sQuery(id+"F0.wireOp",EDGE,"E1"),sQuery(id+"F0.wireOp",EDGE,"E2"),sQuery(id+"F0.wireOp",EDGE,"E3"),sQuery(id+"F0.wireOp",EDGE,"E4"),sQuery(id+"F0.wireOp",EDGE,"E5"),sQuery(id+"F0.wireOp",EDGE,"E6.1.0.0"),sQuery(id+"F0.wireOp",EDGE,"E6.1.0.1"),sQuery(id+"F0.wireOp",EDGE,"E6.1.0.2"),sQuery(id+"F0.wireOp",EDGE,"E6.1.0.3"),sQuery(id+"F0.wireOp",EDGE,"E6.2.0.0"),sQuery(id+"F0.wireOp",EDGE,"E6.2.0.1"),sQuery(id+"F0.wireOp",EDGE,"E6.2.0.2"),sQuery(id+"F0.wireOp",EDGE,"E6.2.0.3"),sQuery(id+"F0.wireOp",EDGE,"E6.3.0.0"),sQuery(id+"F0.wireOp",EDGE,"E6.3.0.1"),sQuery(id+"F0.wireOp",EDGE,"E6.3.0.2"),sQuery(id+"F0.wireOp",EDGE,"E6.3.0.3"),sQuery(id+"F0.wireOp",EDGE,"E6.4.0.0"),sQuery(id+"F0.wireOp",EDGE,"E6.4.0.1"),sQuery(id+"F0.wireOp",EDGE,"E6.4.0.2"),sQuery(id+"F0.wireOp",EDGE,"E6.4.0.3"),sQuery(id+"F0.wireOp",EDGE,"E6.5.0.0"),sQuery(id+"F0.wireOp",EDGE,"E6.5.0.1"),sQuery(id+"F0.wireOp",EDGE,"E6.5.0.2"),sQuery(id+"F0.wireOp",EDGE,"E6.5.0.3"),sQuery(id+"F0.wireOp",EDGE,"E6.6.0.0"),sQuery(id+"F0.wireOp",EDGE,"E6.6.0.1"),sQuery(id+"F0.wireOp",EDGE,"E6.6.0.2"),sQuery(id+"F0.wireOp",EDGE,"E6.6.0.3"),sQuery(id+"F0.wireOp",EDGE,"E7.trimOffspring"),sQuery(id+"F0.wireOp",EDGE,"E8.trimOffspring"),sQuery(id+"F0.wireOp",EDGE,"E9.trimOffspring"),sQuery(id+"F0.wireOp",EDGE,"E10.trimOffspring"),sQuery(id+"F0.wireOp",EDGE,"E11.trimOffspring"),sQuery(id+"F0.wireOp",EDGE,"E12.trimOffspring"),sQuery(id+"F0.wireOp",EDGE,"E13"),sQuery(id+"F0.wireOp",EDGE,"E14"),sQuery(id+"F0.wireOp",EDGE,"E15.trimOffspring"),sQuery(id+"F0.wireOp",EDGE,"E16.trimOffspring"),sQuery(id+"F0.wireOp",EDGE,"E17.trimOffspring"),sQuery(id+"F0.wireOp",EDGE,"E18.trimOffspring"),sQuery(id+"F0.wireOp",EDGE,"E19.trimOffspring"),sQuery(id+"F0.wireOp",EDGE,"E20.trimOffspring"),sQuery(id+"F0.wireOp",EDGE,"E21.trimOffspring"),sQuery(id+"F0.wireOp",EDGE,"E22")])],"isStart":true});Q0=makeQuery(id+"F11.boolean.opBoolean","MERGE",FACE,{"derivedFrom":[subQ0,makeQuery(id+"F11.opPattern","COPY",FACE,{"derivedFrom":subQ0,"instanceName":"1"})]});}
            fillet(context, id + "F12", {"entities" : qUnion([Q0]), "radius" : 1 * mm, "tangentPropagation" : true, "allowEdgeOverflow" : false});
        }
    });
